FCSTD DOCUMENT  (FreeCAD 1.0R39109 (Git))
Label: Stator_Mold_Assembly
License: All rights reserved
LicenseURL: http://en.wikipedia.org/wiki/All_rights_reserved
objects: App::Link×7, Spreadsheet::Sheet×1, App::Part×1
EXTERNAL_REF file=Stator_Mold_Base.FCStd obj=Part001
EXTERNAL_REF file=../../../Master_of_Puppets.FCStd obj=Spreadsheet
EXTERNAL_REF file=Stator_Mold_BoltHeadLayer_Circular.FCStd obj=Part001
EXTERNAL_REF file=Stator_Mold_BoltHeadLayer_Hexagonal.FCStd obj=Part002
EXTERNAL_REF file=Stator_Mold_BoltShaftLayer_Circular.FCStd obj=Part001
EXTERNAL_REF file=Stator_Mold_BoltShaftLayer_Hexagonal.FCStd obj=Part003
EXTERNAL_REF file=Stator_Mold_Surround_Circular.FCStd obj=Body
EXTERNAL_REF file=Stator_Mold_Surround_Hexagonal.FCStd obj=Body
EXTERNAL_REF file=Stator_Mold_Island.FCStd obj=PolarPatternBody
EXTERNAL_REF file=Stator_Mold_Lid.FCStd obj=Pocket003Body
EXTERNAL_REF file=../Stator.FCStd obj=Part

FEATURE [App::Link] Link  label="Stator_Mold_Base"
  LinkedObject = -> <external Stator_Mold_Base.FCStd>#Part001
  expr: .Placement.Base.z = Spreadsheet.BaseZ
FEATURE [Spreadsheet::Sheet] Spreadsheet
  cells = A1='Inputs; A2='StatorThickness; B2(StatorThickness)==Master_of_Puppets#Spreadsheet.StatorThickness; A3='CalculatedWindTurbineShape; B3(CalculatedWindTurbineShape)==Master_of_Puppets#Spreadsheet.CalculatedWindTurbineShape; A4='Calculated; A5='DistanceBetweenLayers; B5(DistanceBetweenLayers)=0; A6='BaseZ; B6(BaseZ)==(StatorThickness + DistanceBetweenLayers) * 0; A7='BoltHeadLayerZ; B7(BoltHeadLayerZ)==(StatorThickness + DistanceBetweenLayers) * 1; A8='BoltShaftLayerZ; B8(BoltShaftLayerZ)==(StatorThickness + DistanceBetweenLayers) * 2; A9='SurroundZ; B9(SurroundZ)==(StatorThickness + DistanceBetweenLayers) * 3; A10='LidZ; B10(LidZ)==(StatorThickness + DistanceBetweenLayers) * 4; A11='BoltHeadLayer; A12='SmallBoltHeadLayer; B12(SmallBoltHeadLayer)==Stator_Mold_BoltHeadLayer_Circular#<<Stator_Mold_BoltHeadLayer_Assembly>>._self; A13='LargeBoltHeadLayer; B13(LargeBoltHeadLayer)==Stator_Mold_BoltHeadLayer_Hexagonal#<<Stator_Mold_BoltHeadLayer_Assembly>>._self; A14='BoltHeadLayer; B14(BoltHeadLayer)==CalculatedWindTurbineShape == <<Star>> ? LargeBoltHeadLayer : SmallBoltHeadLayer; A15='BoltShaftLayer; A16='SmallBoltShaftLayer; B16(SmallBoltShaftLayer)==Stator_Mold_BoltShaftLayer_Circular#<<Stator_Mold_BoltShaftLayer_Assembly>>._self; A17='LargeBoltShaftLayer; B17(LargeBoltShaftLayer)==Stator_Mold_BoltShaftLayer_Hexagonal#<<Stator_Mold_BoltShaftLayer_Assembly>>._self; A18='BoltShaftLayer; B18(BoltShaftLayer)==CalculatedWindTurbineShape == <<Star>> ? LargeBoltShaftLayer : SmallBoltShaftLayer; A19='Surround; A20='SmallSurround; B20(SmallSurround)==Stator_Mold_Surround_Circular#<<Stator_Mold_Surround>>._self; A21='LargeSurround; B21(LargeSurround)==Stator_Mold_Surround_Hexagonal#<<Stator_Mold_Surround>>._self; A22='Surround; B22(Surround)==CalculatedWindTurbineShape == <<Star>> ? LargeSurround : SmallSurround; A23='Stator; A24='StatorAngle; B24(StatorAngle)==CalculatedWindTurbineShape == <<T>> ? 60 : 0
FEATURE [App::Link] Link001  label="Stator_Mold_BoltHeadLayer"
  LinkPlacement = pos=(0,0,13) rot=(0,0,1;0rad)
  LinkedObject = -> <external Stator_Mold_BoltHeadLayer_Circular.FCStd>#Part001
  Placement = pos=(0,0,13) rot=(0,0,1;0rad)
  expr: .Placement.Base.z = Spreadsheet.BoltHeadLayerZ
  expr: LinkedObject = Spreadsheet.BoltHeadLayer
FEATURE [App::Link] Link002  label="Stator_Mold_BoltShaftLayer"
  LinkPlacement = pos=(0,0,26) rot=(0,0,1;0rad)
  LinkedObject = -> <external Stator_Mold_BoltShaftLayer_Circular.FCStd>#Part001
  Placement = pos=(0,0,26) rot=(0,0,1;0rad)
  expr: .Placement.Base.z = Spreadsheet.BoltShaftLayerZ
  expr: LinkedObject = Spreadsheet.BoltShaftLayer
FEATURE [App::Link] Link003  label="Stator_Mold_Surround"
  LinkPlacement = pos=(0,0,39) rot=(0,0,1;0rad)
  LinkedObject = -> <external Stator_Mold_Surround_Circular.FCStd>#Body
  Placement = pos=(0,0,39) rot=(0,0,1;0rad)
  expr: .Placement.Base.z = Spreadsheet.SurroundZ
  expr: LinkedObject = Spreadsheet.Surround
FEATURE [App::Link] Link004  label="Stator_Mold_Island"
  LinkPlacement = pos=(0,0,39) rot=(0,0,1;0rad)
  LinkedObject = -> <external Stator_Mold_Island.FCStd>#PolarPatternBody
  Placement = pos=(0,0,39) rot=(0,0,1;0rad)
  expr: .Placement.Base.z = Spreadsheet.SurroundZ
FEATURE [App::Link] Link005  label="Stator_Mold_Lid"
  LinkPlacement = pos=(0,0,52) rot=(0,0,1;0rad)
  LinkedObject = -> <external Stator_Mold_Lid.FCStd>#Pocket003Body
  Placement = pos=(0,0,52) rot=(0,0,1;0rad)
  expr: .Placement.Base.z = Spreadsheet.LidZ
FEATURE [App::Link] Link006  label="Stator"
  LinkPlacement = pos=(0,0,39) rot=(0,0,1;1.0472rad)
  LinkedObject = -> <external ../Stator.FCStd>#Part
  Placement = pos=(0,0,39) rot=(0,0,1;1.0472rad)
  expr: .Placement.Base.z = Spreadsheet.SurroundZ
  expr: .Placement.Rotation.Angle = Spreadsheet.StatorAngle
FEATURE [App::Part] Part  label="Stator_Mold_Assembly"
  Group = -> [Link,Link001,Link002,Link003,Link006,Link004,Link005]
  Origin = -> Origin

RESOLVED EXTERNAL PARTS (link-assembly join: the EXTERNAL_REF files above that resolve inside this repo's crawl, each included once):
---- part ../../../Master_of_Puppets.FCStd = doc fcstd_6404554055c4 (61625 chars; too large to inline — full recipe in that document) ----
---- part ../Stator.FCStd = doc fcstd_741fdd9bc27b ----
FCSTD DOCUMENT  (FreeCAD 0.21R33675 (Git))
Label: Stator
License: All rights reserved
LicenseURL: http://en.wikipedia.org/wiki/All_rights_reserved
objects: App::Link×2, Spreadsheet::Sheet×1, App::Part×1
EXTERNAL_REF file=../../Master_of_Puppets.FCStd obj=Alternator
EXTERNAL_REF file=../../Master_of_Puppets.FCStd obj=Spreadsheet
EXTERNAL_REF file=Stator_ResinCast_Circular.FCStd obj=PadBody001
EXTERNAL_REF file=Stator_ResinCast_Hexagonal.FCStd obj=Body
EXTERNAL_REF file=Stator_Coils.FCStd obj=Array

FEATURE [Spreadsheet::Sheet] Spreadsheet
  cells = A1='Inputs; A2='CalculatedWindTurbineShape; B2(CalculatedWindTurbineShape)==Master_of_Puppets#Spreadsheet.CalculatedWindTurbineShape; A3='StatorThickness; B3(StatorThickness)==Master_of_Puppets#Spreadsheet.StatorThickness; A4='MechanicalClearance; B4(MechanicalClearance)==Master_of_Puppets#Spreadsheet.MechanicalClearance; A5='MagnetThickness; B5(MagnetThickness)==Master_of_Puppets#Spreadsheet.MagnetThickness; A6='RotorDiskThickness; B6(RotorDiskThickness)==Master_of_Puppets#Spreadsheet.RotorDiskThickness; A7='CoilsAngle; B7(CoilsAngle)==Master_of_Puppets#Alternator.CoilsAngle; A8='StatorResinCast; A9='CircularStatorResinCast; B9(CircularStatorResinCast)==<<Stator_ResinCast_Circular>>#<<Stator_ResinCast>>._self; A10='HexagonalStatorResinCast; B10(HexagonalStatorResinCast)==<<Stator_ResinCast_Hexagonal>>#<<Stator_ResinCast>>._self; A11='StatorResinCast; B11(StatorResinCast)==CalculatedWindTurbineShape == <<Star>> ? HexagonalStatorResinCast : CircularStatorResinCast
FEATURE [App::Link] Link  label="ResinCast"
  LinkTransform = true
  LinkedObject = -> <external Stator_ResinCast_Circular.FCStd>#PadBody001
  expr: LinkedObject = Spreadsheet.StatorResinCast
FEATURE [App::Link] Link001  label="Coils"
  LinkPlacement = pos=(0,0,0) rot=(0,0,1;0.349066rad)
  LinkTransform = true
  LinkedObject = -> <external Stator_Coils.FCStd>#Array
  Placement = pos=(0,0,0) rot=(0,0,1;0.349066rad)
  expr: .LinkPlacement.Rotation.Angle = Spreadsheet.CoilsAngle
FEATURE [App::Part] Part  label="Stator"
  Group = -> [Link001,Link]
  Origin = -> Origin
---- part Stator_Mold_Base.FCStd = doc fcstd_d0ba9c10f7cb ----
FCSTD DOCUMENT  (FreeCAD 0.20R29177 (Git))
Label: Stator_Mold_Base
License: All rights reserved
LicenseURL: http://en.wikipedia.org/wiki/All_rights_reserved
objects: App::Link×6, App::Part×3, Sketcher::SketchObject×2, PartDesign::Pad×1, PartDesign::Pocket×1, Spreadsheet::Sheet×1, PartDesign::Body×1
note: 7 computed .brp shape members not serialized (recipe doc carries the construction recipe); baked Part::Feature solids carry a one-line shape summary decoded from their .brp
EXTERNAL_REF file=../../../Master_of_Puppets.FCStd obj=Alternator
EXTERNAL_REF file=../../../Master_of_Puppets.FCStd obj=Fastener
EXTERNAL_REF file=../../../Master_of_Puppets.FCStd obj=Spreadsheet
EXTERNAL_REF file=../../../Fasteners/Fastener_Bolt_Locating.FCStd obj=Binder
EXTERNAL_REF file=../../../Fasteners/Fastener_Washer_StatorMold.FCStd obj=Tube

FEATURE [Sketcher::SketchObject] Sketch
  AttachmentOffset = pos=(0,-12.5,0) rot=(0,0,1;0rad)
  FullyConstrained = true
  MapMode = 5
  Placement = pos=(0,-12.5,0) rot=(0,0,1;0rad)
  Support = -> [XY_Plane001]
  expr: .AttachmentOffset.Base.y = Spreadsheet.SketchY
  expr: Constraints[15] = Spreadsheet.StatorMoldSideLength
  sketch-geometry (6):
    g0: LineSegment StartX=-296.825 StartY=296.825 StartZ=0 EndX=296.825 EndY=296.825 EndZ=0
    g1: LineSegment StartX=296.825 StartY=296.825 StartZ=0 EndX=296.825 EndY=-296.825 EndZ=0
    g2: LineSegment StartX=296.825 StartY=-296.825 StartZ=0 EndX=-296.825 EndY=-296.825 EndZ=0
    g3: LineSegment StartX=-296.825 StartY=-296.825 StartZ=0 EndX=-296.825 EndY=296.825 EndZ=0
    g4: LineSegment StartX=-296.825 StartY=296.825 StartZ=0 EndX=296.825 EndY=-296.825 EndZ=0
    g5: LineSegment StartX=296.825 StartY=296.825 StartZ=0 EndX=-296.825 EndY=-296.825 EndZ=0
  constraints (16):
    c: Coincident(g0,g1)
    c: Coincident(g1,g2)
    c: Coincident(g2,g3)
    c: Coincident(g3,g0)
    c: Horizontal(g0)
    c: Horizontal(g2)
    c: Vertical(g1)
    c: Vertical(g3)
    c: Coincident(g4,g0)
    c: Coincident(g4,g1)
    c: Coincident(g5,g0)
    c: Coincident(g5,g2)
    c: PointOnObject(g-1,g5)
    c: PointOnObject(g-1,g4)
    c: Equal(g0,g3)
    c: Distance(g0) = 593.65
FEATURE [PartDesign::Pad] Pad
  AllowMultiFace = false
  Direction = (0,0,1)
  Length = 13
  Length2 = 100
  Profile = -> Sketch
  Type = 0
  expr: Length = Spreadsheet.StatorThickness
FEATURE [Sketcher::SketchObject] Sketch001
  AttachmentOffset = pos=(0,-12.5,0) rot=(0,0,1;0rad)
  FullyConstrained = true
  MapMode = 5
  Placement = pos=(0,-12.5,13) rot=(0,0,1;0rad)
  Support = -> [Pad]
  expr: .AttachmentOffset.Base.y = Spreadsheet.SketchY
  expr: Constraints[14] = Spreadsheet.StatorMoldBoltRadius
  expr: Constraints[5] = 45
  expr: Constraints[8] = Spreadsheet.DistanceOfLocatingHoleFromCenter
  sketch-geometry (6):
    g0: LineSegment StartX=-266.804 StartY=266.804 StartZ=0 EndX=0 EndY=0 EndZ=0
    g1: LineSegment StartX=0 StartY=0 StartZ=0 EndX=266.804 EndY=266.804 EndZ=0
    g2: LineSegment StartX=0 StartY=0 StartZ=0 EndX=266.804 EndY=-266.804 EndZ=0
    g3: Circle CenterX=-266.804 CenterY=266.804 CenterZ=0 NormalX=0 NormalY=0 NormalZ=1 AngleXU=0 Radius=6
    g4: Circle CenterX=266.804 CenterY=266.804 CenterZ=0 NormalX=0 NormalY=0 NormalZ=1 AngleXU=0 Radius=6
    g5: Circle CenterX=266.804 CenterY=-266.804 CenterZ=0 NormalX=0 NormalY=0 NormalZ=1 AngleXU=0 Radius=6
  constraints (15):
    c: Coincident(g0,g-1)
    c: Coincident(g0,g1)
    c: Coincident(g-1,g2)
    c: Parallel(g0,g2)
    c: Perpendicular(g2,g1)
    c: Angle(g-2,g0) = 0.785398
    c: Equal(g0,g1)
    c: Equal(g1,g2)
    c: Distance(g0) = 377.318
    c: Coincident(g3,g0)
    c: Coincident(g5,g2)
    c: Coincident(g4,g1)
    c: Equal(g3,g4)
    c: Equal(g4,g5)
    c: Radius(g3) = 6
FEATURE [PartDesign::Pocket] Pocket
  AllowMultiFace = false
  BaseFeature = -> Pad
  Direction = (0,0,-1)
  Length = 5
  Length2 = 100
  Profile = -> Sketch001
  Type = 1
FEATURE [Spreadsheet::Sheet] Spreadsheet
  cells = A1=Inputs; A2=Spreadsheet; A3=StatorThickness; B3(StatorThickness)==Master_of_Puppets#Spreadsheet.StatorThickness; A4=StatorMoldBoltDiameter; B4(StatorMoldBoltDiameter)==Master_of_Puppets#Alternator.StatorMoldBoltDiameter; A5=RotorDiskRadius; B5(RotorDiskRadius)==Master_of_Puppets#Spreadsheet.RotorDiskRadius; A6=Alternator; A7=StatorHolesCircumradius; B7(StatorHolesCircumradius)==Master_of_Puppets#Alternator.StatorHolesCircumradius; A8=EarSize; B8(EarSize)==Master_of_Puppets#Alternator.EarSize; A9=SketchY; B9(SketchY)==Master_of_Puppets#Alternator.SketchY; A10=StatorMoldSideLength; B10(StatorMoldSideLength)==Master_of_Puppets#Alternator.StatorMoldSideLength; A11=DistanceOfLocatingHoleFromCenter; B11(DistanceOfLocatingHoleFromCenter)==Master_of_Puppets#Alternator.DistanceOfLocatingHoleFromCenter; A12=LocatingBolt1X; B12(LocatingBolt1X)==Master_of_Puppets#Alternator.LocatingBolt1X; A13=LocatingBolt1Y; B13(LocatingBolt1Y)==Master_of_Puppets#Alternator.LocatingBolt1Y; A14=LocatingBolt2X; B14(LocatingBolt2X)==Master_of_Puppets#Alternator.LocatingBolt2X; A15=LocatingBolt2Y; B15(LocatingBolt2Y)==Master_of_Puppets#Alternator.LocatingBolt2Y; A16=LocatingBolt3X; B16(LocatingBolt3X)==Master_of_Puppets#Alternator.LocatingBolt3X; A17=LocatingBolt3Y; B17(LocatingBolt3Y)==Master_of_Puppets#Alternator.LocatingBolt3Y; A18=Fastener; A19=WasherThickness; B19(WasherThickness)==Master_of_Puppets#Fastener.WasherThickness; A20=Calculated; A21=StatorMoldBoltRadius; B21(StatorMoldBoltRadius)==StatorMoldBoltDiameter / 2; A22=BoltZ; B22(BoltZ)==-WasherThickness; A23=NutZ; B23(NutZ)==StatorThickness * 5; A24=WasherZ; B24(WasherZ)==-WasherThickness
FEATURE [PartDesign::Body] PocketBody  label="Stator_Mold_Base"
  Group = -> [Sketch,Pad,Sketch001,Pocket]
  Openafpm_Flat = true
  Origin = -> Origin001
  Tip = -> Pocket
FEATURE [App::Link] Link001  label="Fastener_Bolt2"
  LinkPlacement = pos=(266.804,254.304,-2.5) rot=(0,0,1;0rad)
  LinkedObject = -> Link
  Placement = pos=(266.804,254.304,-2.5) rot=(0,0,1;0rad)
  expr: .Placement.Base.x = Spreadsheet.LocatingBolt2X
  expr: .Placement.Base.y = Spreadsheet.LocatingBolt2Y
  expr: .Placement.Base.z = Spreadsheet.BoltZ
FEATURE [App::Link] Link002  label="Fastener_Bolt3"
  LinkPlacement = pos=(266.804,-279.304,-2.5) rot=(0,0,1;0rad)
  LinkedObject = -> Link001
  Placement = pos=(266.804,-279.304,-2.5) rot=(0,0,1;0rad)
  expr: .Placement.Base.x = Spreadsheet.LocatingBolt3X
  expr: .Placement.Base.y = Spreadsheet.LocatingBolt3Y
  expr: .Placement.Base.z = Spreadsheet.BoltZ
FEATURE [App::Link] Link  label="Fastener_Bolt1"
  LinkPlacement = pos=(-266.804,254.304,-2.5) rot=(0,0,1;0rad)
  LinkedObject = -> <external ../../../Fasteners/Fastener_Bolt_Locating.FCStd>#Binder
  Placement = pos=(-266.804,254.304,-2.5) rot=(0,0,1;0rad)
  Scale = -1
  ScaleVector = (-1,-1,-1)
  expr: .Placement.Base.x = Spreadsheet.LocatingBolt1X
  expr: .Placement.Base.y = Spreadsheet.LocatingBolt1Y
  expr: .Placement.Base.z = Spreadsheet.BoltZ
FEATURE [App::Part] Part  label="LocatingBolts"
  Group = -> [Link,Link001,Link002]
  Origin = -> Origin
FEATURE [App::Link] Link003  label="Washer1"
  LinkPlacement = pos=(-266.804,254.304,-2.5) rot=(0,0,1;0rad)
  LinkedObject = -> <external ../../../Fasteners/Fastener_Washer_StatorMold.FCStd>#Tube
  Placement = pos=(-266.804,254.304,-2.5) rot=(0,0,1;0rad)
  expr: .Placement.Base.x = Spreadsheet.LocatingBolt1X
  expr: .Placement.Base.y = Spreadsheet.LocatingBolt1Y
  expr: .Placement.Base.z = Spreadsheet.WasherZ
FEATURE [App::Link] Link004  label="Washer2"
  LinkPlacement = pos=(266.804,254.304,-2.5) rot=(0,0,1;0rad)
  LinkedObject = -> Link003
  Placement = pos=(266.804,254.304,-2.5) rot=(0,0,1;0rad)
  expr: .Placement.Base.x = Spreadsheet.LocatingBolt2X
  expr: .Placement.Base.y = Spreadsheet.LocatingBolt2Y
  expr: .Placement.Base.z = Spreadsheet.WasherZ
FEATURE [App::Link] Link005  label="Washer3"
  LinkPlacement = pos=(266.804,-279.304,-2.5) rot=(0,0,1;0rad)
  LinkedObject = -> Link004
  Placement = pos=(266.804,-279.304,-2.5) rot=(0,0,1;0rad)
  expr: .Placement.Base.x = Spreadsheet.LocatingBolt3X
  expr: .Placement.Base.y = Spreadsheet.LocatingBolt3Y
  expr: .Placement.Base.z = Spreadsheet.WasherZ
FEATURE [App::Part] Part002  label="LocatingWashers"
  Group = -> [Link003,Link004,Link005]
  Origin = -> Origin003
FEATURE [App::Part] Part001  label="Stator_Mold_Base_Assembly"
  Group = -> [PocketBody,Part,Part002]
  Origin = -> Origin002
---- part Stator_Mold_BoltHeadLayer_Circular.FCStd = doc fcstd_cd0f8b75a41d ----
FCSTD DOCUMENT  (FreeCAD 1.0R39109 (Git))
Label: Stator_Mold_BoltHeadLayer_Circular
License: All rights reserved
LicenseURL: http://en.wikipedia.org/wiki/All_rights_reserved
objects: App::Link×18, Part::FeaturePython×12, App::Part×9, Sketcher::SketchObject×4, PartDesign::PolarPattern×4, PartDesign::Pocket×4, Part::Mirroring×3, PartDesign::Plane×1, PartDesign::Mirrored×1, PartDesign::SubShapeBinder×1, PartDesign::FeatureBase×1, PartDesign::MultiTransform×1, Spreadsheet::Sheet×1, PartDesign::Body×1
note: 40 computed .brp shape members not serialized (recipe doc carries the construction recipe); baked Part::Feature solids carry a one-line shape summary decoded from their .brp
EXTERNAL_REF file=Stator_Mold_Base.FCStd obj=PocketBody
EXTERNAL_REF file=../../../Master_of_Puppets.FCStd obj=Alternator
EXTERNAL_REF file=../../../Master_of_Puppets.FCStd obj=Fastener
EXTERNAL_REF file=../../../Master_of_Puppets.FCStd obj=Spreadsheet
EXTERNAL_REF file=../../../Fasteners/Fastener_Bolt_StatorMold.FCStd obj=Binder
EXTERNAL_REF file=../../../Fasteners/Fastener_HexNut_StatorMold.FCStd obj=Binder
EXTERNAL_REF file=../../../Fasteners/Fastener_Washer_StatorMold.FCStd obj=Tube

FEATURE [PartDesign::Plane] DatumPlane001  label="DatumPlane"
  AttachmentOffset = pos=(0,0,13) rot=(0,0,1;0rad)
  AttachmentSupport = -> [XY_Plane]
  Length = 1060.2
  MapMode = 5
  Placement = pos=(0,0,13) rot=(0,0,1;0rad)
  ResizeMode = 0
  Width = 1060.2
  expr: .AttachmentOffset.Base.z = Spreadsheet.StatorThickness
FEATURE [Sketcher::SketchObject] Sketch005  label="MiddleHolesSketch"
  ArcFitTolerance = 0
  AttachmentOffset = pos=(0,0,0) rot=(0,0,1;0.785398rad)
  AttachmentSupport = -> [DatumPlane001]
  FullyConstrained = true
  MakeInternals = false
  MapMode = 5
  Placement = pos=(0,0,13) rot=(0,0,1;0.785398rad)
  expr: .AttachmentOffset.Rotation.Angle = Spreadsheet.StatorMoldHolesSketchAngle
  expr: Constraints[16] = Spreadsheet.EarAngle
  expr: Constraints[20] = Spreadsheet.LargeHoleAngle
  expr: Constraints[3] = Spreadsheet.LengthMiddleHoles
  expr: Constraints[40] = Spreadsheet.Inradius
  expr: Constraints[6] = Spreadsheet.EarSize
  sketch-geometry (17):
    g0: Circle [constr] CenterX=0 CenterY=0 CenterZ=0 NormalX=0 NormalY=0 NormalZ=1 AngleXU=0 Radius=309
    g1: LineSegment [constr] StartX=0 StartY=0 StartZ=0 EndX=0 EndY=-309 EndZ=0
    g2: Circle [constr] CenterX=0 CenterY=-309 CenterZ=0 NormalX=0 NormalY=0 NormalZ=1 AngleXU=0 Radius=35
    g3: LineSegment [constr] StartX=16.18 StartY=-340.036 StartZ=0 EndX=142.846 EndY=-274 EndZ=0
    g4: LineSegment [constr] StartX=-16.18 StartY=-340.036 StartZ=0 EndX=-142.846 EndY=-274 EndZ=0
    g5: LineSegment [constr] StartX=0 StartY=0 StartZ=0 EndX=-218.496 EndY=-218.496 EndZ=0
    g6: LineSegment [constr] StartX=0 StartY=0 StartZ=0 EndX=218.496 EndY=-218.496 EndZ=0
    g7: ArcOfCircle [constr] CenterX=0 CenterY=0 CenterZ=0 NormalX=0 NormalY=0 NormalZ=1 AngleXU=0 Radius=309 StartAngle=3.92699 EndAngle=4.23182
    g8: ArcOfCircle [constr] CenterX=0 CenterY=0 CenterZ=0 NormalX=0 NormalY=0 NormalZ=1 AngleXU=0 Radius=309 StartAngle=5.19296 EndAngle=5.49779
    g9: LineSegment [constr] StartX=0 StartY=0 StartZ=0 EndX=-118.249 EndY=-285.479 EndZ=0
    g10: LineSegment StartX=-118.249 StartY=-295.869 StartZ=0 EndX=-109.251 EndY=-290.674 EndZ=0
    g11: LineSegment StartX=-109.251 StartY=-290.674 StartZ=0 EndX=-109.251 EndY=-280.284 EndZ=0
    g12: LineSegment StartX=-109.251 StartY=-280.284 StartZ=0 EndX=-118.249 EndY=-275.089 EndZ=0
    g13: LineSegment StartX=-118.249 StartY=-275.089 StartZ=0 EndX=-127.247 EndY=-280.284 EndZ=0
    g14: LineSegment StartX=-127.247 StartY=-280.284 StartZ=0 EndX=-127.247 EndY=-290.674 EndZ=0
    g15: LineSegment StartX=-127.247 StartY=-290.674 StartZ=0 EndX=-118.249 EndY=-295.869 EndZ=0
    g16: Circle [constr] CenterX=-118.249 CenterY=-285.479 CenterZ=0 NormalX=0 NormalY=0 NormalZ=1 AngleXU=0 Radius=10.39
  constraints (40):
    c: Coincident(g0,g-1)
    c: Coincident(g1,g-1)
    c: Vertical(g1)
    c: Radius(g0) = 309
    c: Coincident(g2,g1)
    c: Tangent(g3,g0)
    c: Radius(g2) = 35
    c: Symmetric(g6,g5,g1)
    c: Coincident(g7,g5)
    c: Coincident(g7,g4)
    c: Coincident(g8,g6)
    c: Coincident(g8,g3)
    c: Coincident(g6,g5)
    c: Coincident(g5,g7)
    c: Coincident(g5,g-1)
    c: Coincident(g8,g5)
    c: Angle(g5,g6) = 1.5708
    c: Tangent(g3,g2) = -1.5708
    c: Tangent(g4,g0) = 1.5708
    c: Coincident(g9,g-1)
    c: Angle(g5,g9) = 0.392699
    c: Tangent(g4,g2) = 1.5708
    c: PointOnObject(g1,g0)
    c: Coincident(g10,g11)
    c: Coincident(g11,g12)
    c: Coincident(g12,g13)
    c: Coincident(g13,g14)
    c: Coincident(g14,g15)
    c: Coincident(g15,g10)
    c: Equal(g10, g11-g15) x5
    c: PointOnObject(g10,g16)
    c: PointOnObject(g12,g16)
    c: PointOnObject(g13,g16)
    c: PointOnObject(g14,g16)
    c: PointOnObject(g15,g16)
    c: Coincident(g16,g9)
    c: Radius(g16) = 10.39
    c: PointOnObject(g11,g16)
    c: Vertical(g10,g12)
    c: PointOnObject(g9,g0)
FEATURE [PartDesign::Mirrored] Mirrored  label="MiddleHolesMirrored"
  MirrorPlane = -> Sketch005 [V_Axis]
  Suppressed = false
  TransformMode = 0
FEATURE [PartDesign::PolarPattern] PolarPattern002  label="MiddleHolesPolarPattern"
  Angle = 360
  Axis = -> Sketch005 [N_Axis]
  Mode = 0
  Occurrences = 4
  Offset = 120
  Suppressed = false
  TransformMode = 0
  expr: Occurrences = Spreadsheet.NumberOfStatorHoles
FEATURE [Sketcher::SketchObject] Sketch006  label="LargeHoleOuterSketch"
  ArcFitTolerance = 0
  AttachmentOffset = pos=(0,0,0) rot=(0,0,1;0.785398rad)
  AttachmentSupport = -> [DatumPlane001]
  FullyConstrained = true
  MakeInternals = false
  MapMode = 5
  Placement = pos=(0,0,13) rot=(0,0,1;0.785398rad)
  expr: .AttachmentOffset.Rotation.Angle = Spreadsheet.StatorMoldHolesSketchAngle
  expr: Constraints[16] = Spreadsheet.Inradius
  expr: Constraints[1] = Spreadsheet.LargeHoleCircumradius
  sketch-geometry (14):
    g0: Circle [constr] CenterX=0 CenterY=0 CenterZ=0 NormalX=0 NormalY=0 NormalZ=1 AngleXU=0 Radius=344
    g1: LineSegment StartX=5.195 StartY=-335.002 StartZ=0 EndX=-5.195 EndY=-335.002 EndZ=0
    g2: LineSegment StartX=-5.195 StartY=-335.002 StartZ=0 EndX=-10.39 EndY=-344 EndZ=0
    g3: LineSegment StartX=-10.39 StartY=-344 StartZ=0 EndX=-5.195 EndY=-352.998 EndZ=0
    g4: LineSegment StartX=-5.195 StartY=-352.998 StartZ=0 EndX=5.195 EndY=-352.998 EndZ=0
    g5: LineSegment StartX=5.195 StartY=-352.998 StartZ=0 EndX=10.39 EndY=-344 EndZ=0
    g6: LineSegment StartX=10.39 StartY=-344 StartZ=0 EndX=5.195 EndY=-335.002 EndZ=0
    g7: Circle [constr] CenterX=9e-16 CenterY=-344 CenterZ=0 NormalX=0 NormalY=0 NormalZ=1 AngleXU=0 Radius=10.39
    g8: LineSegment [constr] StartX=-5.195 StartY=-352.998 StartZ=0 EndX=9e-16 EndY=-344 EndZ=0
    g9: LineSegment [constr] StartX=9e-16 StartY=-344 StartZ=0 EndX=5.195 EndY=-335.002 EndZ=0
    g10: LineSegment [constr] StartX=-5.195 StartY=-335.002 StartZ=0 EndX=9e-16 EndY=-344 EndZ=0
    g11: LineSegment [constr] StartX=9e-16 StartY=-344 StartZ=0 EndX=5.195 EndY=-352.998 EndZ=0
    g12: LineSegment [constr] StartX=-10.39 StartY=-344 StartZ=0 EndX=0 EndY=-344 EndZ=0
    g13: LineSegment [constr] StartX=9e-16 StartY=-344 StartZ=0 EndX=10.39 EndY=-344 EndZ=0
  constraints (35):
    c: Coincident(g0,g-1)
    c: Radius(g0) = 344
    c: Coincident(g1,g2)
    c: Coincident(g2,g3)
    c: Coincident(g3,g4)
    c: Coincident(g4,g5)
    c: Coincident(g5,g6)
    c: Coincident(g6,g1)
    c: PointOnObject(g1,g7)
    c: PointOnObject(g2,g7)
    c: PointOnObject(g3,g7)
    c: PointOnObject(g4,g7)
    c: PointOnObject(g5,g7)
    c: PointOnObject(g6,g7)
    c: PointOnObject(g7,g0)
    c: PointOnObject(g7,g-2)
    c: Radius(g7) = 10.39
    c: Coincident(g8,g3)
    c: Coincident(g8,g7)
    c: Coincident(g9,g8)
    c: Coincident(g9,g1)
    c: Coincident(g1,g10)
    c: Coincident(g10,g8)
    c: Coincident(g10,g11)
    c: Coincident(g2,g12)
    c: Coincident(g12,g8)
    c: Coincident(g12,g13)
    c: Coincident(g13,g5)
    c: Angle(g9,g10) = 1.0472
    c: Angle(g13,g9) = 1.0472
    c: Angle(g11,g13) = 1.0472
    c: Angle(g8,g11) = 1.0472
    c: Angle(g12,g8) = 1.0472
    c: Horizontal(g2,g5)
    c: Coincident(g11,g4)
FEATURE [Sketcher::SketchObject] Sketch007  label="LargeHoleInnerSketch"
  ArcFitTolerance = 0
  AttachmentSupport = -> [DatumPlane001]
  FullyConstrained = true
  MakeInternals = false
  MapMode = 5
  Placement = pos=(0,0,13) rot=(0,0,1;0rad)
  expr: Constraints[1] = Spreadsheet.LengthMiddleHoles
  expr: Constraints[31] = Spreadsheet.Inradius
  sketch-geometry (14):
    g0: Circle [constr] CenterX=0 CenterY=0 CenterZ=0 NormalX=0 NormalY=0 NormalZ=1 AngleXU=0 Radius=309
    g1: LineSegment StartX=-5.195 StartY=317.998 StartZ=0 EndX=-10.39 EndY=309 EndZ=0
    g2: LineSegment StartX=-10.39 StartY=309 StartZ=0 EndX=-5.195 EndY=300.002 EndZ=0
    g3: LineSegment StartX=-5.195 StartY=300.002 StartZ=0 EndX=5.195 EndY=300.002 EndZ=0
    g4: LineSegment StartX=5.195 StartY=300.002 StartZ=0 EndX=10.39 EndY=309 EndZ=0
    g5: LineSegment StartX=10.39 StartY=309 StartZ=0 EndX=5.195 EndY=317.998 EndZ=0
    g6: LineSegment StartX=5.195 StartY=317.998 StartZ=0 EndX=-5.195 EndY=317.998 EndZ=0
    g7: Circle [constr] CenterX=0 CenterY=309 CenterZ=0 NormalX=0 NormalY=0 NormalZ=1 AngleXU=0 Radius=10.39
    g8: LineSegment [constr] StartX=-5.195 StartY=317.998 StartZ=0 EndX=0 EndY=309 EndZ=0
    g9: LineSegment [constr] StartX=0 StartY=309 StartZ=0 EndX=5.195 EndY=300.002 EndZ=0
    g10: LineSegment [constr] StartX=-5.195 StartY=300.002 StartZ=0 EndX=0 EndY=309 EndZ=0
    g11: LineSegment [constr] StartX=0 StartY=309 StartZ=0 EndX=5.195 EndY=317.998 EndZ=0
    g12: LineSegment [constr] StartX=-10.39 StartY=309 StartZ=0 EndX=0 EndY=309 EndZ=0
    g13: LineSegment [constr] StartX=0 StartY=309 StartZ=0 EndX=10.39 EndY=309 EndZ=0
  constraints (35):
    c: Coincident(g0,g-1)
    c: Radius(g0) = 309
    c: PointOnObject(g7,g0)
    c: Coincident(g1,g2)
    c: Coincident(g2,g3)
    c: Coincident(g3,g4)
    c: Coincident(g4,g5)
    c: Coincident(g5,g6)
    c: Coincident(g6,g1)
    c: PointOnObject(g1,g7)
    c: PointOnObject(g2,g7)
    c: PointOnObject(g3,g7)
    c: PointOnObject(g4,g7)
    c: PointOnObject(g5,g7)
    c: PointOnObject(g6,g7)
    c: Coincident(g8,g1)
    c: Coincident(g9,g8)
    c: Coincident(g9,g3)
    c: Coincident(g10,g2)
    c: Coincident(g10,g8)
    c: Coincident(g11,g8)
    c: Coincident(g11,g5)
    c: Coincident(g12,g1)
    c: Coincident(g12,g8)
    c: Coincident(g13,g8)
    c: Coincident(g13,g4)
    c: Angle(g11,g8) = 1.0472
    c: Angle(g13,g11) = 1.0472
    c: Angle(g9,g13) = 1.0472
    c: Angle(g10,g9) = 1.0472
    c: Angle(g12,g10) = 1.0472
    c: Radius(g7) = 10.39
    c: Horizontal(g4,g1)
    c: Coincident(g8,g7)
    c: PointOnObject(g7,g-2)
FEATURE [PartDesign::SubShapeBinder] Binder
  BindCopyOnChange = 0
  BindMode = 0
  ClaimChildren = true
  Context = -> Body [Binder.]
  Fuse = false
  MakeFace = true
  OffsetFill = false
  OffsetIntersection = false
  OffsetJoinType = 0
  OffsetOpenResult = false
  PartialLoad = false
  Refine = true
  Relative = true
  Support = -> [<external Stator_Mold_Base.FCStd>#PocketBody]
  _Version = 2
FEATURE [PartDesign::FeatureBase] BaseFeature
  BaseFeature = -> Binder
  Suppressed = false
FEATURE [PartDesign::Pocket] Pocket001  label="MiddleHolesPocket"
  BaseFeature = -> BaseFeature
  Direction = (0,0,-1)
  Length = 5
  Length2 = 100
  Profile = -> Sketch005
  Suppressed = false
  Type = 1
FEATURE [PartDesign::MultiTransform] MultiTransform  label="MiddleHolesMultiTransform"
  BaseFeature = -> Pocket001
  Originals = -> [Pocket001]
  Suppressed = false
  TransformMode = 0
  Transformations = -> [Mirrored,PolarPattern002]
FEATURE [PartDesign::Pocket] Pocket002  label="LargeHoleOuterPocket"
  BaseFeature = -> MultiTransform
  Direction = (0,0,-1)
  Length = 5
  Length2 = 100
  Profile = -> Sketch006
  Suppressed = false
  Type = 1
FEATURE [PartDesign::PolarPattern] PolarPattern003  label="LargeHoleOuterPolarPattern"
  Angle = 360
  Axis = -> Sketch006 [N_Axis]
  BaseFeature = -> Pocket002
  Mode = 0
  Occurrences = 4
  Offset = 120
  Originals = -> [Pocket002]
  Suppressed = false
  TransformMode = 0
  expr: Occurrences = Spreadsheet.NumberOfStatorHoles
FEATURE [PartDesign::Pocket] Pocket003  label="LargeHoleInnerPocket"
  BaseFeature = -> PolarPattern003
  Direction = (0,0,-1)
  Length = 5
  Length2 = 100
  Profile = -> Sketch007
  Suppressed = false
  Type = 1
FEATURE [PartDesign::PolarPattern] PolarPattern004  label="LargeHoleInnerPolarPattern"
  Angle = 360
  Axis = -> Z_Axis
  BaseFeature = -> Pocket003
  Mode = 0
  Occurrences = 4
  Offset = 120
  Originals = -> [Pocket003]
  Suppressed = false
  TransformMode = 0
  expr: Angle = Spreadsheet.LargeInnerPolarPatternOverallAngle
  expr: Occurrences = Spreadsheet.LargeInnerPolarPatternOccurrences
FEATURE [Spreadsheet::Sheet] Spreadsheet
  cells = A1='Inputs; A2='Spreadsheet; A3='StatorThickness; A4(StatorThickness)==Master_of_Puppets#Spreadsheet.StatorThickness; A5='Alternator; A6='EarSize; B6='NumberOfStatorHoles; C6='IslandInnerRadius; A7(EarSize)==Master_of_Puppets#Alternator.EarSize; B7(NumberOfStatorHoles)==Master_of_Puppets#Alternator.NumberOfStatorHoles; C7(IslandInnerRadius)==Master_of_Puppets#Alternator.IslandInnerRadius; A8='EarAngle; B8='StatorMoldBoltWidthAcrossCorners; C8='StatorHolesCircumradius; A9(EarAngle)==Master_of_Puppets#Alternator.EarAngle; B9(StatorMoldBoltWidthAcrossCorners)==Master_of_Puppets#Alternator.StatorMoldBoltWidthAcrossCorners; C9(StatorHolesCircumradius)==Master_of_Puppets#Alternator.StatorHolesCircumradius; A10='LengthMiddleHoles; B10='StatorMoldIslandNumberOfBolts; C10='StatorMoldHolesSketchAngle; A11(LengthMiddleHoles)==Master_of_Puppets#Alternator.LengthMiddleHoles; B11(StatorMoldIslandNumberOfBolts)==Master_of_Puppets#Alternator.StatorMoldIslandNumberOfBolts; C11(StatorMoldHolesSketchAngle)==Master_of_Puppets#Alternator.StatorMoldHolesSketchAngle; A12='LocatingBolt1X; B12='LocatingBolt1Y; A13(LocatingBolt1X)==Master_of_Puppets#Alternator.LocatingBolt1X; B13(LocatingBolt1Y)==Master_of_Puppets#Alternator.LocatingBolt1Y; A14='LocatingBolt2X; B14='LocatingBolt2Y; A15(LocatingBolt2X)==Master_of_Puppets#Alternator.LocatingBolt2X; B15(LocatingBolt2Y)==Master_of_Puppets#Alternator.LocatingBolt2Y; A16='LocatingBolt3X; B16='LocatingBolt3Y; A17(LocatingBolt3X)==Master_of_Puppets#Alternator.LocatingBolt3X; B17(LocatingBolt3Y)==Master_of_Puppets#Alternator.LocatingBolt3Y; A18='LargeInnerPolarPatternOccurrences; B18='LargeInnerPolarPatternOverallAngle; A19(LargeInnerPolarPatternOccurrences)==Master_of_Puppets#Alternator.LargeInnerPolarPatternOccurrences; B19(LargeInnerPolarPatternOverallAngle)==Master_of_Puppets#Alternator.LargeInnerPolarPatternOverallAngle; A20='Fastener; A21='HexNutThickness; B21='WasherThickness; A22(HexNutThickness)==Master_of_Puppets#Fastener.HexNutThickness; B22(WasherThickness)==Master_of_Puppets#Fastener.WasherThickness; A23='Static; A24='BoltAngle; A25(BoltAngle)==30 deg; A26='Calculated; A27='LargeHoleCircumradius; B27='LargeHoleAngle; C27='Inradius; D27='https://calcresource.com/geom-hexagon.html; A28(LargeHoleCircumradius)==LengthMiddleHoles + EarSize; B28(LargeHoleAngle)==EarAngle / 4; C28(Inradius)==StatorMoldBoltWidthAcrossCorners / 2; A29='Fastener_Middle_X; B29='Fastener_Middle_Y; C29='TopOfStatorMold; D29='Duplicated in Stator_Mold_BoltHeadLayer_Hexagonal; A30(Fastener_Middle_X)==-LengthMiddleHoles * sin(LargeHoleAngle); B30(Fastener_Middle_Y)==-LengthMiddleHoles * cos(LargeHoleAngle); C30(TopOfStatorMold)==StatorThickness * 4; A31='HexNutZ; A32(HexNutZ)==TopOfStatorMold + WasherThickness
FEATURE [Sketcher::SketchObject] Sketch  label="InnerBoltHeadHoleSketch"
  ArcFitTolerance = 0
  AttachmentSupport = -> [DatumPlane001]
  FullyConstrained = true
  MakeInternals = false
  MapMode = 5
  Placement = pos=(0,0,13) rot=(0,0,1;0rad)
  expr: Constraints[1] = Spreadsheet.IslandInnerRadius
  expr: Constraints[33] = Spreadsheet.Inradius
  sketch-geometry (14):
    g0: Circle [constr] CenterX=0 CenterY=0 CenterZ=0 NormalX=0 NormalY=0 NormalZ=1 AngleXU=0 Radius=128.499
    g1: LineSegment StartX=5.19515 StartY=137.497 StartZ=0 EndX=-5.19485 EndY=137.497 EndZ=0
    g2: LineSegment StartX=-5.19485 StartY=137.497 StartZ=0 EndX=-10.3898 EndY=128.499 EndZ=0
    g3: LineSegment StartX=-10.3898 StartY=128.499 StartZ=0 EndX=-5.19485 EndY=119.501 EndZ=0
    g4: LineSegment StartX=-5.19485 StartY=119.501 StartZ=0 EndX=5.19515 EndY=119.501 EndZ=0
    g5: LineSegment StartX=5.19515 StartY=119.501 StartZ=0 EndX=10.3902 EndY=128.499 EndZ=0
    g6: LineSegment StartX=10.3902 StartY=128.499 StartZ=0 EndX=5.19515 EndY=137.497 EndZ=0
    g7: Circle [constr] CenterX=0.000154142 CenterY=128.499 CenterZ=0 NormalX=0 NormalY=0 NormalZ=1 AngleXU=0 Radius=10.39
    g8: LineSegment [constr] StartX=-5.19485 StartY=119.501 StartZ=0 EndX=0.000154142 EndY=128.499 EndZ=0
    g9: LineSegment [constr] StartX=0.000154142 StartY=128.499 StartZ=0 EndX=5.19515 EndY=137.497 EndZ=0
    g10: LineSegment [constr] StartX=10.3902 StartY=128.499 StartZ=0 EndX=0.000154142 EndY=128.499 EndZ=0
    g11: LineSegment [constr] StartX=0.000154142 StartY=128.499 StartZ=0 EndX=-10.3898 EndY=128.499 EndZ=0
    g12: LineSegment [constr] StartX=-5.19485 StartY=137.497 StartZ=0 EndX=0.000154142 EndY=128.499 EndZ=0
    g13: LineSegment [constr] StartX=0.000154142 StartY=128.499 StartZ=0 EndX=5.19515 EndY=119.501 EndZ=0
  constraints (35):
    c: Coincident(g0,g-1)
    c: Radius(g0) = 128.499
    c: Coincident(g1,g2)
    c: Coincident(g2,g3)
    c: Coincident(g3,g4)
    c: Coincident(g4,g5)
    c: Coincident(g5,g6)
    c: Coincident(g6,g1)
    c: PointOnObject(g1,g7)
    c: PointOnObject(g2,g7)
    c: PointOnObject(g3,g7)
    c: PointOnObject(g4,g7)
    c: PointOnObject(g5,g7)
    c: PointOnObject(g6,g7)
    c: PointOnObject(g7,g0)
    c: Coincident(g3,g8)
    c: Coincident(g8,g7)
    c: Coincident(g8,g9)
    c: Coincident(g9,g1)
    c: Coincident(g5,g10)
    c: Coincident(g10,g8)
    c: Tangent(g10,g0)
    c: Coincident(g10,g11)
    c: Coincident(g1,g12)
    c: Coincident(g12,g8)
    c: Coincident(g12,g13)
    c: Coincident(g13,g4)
    c: Angle(g8,g13) = 1.0472
    c: Angle(g13,g10) = 1.0472
    c: Angle(g10,g9) = 1.0472
    c: Angle(g9,g12) = 1.0472
    c: Angle(g11,g8) = 1.0472
    c: Horizontal(g11,g5)
    c: Radius(g7) = 10.39
    c: Coincident(g11,g2)
FEATURE [PartDesign::Pocket] Pocket  label="InnerBoltHeadHolePocket"
  BaseFeature = -> PolarPattern004
  Direction = (0,0,-1)
  Length = 5
  Length2 = 100
  Profile = -> Sketch
  Suppressed = false
  Type = 1
FEATURE [PartDesign::PolarPattern] PolarPattern  label="InnerBoltHeadHolePolarPattern"
  Angle = 360
  Axis = -> Z_Axis
  BaseFeature = -> Pocket
  Mode = 0
  Occurrences = 6
  Offset = 120
  Originals = -> [Pocket]
  Suppressed = false
  TransformMode = 0
  expr: Occurrences = Spreadsheet.StatorMoldIslandNumberOfBolts
FEATURE [PartDesign::Body] Body  label="Stator_Mold_BoltHeadLayer"
  AllowCompound = false
  BaseFeature = -> Binder
  Group = -> [BaseFeature,DatumPlane001,Sketch005,Pocket001,MultiTransform,Mirrored,PolarPattern002,Sketch006,Pocket002,PolarPattern003,Sketch007,Pocket003,PolarPattern004,Sketch,Pocket,PolarPattern]
  Openafpm_Flat = true
  Origin = -> Origin
  Tip = -> PolarPattern
FEATURE [App::Link] Link  label="Fastener_Bolt_Inner"
  LinkPlacement = pos=(0,128.499,11.83) rot=(0,0,1;0.523599rad)
  LinkedObject = -> <external ../../../Fasteners/Fastener_Bolt_StatorMold.FCStd>#Binder
  Placement = pos=(0,128.499,11.83) rot=(0,0,1;0.523599rad)
  Scale = -1
  ScaleVector = (-1,-1,-1)
  expr: .Placement.Base.y = Spreadsheet.IslandInnerRadius
  expr: .Placement.Base.z = Spreadsheet.HexNutThickness
  expr: .Placement.Rotation.Angle = Spreadsheet.BoltAngle
FEATURE [Part::FeaturePython] Array  label="Bolts_Inner"  # Draft array (typed FeaturePython)
  AlwaysSyncPlacement = false
  Angle = 360
  ArrayType = 1
  Axis = (0,0,1)
  Base = -> Link
  Center = (0,0,0)
  Count = 6
  ExpandArray = false
  Fuse = false
  IntervalAxis = (0,0,0)
  IntervalX = (50,0,0)
  IntervalY = (0,50,0)
  IntervalZ = (0,0,50)
  NumberCircles = 3
  NumberPolar = 6
  NumberX = 2
  NumberY = 2
  NumberZ = 1
  PlacementList = 6 placements: [(0,128.499,11.83),(-111.284,64.2497,11.83),(-111.284,-64.2497,11.83),(-1.57366e-14,-128.499,11.83),(111.284,-64.2497,11.83),(111.284,64.2497,11.83)]
  RadialDistance = 50
  ScaleList = (6) [(1,1,1),(1,1,1),(1,1,1),(1,1,1),(1,1,1),(1,1,1)]
  Symmetry = 1
  TangentialDistance = 25
  expr: NumberPolar = Spreadsheet.StatorMoldIslandNumberOfBolts
FEATURE [App::Link] Link001  label="Fastener_Bolt_Middle"
  LinkPlacement = pos=(-118.249,-285.479,11.83) rot=(0,0,1;0rad)
  LinkedObject = -> Link
  Placement = pos=(-118.249,-285.479,11.83) rot=(0,0,1;0rad)
  expr: .Placement.Base.x = Spreadsheet.Fastener_Middle_X
  expr: .Placement.Base.y = Spreadsheet.Fastener_Middle_Y
  expr: .Placement.Base.z = Spreadsheet.HexNutThickness
FEATURE [App::Link] Link002  label="Fastener_Bolt_LargeOuter"
  LinkPlacement = pos=(0,-344,11.83) rot=(0,0,1;0.523599rad)
  LinkedObject = -> Link001
  Placement = pos=(0,-344,11.83) rot=(0,0,1;0.523599rad)
  expr: .Placement.Base.y = -Spreadsheet.LargeHoleCircumradius
  expr: .Placement.Base.z = Spreadsheet.HexNutThickness
  expr: .Placement.Rotation.Angle = Spreadsheet.BoltAngle
FEATURE [Part::FeaturePython] Array002  label="Bolts_LargeOuter"  # Draft array (typed FeaturePython)
  AlwaysSyncPlacement = false
  Angle = 360
  ArrayType = 1
  Axis = (0,0,1)
  Base = -> Link002
  Center = (0,0,0)
  Count = 4
  ExpandArray = false
  Fuse = false
  IntervalAxis = (0,0,0)
  IntervalX = (50,0,0)
  IntervalY = (0,50,0)
  IntervalZ = (0,0,50)
  NumberCircles = 3
  NumberPolar = 4
  NumberX = 2
  NumberY = 2
  NumberZ = 1
  Placement = pos=(0,0,0) rot=(0,0,1;0.785398rad)
  PlacementList = 4 placements: [(0,-344,11.83),(344,-7.63833e-14,11.83),(4.21278e-14,344,11.83),(-344,7.63833e-14,11.83)]
  RadialDistance = 50
  ScaleList = (4) [(1,1,1),(1,1,1),(1,1,1),(1,1,1)]
  Symmetry = 1
  TangentialDistance = 25
  expr: .Placement.Rotation.Angle = Spreadsheet.StatorMoldHolesSketchAngle
  expr: NumberPolar = Spreadsheet.NumberOfStatorHoles
FEATURE [App::Link] Link003  label="Fastener_Bolt_LargeInner"
  LinkPlacement = pos=(0,309,11.83) rot=(0,0,1;0.523599rad)
  LinkedObject = -> Link001
  Placement = pos=(0,309,11.83) rot=(0,0,1;0.523599rad)
  expr: .Placement.Base.y = Spreadsheet.LengthMiddleHoles
  expr: .Placement.Base.z = Spreadsheet.HexNutThickness
  expr: .Placement.Rotation.Angle = Spreadsheet.BoltAngle
FEATURE [Part::FeaturePython] Array004  label="Bolts_LargeInner"  # Draft array (typed FeaturePython)
  AlwaysSyncPlacement = false
  Angle = 360
  ArrayType = 1
  Axis = (0,0,1)
  Base = -> Link003
  Center = (0,0,0)
  Count = 4
  ExpandArray = false
  Fuse = false
  IntervalAxis = (0,0,0)
  IntervalX = (50,0,0)
  IntervalY = (0,50,0)
  IntervalZ = (0,0,50)
  NumberCircles = 3
  NumberPolar = 4
  NumberX = 2
  NumberY = 2
  NumberZ = 1
  PlacementList = 4 placements: [(0,309,11.83),(-309,6.86118e-14,11.83),(-3.78416e-14,-309,11.83),(309,-6.86118e-14,11.83)]
  RadialDistance = 50
  ScaleList = (4) [(1,1,1),(1,1,1),(1,1,1),(1,1,1)]
  Symmetry = 1
  TangentialDistance = 25
  expr: Angle = Spreadsheet.LargeInnerPolarPatternOverallAngle
  expr: NumberPolar = Spreadsheet.LargeInnerPolarPatternOccurrences
FEATURE [Part::Mirroring] Part__Mirroring  label="Fastener_Bolt_Middle_Mirror"
  Base = (0,0,0)
  Normal = (1,0,0)
  Source = -> Link001
FEATURE [App::Part] Part002  label="Bolts_Middle_Part"
  Group = -> [Part__Mirroring,Link001]
  Origin = -> Origin003
FEATURE [Part::FeaturePython] Array005  label="Bolts_Middle"  # Draft array (typed FeaturePython)
  AlwaysSyncPlacement = false
  Angle = 360
  ArrayType = 1
  Axis = (0,0,1)
  Base = -> Part002
  Center = (0,0,0)
  Count = 4
  ExpandArray = false
  Fuse = false
  IntervalAxis = (0,0,0)
  IntervalX = (50,0,0)
  IntervalY = (0,50,0)
  IntervalZ = (0,0,50)
  NumberCircles = 3
  NumberPolar = 4
  NumberX = 2
  NumberY = 2
  NumberZ = 1
  PlacementList = 4 placements: [(0,0,0),(0,0,0),(0,0,0),(0,0,0)]
  RadialDistance = 50
  ScaleList = (4) [(1,1,1),(1,1,1),(1,1,1),(1,1,1)]
  Symmetry = 1
  TangentialDistance = 25
  expr: NumberPolar = Spreadsheet.NumberOfStatorHoles
FEATURE [App::Part] Part  label="Bolts"
  Group = -> [Link,Array,Link003,Array004,Link002,Array002,Part002,Array005]
  Origin = -> Origin001
FEATURE [App::Link] Link004  label="Fastener_HexNut_Inner"
  LinkPlacement = pos=(0,128.499,0) rot=(0,0,1;0rad)
  LinkedObject = -> <external ../../../Fasteners/Fastener_HexNut_StatorMold.FCStd>#Binder
  Placement = pos=(0,128.499,0) rot=(0,0,1;0rad)
  expr: .Placement.Base.y = Spreadsheet.IslandInnerRadius
FEATURE [Part::FeaturePython] Array006  label="Nuts_Inner"  # Draft array (typed FeaturePython)
  AlwaysSyncPlacement = false
  Angle = 360
  ArrayType = 1
  Axis = (0,0,1)
  Base = -> Link004
  Center = (0,0,0)
  Count = 6
  ExpandArray = false
  Fuse = false
  IntervalAxis = (0,0,0)
  IntervalX = (50,0,0)
  IntervalY = (0,50,0)
  IntervalZ = (0,0,50)
  NumberCircles = 3
  NumberPolar = 6
  NumberX = 2
  NumberY = 2
  NumberZ = 1
  PlacementList = 6 placements: [(0,128.499,0),(-111.284,64.2497,0),(-111.284,-64.2497,0),(-1.57366e-14,-128.499,0),(111.284,-64.2497,0),(111.284,64.2497,0)]
  RadialDistance = 50
  ScaleList = (6) [(1,1,1),(1,1,1),(1,1,1),(1,1,1),(1,1,1),(1,1,1)]
  Symmetry = 1
  TangentialDistance = 25
  expr: NumberPolar = Spreadsheet.StatorMoldIslandNumberOfBolts
FEATURE [App::Link] Link005  label="Fastener_HexNut_LargeInner"
  LinkPlacement = pos=(0,309,0) rot=(0,0,1;0rad)
  LinkedObject = -> Link004
  Placement = pos=(0,309,0) rot=(0,0,1;0rad)
  expr: .Placement.Base.y = Spreadsheet.LengthMiddleHoles
FEATURE [Part::FeaturePython] Array007  label="Nuts_LargeInner"  # Draft array (typed FeaturePython)
  AlwaysSyncPlacement = false
  Angle = 360
  ArrayType = 1
  Axis = (0,0,1)
  Base = -> Link005
  Center = (0,0,0)
  Count = 4
  ExpandArray = false
  Fuse = false
  IntervalAxis = (0,0,0)
  IntervalX = (50,0,0)
  IntervalY = (0,50,0)
  IntervalZ = (0,0,50)
  NumberCircles = 3
  NumberPolar = 4
  NumberX = 2
  NumberY = 2
  NumberZ = 1
  PlacementList = 4 placements: [(0,309,0),(-309,6.86118e-14,0),(-3.78416e-14,-309,0),(309,-6.86118e-14,0)]
  RadialDistance = 50
  ScaleList = (4) [(1,1,1),(1,1,1),(1,1,1),(1,1,1)]
  Symmetry = 1
  TangentialDistance = 25
  expr: Angle = Spreadsheet.LargeInnerPolarPatternOverallAngle
  expr: NumberPolar = Spreadsheet.LargeInnerPolarPatternOccurrences
FEATURE [App::Link] Link006  label="Fastener_HexNut_LargeOuter"
  LinkPlacement = pos=(0,-344,0) rot=(0,0,1;0rad)
  LinkedObject = -> Link005
  Placement = pos=(0,-344,0) rot=(0,0,1;0rad)
  expr: .Placement.Base.y = -Spreadsheet.LargeHoleCircumradius
FEATURE [Part::FeaturePython] Array008  label="Nuts_LargeOuter"  # Draft array (typed FeaturePython)
  AlwaysSyncPlacement = false
  Angle = 360
  ArrayType = 1
  Axis = (0,0,1)
  Base = -> Link006
  Center = (0,0,0)
  Count = 4
  ExpandArray = false
  Fuse = false
  IntervalAxis = (0,0,0)
  IntervalX = (50,0,0)
  IntervalY = (0,50,0)
  IntervalZ = (0,0,50)
  NumberCircles = 3
  NumberPolar = 4
  NumberX = 2
  NumberY = 2
  NumberZ = 1
  Placement = pos=(0,0,0) rot=(0,0,1;0.785398rad)
  PlacementList = 4 placements: [(0,-344,0),(344,-7.63833e-14,0),(4.21278e-14,344,0),(-344,7.63833e-14,0)]
  RadialDistance = 50
  ScaleList = (4) [(1,1,1),(1,1,1),(1,1,1),(1,1,1)]
  Symmetry = 1
  TangentialDistance = 25
  expr: .Placement.Rotation.Angle = Spreadsheet.StatorMoldHolesSketchAngle
  expr: NumberPolar = Spreadsheet.NumberOfStatorHoles
FEATURE [App::Link] Link007  label="Fastener_HexNut_Middle"
  LinkPlacement = pos=(-118.249,-285.479,0) rot=(0,0,1;0rad)
  LinkedObject = -> Link006
  Placement = pos=(-118.249,-285.479,0) rot=(0,0,1;0rad)
  expr: .Placement.Base.x = Spreadsheet.Fastener_Middle_X
  expr: .Placement.Base.y = Spreadsheet.Fastener_Middle_Y
FEATURE [Part::Mirroring] Part__Mirroring001  label="Fastener_HexNut_Middle_Mirror"
  Base = (0,0,0)
  Normal = (1,0,0)
  Source = -> Link007
FEATURE [App::Part] Part003  label="Nuts_Middle_Part"
  Group = -> [Part__Mirroring001,Link007]
  Origin = -> Origin004
FEATURE [Part::FeaturePython] Array009  label="Nuts_Middle"  # Draft array (typed FeaturePython)
  AlwaysSyncPlacement = false
  Angle = 360
  ArrayType = 1
  Axis = (0,0,1)
  Base = -> Part003
  Center = (0,0,0)
  Count = 4
  ExpandArray = false
  Fuse = false
  IntervalAxis = (0,0,0)
  IntervalX = (50,0,0)
  IntervalY = (0,50,0)
  IntervalZ = (0,0,50)
  NumberCircles = 3
  NumberPolar = 4
  NumberX = 2
  NumberY = 2
  NumberZ = 1
  PlacementList = 4 placements: [(0,0,0),(0,0,0),(0,0,0),(0,0,0)]
  RadialDistance = 50
  ScaleList = (4) [(1,1,1),(1,1,1),(1,1,1),(1,1,1)]
  Symmetry = 1
  TangentialDistance = 25
  expr: NumberPolar = Spreadsheet.NumberOfStatorHoles
FEATURE [App::Link] Link008  label="Fastener_HexNut1"
  LinkPlacement = pos=(-397.071,397.071,0) rot=(0,0,1;0rad)
  LinkedObject = -> <external ../../../Fasteners/Fastener_HexNut_StatorMold.FCStd>#Binder
  Placement = pos=(-397.071,397.071,0) rot=(0,0,1;0rad)
  expr: .Placement.Base.x = Spreadsheet.LocatingBolt1X
  expr: .Placement.Base.y = Spreadsheet.LocatingBolt1Y
FEATURE [App::Link] Link009  label="Fastener_HexNut2"
  LinkPlacement = pos=(397.071,397.071,0) rot=(0,0,1;0rad)
  LinkedObject = -> Link008
  Placement = pos=(397.071,397.071,0) rot=(0,0,1;0rad)
  expr: .Placement.Base.x = Spreadsheet.LocatingBolt2X
  expr: .Placement.Base.y = Spreadsheet.LocatingBolt2Y
FEATURE [App::Link] Link010  label="Fastener_HexNut3"
  LinkPlacement = pos=(397.071,-397.071,0) rot=(0,0,1;0rad)
  LinkedObject = -> Link009
  Placement = pos=(397.071,-397.071,0) rot=(0,0,1;0rad)
  expr: .Placement.Base.x = Spreadsheet.LocatingBolt3X
  expr: .Placement.Base.y = Spreadsheet.LocatingBolt3Y
FEATURE [App::Part] Part005  label="Nuts_Locating"
  Group = -> [Link008,Link009,Link010]
  Origin = -> Origin006
FEATURE [App::Part] Part004  label="Nuts"
  Group = -> [Link004,Array006,Link005,Array007,Link006,Array008,Part003,Array009,Part005]
  Origin = -> Origin005
  Placement = pos=(0,0,54.5) rot=(0,0,1;0rad)
  expr: .Placement.Base.z = Spreadsheet.HexNutZ
FEATURE [App::Link] Link011  label="Washer_Locating1"
  LinkPlacement = pos=(-397.071,397.071,0) rot=(0,0,1;0rad)
  LinkedObject = -> <external ../../../Fasteners/Fastener_Washer_StatorMold.FCStd>#Tube
  Placement = pos=(-397.071,397.071,0) rot=(0,0,1;0rad)
  expr: .Placement.Base.x = Spreadsheet.LocatingBolt1X
  expr: .Placement.Base.y = Spreadsheet.LocatingBolt1Y
FEATURE [App::Link] Link012  label="Washer_Locating2"
  LinkPlacement = pos=(397.071,397.071,0) rot=(0,0,1;0rad)
  LinkedObject = -> Link011
  Placement = pos=(397.071,397.071,0) rot=(0,0,1;0rad)
  expr: .Placement.Base.x = Spreadsheet.LocatingBolt2X
  expr: .Placement.Base.y = Spreadsheet.LocatingBolt2Y
FEATURE [App::Link] Link013  label="Washer_Locating3"
  LinkPlacement = pos=(397.071,-397.071,0) rot=(0,0,1;0rad)
  LinkedObject = -> Link012
  Placement = pos=(397.071,-397.071,0) rot=(0,0,1;0rad)
  expr: .Placement.Base.x = Spreadsheet.LocatingBolt3X
  expr: .Placement.Base.y = Spreadsheet.LocatingBolt3Y
FEATURE [App::Part] Part006  label="Washers_Locating"
  Group = -> [Link011,Link012,Link013]
  Origin = -> Origin007
FEATURE [App::Link] Link014  label="Washer_Middle"
  LinkPlacement = pos=(-118.249,-285.479,0) rot=(0,0,1;0rad)
  LinkedObject = -> <external ../../../Fasteners/Fastener_Washer_StatorMold.FCStd>#Tube
  Placement = pos=(-118.249,-285.479,0) rot=(0,0,1;0rad)
  expr: .Placement.Base.x = Spreadsheet.Fastener_Middle_X
  expr: .Placement.Base.y = Spreadsheet.Fastener_Middle_Y
FEATURE [Part::Mirroring] Part__Mirroring002  label="Washer_Middle_Mirror"
  Base = (0,0,0)
  Normal = (1,0,0)
  Source = -> Link014
FEATURE [App::Part] Part008  label="Washers_Middle_Part"
  Group = -> [Link014,Part__Mirroring002]
  Origin = -> Origin009
FEATURE [Part::FeaturePython] Array010  label="Washers_Middle"  # Draft array (typed FeaturePython)
  AlwaysSyncPlacement = false
  Angle = 360
  ArrayType = 1
  Axis = (0,0,1)
  Base = -> Part008
  Center = (0,0,0)
  Count = 4
  ExpandArray = false
  Fuse = false
  IntervalAxis = (0,0,0)
  IntervalX = (50,0,0)
  IntervalY = (0,50,0)
  IntervalZ = (0,0,50)
  NumberCircles = 3
  NumberPolar = 4
  NumberX = 2
  NumberY = 2
  NumberZ = 1
  PlacementList = 4 placements: [(0,0,0),(0,0,0),(0,0,0),(0,0,0)]
  RadialDistance = 50
  ScaleList = (4) [(1,1,1),(1,1,1),(1,1,1),(1,1,1)]
  Symmetry = 1
  TangentialDistance = 25
  expr: NumberPolar = Spreadsheet.NumberOfStatorHoles
FEATURE [App::Link] Link015  label="Washer_LargeInner"
  LinkPlacement = pos=(0,309,0) rot=(0,0,1;0rad)
  LinkedObject = -> <external ../../../Fasteners/Fastener_Washer_StatorMold.FCStd>#Tube
  Placement = pos=(0,309,0) rot=(0,0,1;0rad)
  expr: .Placement.Base.y = Spreadsheet.LengthMiddleHoles
FEATURE [Part::FeaturePython] Array011  label="Washers_LargeInner"  # Draft array (typed FeaturePython)
  AlwaysSyncPlacement = false
  Angle = 360
  ArrayType = 1
  Axis = (0,0,1)
  Base = -> Link015
  Center = (0,0,0)
  Count = 4
  ExpandArray = false
  Fuse = false
  IntervalAxis = (0,0,0)
  IntervalX = (50,0,0)
  IntervalY = (0,50,0)
  IntervalZ = (0,0,50)
  NumberCircles = 3
  NumberPolar = 4
  NumberX = 2
  NumberY = 2
  NumberZ = 1
  PlacementList = 4 placements: [(0,309,0),(-309,6.86118e-14,0),(-3.78416e-14,-309,0),(309,-6.86118e-14,0)]
  RadialDistance = 50
  ScaleList = (4) [(1,1,1),(1,1,1),(1,1,1),(1,1,1)]
  Symmetry = 1
  TangentialDistance = 25
  expr: Angle = Spreadsheet.LargeInnerPolarPatternOverallAngle
  expr: NumberPolar = Spreadsheet.LargeInnerPolarPatternOccurrences
FEATURE [App::Link] Link016  label="Washer_LargeOuter"
  LinkPlacement = pos=(0,-344,0) rot=(0,0,1;0rad)
  LinkedObject = -> <external ../../../Fasteners/Fastener_Washer_StatorMold.FCStd>#Tube
  Placement = pos=(0,-344,0) rot=(0,0,1;0rad)
  expr: .Placement.Base.y = -Spreadsheet.LargeHoleCircumradius
FEATURE [Part::FeaturePython] Array012  label="Washers_LargeOuter"  # Draft array (typed FeaturePython)
  AlwaysSyncPlacement = false
  Angle = 360
  ArrayType = 1
  Axis = (0,0,1)
  Base = -> Link016
  Center = (0,0,0)
  Count = 4
  ExpandArray = false
  Fuse = false
  IntervalAxis = (0,0,0)
  IntervalX = (50,0,0)
  IntervalY = (0,50,0)
  IntervalZ = (0,0,50)
  NumberCircles = 3
  NumberPolar = 4
  NumberX = 2
  NumberY = 2
  NumberZ = 1
  Placement = pos=(0,0,0) rot=(0,0,1;0.785398rad)
  PlacementList = 4 placements: [(0,-344,0),(344,-7.63833e-14,0),(4.21278e-14,344,0),(-344,7.63833e-14,0)]
  RadialDistance = 50
  ScaleList = (4) [(1,1,1),(1,1,1),(1,1,1),(1,1,1)]
  Symmetry = 1
  TangentialDistance = 25
  expr: .Placement.Rotation.Angle = Spreadsheet.StatorMoldHolesSketchAngle
  expr: NumberPolar = Spreadsheet.NumberOfStatorHoles
FEATURE [App::Link] Link017  label="Washer_Inner"
  LinkPlacement = pos=(0,128.499,0) rot=(0,0,1;0rad)
  LinkedObject = -> <external ../../../Fasteners/Fastener_Washer_StatorMold.FCStd>#Tube
  Placement = pos=(0,128.499,0) rot=(0,0,1;0rad)
  expr: .Placement.Base.y = Spreadsheet.IslandInnerRadius
FEATURE [Part::FeaturePython] Array013  label="Washers_Inner"  # Draft array (typed FeaturePython)
  AlwaysSyncPlacement = false
  Angle = 360
  ArrayType = 1
  Axis = (0,0,1)
  Base = -> Link017
  Center = (0,0,0)
  Count = 6
  ExpandArray = false
  Fuse = false
  IntervalAxis = (0,0,0)
  IntervalX = (50,0,0)
  IntervalY = (0,50,0)
  IntervalZ = (0,0,50)
  NumberCircles = 3
  NumberPolar = 6
  NumberX = 2
  NumberY = 2
  NumberZ = 1
  PlacementList = 6 placements: [(0,128.499,0),(-111.284,64.2497,0),(-111.284,-64.2497,0),(-1.57366e-14,-128.499,0),(111.284,-64.2497,0),(111.284,64.2497,0)]
  RadialDistance = 50
  ScaleList = (6) [(1,1,1),(1,1,1),(1,1,1),(1,1,1),(1,1,1),(1,1,1)]
  Symmetry = 1
  TangentialDistance = 25
  expr: NumberPolar = Spreadsheet.StatorMoldIslandNumberOfBolts
FEATURE [App::Part] Part007  label="Washers"
  Group = -> [Link017,Array013,Link015,Array011,Link016,Array012,Part008,Array010,Part006]
  Origin = -> Origin008
  Placement = pos=(0,0,52) rot=(0,0,1;0rad)
  expr: .Placement.Base.z = Spreadsheet.TopOfStatorMold
FEATURE [App::Part] Part001  label="Stator_Mold_BoltHeadLayer_Assembly"
  Group = -> [Binder,Body,Part,Part004,Part007]
  Origin = -> Origin002
---- part Stator_Mold_BoltHeadLayer_Hexagonal.FCStd = doc fcstd_8f4435556e3a ----
FCSTD DOCUMENT  (FreeCAD 1.0R39109 (Git))
Label: Stator_Mold_BoltHeadLayer_Hexagonal
License: All rights reserved
LicenseURL: http://en.wikipedia.org/wiki/All_rights_reserved
objects: App::Link×21, Part::FeaturePython×15, App::Part×6, Sketcher::SketchObject×5, PartDesign::Pocket×5, PartDesign::PolarPattern×5, PartDesign::Plane×1, PartDesign::SubShapeBinder×1, PartDesign::FeatureBase×1, Spreadsheet::Sheet×1, PartDesign::Body×1
note: 40 computed .brp shape members not serialized (recipe doc carries the construction recipe); baked Part::Feature solids carry a one-line shape summary decoded from their .brp
EXTERNAL_REF file=Stator_Mold_Base.FCStd obj=PocketBody
EXTERNAL_REF file=../../../Master_of_Puppets.FCStd obj=Alternator
EXTERNAL_REF file=../../../Master_of_Puppets.FCStd obj=Fastener
EXTERNAL_REF file=../../../Master_of_Puppets.FCStd obj=Spreadsheet
EXTERNAL_REF file=../../../Fasteners/Fastener_Bolt_StatorMold.FCStd obj=Binder
EXTERNAL_REF file=../../../Fasteners/Fastener_HexNut_StatorMold.FCStd obj=Binder
EXTERNAL_REF file=../../../Fasteners/Fastener_Washer_StatorMold.FCStd obj=Tube

FEATURE [PartDesign::Plane] DatumPlane001  label="DatumPlane"
  AttachmentOffset = pos=(0,0,13) rot=(0,0,1;0rad)
  AttachmentSupport = -> [XY_Plane]
  Length = 60
  MapMode = 5
  Placement = pos=(0,0,13) rot=(0,0,1;0rad)
  ResizeMode = 0
  Width = 60
  expr: .AttachmentOffset.Base.z = Spreadsheet.StatorThickness
FEATURE [Sketcher::SketchObject] Sketch006  label="FirstOuterBoltSketch"
  ArcFitTolerance = 0
  AttachmentSupport = -> [DatumPlane001]
  FullyConstrained = true
  MakeInternals = false
  MapMode = 5
  Placement = pos=(0,0,13) rot=(0,0,1;0rad)
  expr: Constraints[48] = Spreadsheet.LengthMiddleHoles
  expr: Constraints[52] = Spreadsheet.Inradius
  sketch-geometry (21):
    g0: LineSegment StartX=-94.545 StartY=-363.237 StartZ=0 EndX=-104.935 EndY=-363.237 EndZ=0
    g1: LineSegment StartX=-104.935 StartY=-363.237 StartZ=0 EndX=-110.13 EndY=-372.235 EndZ=0
    g2: LineSegment StartX=-110.13 StartY=-372.235 StartZ=0 EndX=-104.935 EndY=-381.233 EndZ=0
    g3: LineSegment StartX=-104.935 StartY=-381.233 StartZ=0 EndX=-94.545 EndY=-381.233 EndZ=0
    g4: LineSegment StartX=-94.545 StartY=-381.233 StartZ=0 EndX=-89.35 EndY=-372.235 EndZ=0
    g5: LineSegment StartX=-89.35 StartY=-372.235 StartZ=0 EndX=-94.545 EndY=-363.237 EndZ=0
    g6: Circle [constr] CenterX=-99.74 CenterY=-372.235 CenterZ=0 NormalX=0 NormalY=0 NormalZ=1 AngleXU=0 Radius=10.39
    g7: LineSegment [constr] StartX=-104.935 StartY=-363.237 StartZ=0 EndX=-99.74 EndY=-372.235 EndZ=0
    g8: LineSegment [constr] StartX=-99.74 StartY=-372.235 StartZ=0 EndX=-94.545 EndY=-381.233 EndZ=0
    g9: LineSegment [constr] StartX=-104.935 StartY=-381.233 StartZ=0 EndX=-99.74 EndY=-372.235 EndZ=0
    g10: LineSegment [constr] StartX=-99.74 StartY=-372.235 StartZ=0 EndX=-94.545 EndY=-363.237 EndZ=0
    g11: LineSegment [constr] StartX=-110.13 StartY=-372.235 StartZ=0 EndX=-99.74 EndY=-372.235 EndZ=0
    g12: LineSegment [constr] StartX=-99.74 StartY=-372.235 StartZ=0 EndX=-89.35 EndY=-372.235 EndZ=0
    g13: LineSegment [constr] StartX=214.91 StartY=372.235 StartZ=0 EndX=-214.91 EndY=372.235 EndZ=0
    g14: LineSegment [constr] StartX=-214.91 StartY=372.235 StartZ=0 EndX=-429.82 EndY=5.68e-14 EndZ=0
    g15: LineSegment [constr] StartX=-429.82 StartY=3.35e-14 StartZ=0 EndX=-214.91 EndY=-372.235 EndZ=0
    g16: LineSegment [constr] StartX=-214.91 StartY=-372.235 StartZ=0 EndX=214.91 EndY=-372.235 EndZ=0
    g17: LineSegment [constr] StartX=214.91 StartY=-372.235 StartZ=0 EndX=429.82 EndY=5.68e-14 EndZ=0
    g18: LineSegment [constr] StartX=429.82 StartY=3.35e-14 StartZ=0 EndX=214.91 EndY=372.235 EndZ=0
    g19: Circle [constr] CenterX=0 CenterY=0 CenterZ=0 NormalX=0 NormalY=0 NormalZ=1 AngleXU=0 Radius=429.82
    g20: LineSegment [constr] StartX=0 StartY=0 StartZ=0 EndX=-99.74 EndY=-372.235 EndZ=0
  constraints (51):
    c: Coincident(g0,g1)
    c: Coincident(g1,g2)
    c: Coincident(g2,g3)
    c: Coincident(g3,g4)
    c: Coincident(g4,g5)
    c: Coincident(g5,g0)
    c: PointOnObject(g0,g6)
    c: PointOnObject(g1,g6)
    c: PointOnObject(g2,g6)
    c: PointOnObject(g3,g6)
    c: PointOnObject(g4,g6)
    c: PointOnObject(g5,g6)
    c: Coincident(g0,g7)
    c: Coincident(g7,g6)
    c: Coincident(g7,g8)
    c: Coincident(g8,g3)
    c: Coincident(g2,g9)
    c: Coincident(g9,g7)
    c: Coincident(g9,g10)
    c: Coincident(g10,g0)
    c: Coincident(g1,g11)
    c: Coincident(g11,g7)
    c: Coincident(g11,g12)
    c: Coincident(g12,g4)
    c: Angle(g10,g7) = 1.0472
    c: Angle(g12,g10) = 1.0472
    c: Angle(g8,g12) = 1.0472
    c: Angle(g9,g8) = 1.0472
    c: Angle(g11,g9) = 1.0472
    c: Horizontal(g4,g1)
    c: Coincident(g13,g14)
    c: Coincident(g14,g15)
    c: Coincident(g15,g16)
    c: Coincident(g16,g17)
    c: Coincident(g17,g18)
    c: Coincident(g18,g13)
    c: Equal(g13, g14-g18) x5
    c: PointOnObject(g13,g19)
    c: PointOnObject(g14,g19)
    c: PointOnObject(g15,g19)
    c: PointOnObject(g16,g19)
    c: PointOnObject(g17,g19)
    c: PointOnObject(g18,g19)
    c: Coincident(g19,g-1)
    c: Radius(g19) = 429.82
    c: Horizontal(g14,g17)
    c: Coincident(g20,g-1)
    c: Coincident(g6,g20)
    c: Radius(g6) = 10.39
    c: PointOnObject(g6,g16)
    c: Angle(g-2,g20) = 2.87979
FEATURE [PartDesign::SubShapeBinder] Binder
  BindCopyOnChange = 0
  BindMode = 0
  ClaimChildren = true
  Context = -> Body [Binder.]
  Fuse = false
  MakeFace = true
  OffsetFill = false
  OffsetIntersection = false
  OffsetJoinType = 0
  OffsetOpenResult = false
  PartialLoad = false
  Refine = true
  Relative = true
  Support = -> [<external Stator_Mold_Base.FCStd>#PocketBody]
  _Version = 2
FEATURE [PartDesign::FeatureBase] BaseFeature
  BaseFeature = -> Binder
  Suppressed = false
FEATURE [PartDesign::Pocket] Pocket002  label="FirstOuterBoltPocket"
  BaseFeature = -> BaseFeature
  Direction = (0,0,-1)
  Length = 5
  Length2 = 100
  Profile = -> Sketch006
  Suppressed = false
  Type = 1
FEATURE [Spreadsheet::Sheet] Spreadsheet
  cells = A1='Inputs; A2='Spreadsheet; A3='StatorThickness; A4(StatorThickness)==Master_of_Puppets#Spreadsheet.StatorThickness; A5='Alternator; A6='LengthMiddleHoles; B6='StatorMoldBoltWidthAcrossCorners; C6='IslandInnerRadius; A7(LengthMiddleHoles)==Master_of_Puppets#Alternator.LengthMiddleHoles; B7(StatorMoldBoltWidthAcrossCorners)==Master_of_Puppets#Alternator.StatorMoldBoltWidthAcrossCorners; C7(IslandInnerRadius)==Master_of_Puppets#Alternator.IslandInnerRadius; A8='StatorMoldIslandNumberOfBolts; B8='LineFromBottomRightToBottomLeftCornerSlope; C8='LineFromBottomRightToBottomLeftCornerYIntercept; A9(StatorMoldIslandNumberOfBolts)==Master_of_Puppets#Alternator.StatorMoldIslandNumberOfBolts; B9(LineFromBottomRightToBottomLeftCornerSlope)==Master_of_Puppets#Alternator.LineFromBottomRightToBottomLeftCornerSlope; C9(LineFromBottomRightToBottomLeftCornerYIntercept)==Master_of_Puppets#Alternator.LineFromBottomRightToBottomLeftCornerYIntercept; A10='LocatingBolt1X; B10='LocatingBolt1Y; A11(LocatingBolt1X)==Master_of_Puppets#Alternator.LocatingBolt1X; B11(LocatingBolt1Y)==Master_of_Puppets#Alternator.LocatingBolt1Y; A12='LocatingBolt2X; B12='LocatingBolt2Y; A13(LocatingBolt2X)==Master_of_Puppets#Alternator.LocatingBolt2X; B13(LocatingBolt2Y)==Master_of_Puppets#Alternator.LocatingBolt2Y; A14='LocatingBolt3X; B14='LocatingBolt3Y; A15(LocatingBolt3X)==Master_of_Puppets#Alternator.LocatingBolt3X; B15(LocatingBolt3Y)==Master_of_Puppets#Alternator.LocatingBolt3Y; A16='FirstOuterBoltHolePolarPatternNumberOfOccurrences; B16='FirstOuterBoltHolePolarPatternAngle; A17(FirstOuterBoltHolePolarPatternNumberOfOccurrences)==Master_of_Puppets#Alternator.FirstOuterBoltHolePolarPatternNumberOfOccurrences; B17(FirstOuterBoltHolePolarPatternAngle)==Master_of_Puppets#Alternator.FirstOuterBoltHolePolarPatternAngle; A18='SecondOuterBoltHolePolarPatternNumberOfOccurrences; B18='SecondOuterBoltHolePolarPatternAngle; A19(SecondOuterBoltHolePolarPatternNumberOfOccurrences)==Master_of_Puppets#Alternator.SecondOuterBoltHolePolarPatternNumberOfOccurrences; B19(SecondOuterBoltHolePolarPatternAngle)==Master_of_Puppets#Alternator.SecondOuterBoltHolePolarPatternAngle; A20='Fastener; A21='HexNutThickness; B21='WasherThickness; A22(HexNutThickness)==Master_of_Puppets#Fastener.HexNutThickness; B22(WasherThickness)==Master_of_Puppets#Fastener.WasherThickness; A23='Calculated; A24='Inradius; B24='BoltZ; C24='BoltAngle; A25(Inradius)==StatorMoldBoltWidthAcrossCorners / 2; B25(BoltZ)==HexNutThickness; C25(BoltAngle)=30; A26='OuterBoltSpokeAngle; A27(OuterBoltSpokeAngle)==360 / 6 / 4; A28='OuterBolt1RadiusX; B28='OuterBolt1RadiusY; C28='OuterBolt1RadiusSlope; A29(OuterBolt1RadiusX)==LengthMiddleHoles * cos(OuterBoltSpokeAngle * 17); B29(OuterBolt1RadiusY)==LengthMiddleHoles * sin(OuterBoltSpokeAngle * 17); C29(OuterBolt1RadiusSlope)==OuterBolt1RadiusY / OuterBolt1RadiusX; A30='OuterBolt1X; B30='OuterBolt1Y; A31(OuterBolt1X)==LineFromBottomRightToBottomLeftCornerYIntercept / (OuterBolt1RadiusSlope - LineFromBottomRightToBottomLeftCornerSlope); B31(OuterBolt1Y)==OuterBolt1X * OuterBolt1RadiusSlope; A32='OuterBolt2RadiusX; B32='OuterBolt2RadiusY; C32='OuterBolt2RadiusSlope; A33(OuterBolt2RadiusX)==LengthMiddleHoles * cos(OuterBoltSpokeAngle * 18); B33(OuterBolt2RadiusY)==LengthMiddleHoles * sin(OuterBoltSpokeAngle * 18); C33(OuterBolt2RadiusSlope)==OuterBolt2RadiusY / OuterBolt2RadiusX; A34='OuterBolt2X; B34='OuterBolt2Y; A35(OuterBolt2X)==LineFromBottomRightToBottomLeftCornerYIntercept / (OuterBolt2RadiusSlope - LineFromBottomRightToBottomLeftCornerSlope); B35(OuterBolt2Y)==OuterBolt2X * OuterBolt2RadiusSlope; A36='OuterBolt3RadiusX; B36='OuterBolt3RadiusY; C36='OuterBolt3RadiusSlope; A37(OuterBolt3RadiusX)==LengthMiddleHoles * cos(OuterBoltSpokeAngle * 19); B37(OuterBolt3RadiusY)==LengthMiddleHoles * sin(OuterBoltSpokeAngle * 19); C37(OuterBolt3RadiusSlope)==OuterBolt3RadiusY / OuterBolt3RadiusX; A38='OuterBolt3X; B38='OuterBolt3Y; A39(OuterBolt3X)==LineFromBottomRightToBottomLeftCornerYIntercept / (OuterBolt3RadiusSlope - LineFromBottomRightToBottomLeftCornerSlope); B39(OuterBolt3Y)==OuterBolt3X * OuterBolt3RadiusSlope; A40='TopOfStatorMold; B40='HexNutZ; C40='Duplicated in Stator_Mold_BoltHeadLayer_Circular; A41(TopOfStatorMold)==StatorThickness * 4; B41(HexNutZ)==TopOfStatorMold + WasherThickness
FEATURE [Sketcher::SketchObject] Sketch  label="InnerBoltsSketch"
  ArcFitTolerance = 0
  AttachmentSupport = -> [DatumPlane001]
  FullyConstrained = true
  MakeInternals = false
  MapMode = 5
  Placement = pos=(0,0,13) rot=(0,0,1;0rad)
  expr: Constraints[1] = Spreadsheet.IslandInnerRadius
  expr: Constraints[31] = Spreadsheet.Inradius
  sketch-geometry (14):
    g0: Circle [constr] CenterX=0 CenterY=0 CenterZ=0 NormalX=0 NormalY=0 NormalZ=1 AngleXU=0 Radius=62.3444
    g1: LineSegment StartX=-5.195 StartY=53.3464 StartZ=0 EndX=5.195 EndY=53.3464 EndZ=0
    g2: LineSegment StartX=5.195 StartY=53.3464 StartZ=0 EndX=10.39 EndY=62.3444 EndZ=0
    g3: LineSegment StartX=10.39 StartY=62.3444 StartZ=0 EndX=5.195 EndY=71.3424 EndZ=0
    g4: LineSegment StartX=5.195 StartY=71.3424 StartZ=0 EndX=-5.195 EndY=71.3424 EndZ=0
    g5: LineSegment StartX=-5.195 StartY=71.3424 StartZ=0 EndX=-10.39 EndY=62.3444 EndZ=0
    g6: LineSegment StartX=-10.39 StartY=62.3444 StartZ=0 EndX=-5.195 EndY=53.3464 EndZ=0
    g7: Circle [constr] CenterX=0 CenterY=62.3444 CenterZ=0 NormalX=0 NormalY=0 NormalZ=1 AngleXU=0 Radius=10.39
    g8: LineSegment [constr] StartX=5.195 StartY=71.3424 StartZ=0 EndX=0 EndY=62.3444 EndZ=0
    g9: LineSegment [constr] StartX=0 StartY=62.3444 StartZ=0 EndX=-5.195 EndY=53.3464 EndZ=0
    g10: LineSegment [constr] StartX=5.195 StartY=53.3464 StartZ=0 EndX=0 EndY=62.3444 EndZ=0
    g11: LineSegment [constr] StartX=0 StartY=62.3444 StartZ=0 EndX=-5.195 EndY=71.3424 EndZ=0
    g12: LineSegment [constr] StartX=10.39 StartY=62.3444 StartZ=0 EndX=0 EndY=62.3444 EndZ=0
    g13: LineSegment [constr] StartX=0 StartY=62.3444 StartZ=0 EndX=-10.39 EndY=62.3444 EndZ=0
  constraints (35):
    c: Coincident(g0,g-1)
    c: Radius(g0) = 62.3444
    c: Coincident(g1,g2)
    c: Coincident(g2,g3)
    c: Coincident(g3,g4)
    c: Coincident(g4,g5)
    c: Coincident(g5,g6)
    c: Coincident(g6,g1)
    c: PointOnObject(g1,g7)
    c: PointOnObject(g2,g7)
    c: PointOnObject(g3,g7)
    c: PointOnObject(g4,g7)
    c: PointOnObject(g5,g7)
    c: PointOnObject(g6,g7)
    c: Coincident(g3,g8)
    c: Coincident(g8,g7)
    c: Coincident(g8,g9)
    c: Coincident(g9,g1)
    c: Coincident(g1,g10)
    c: Coincident(g10,g8)
    c: Coincident(g8,g11)
    c: Coincident(g11,g4)
    c: Coincident(g2,g12)
    c: Coincident(g13,g8)
    c: Coincident(g12,g8)
    c: Angle(g11,g13) = 1.0472
    c: Angle(g13,g9) = 1.0472
    c: Angle(g8,g11) = 1.0472
    c: Angle(g12,g8) = 1.0472
    c: Angle(g9,g10) = 1.0472
    c: Horizontal(g2,g5)
    c: Radius(g7) = 10.39
    c: PointOnObject(g7,g0)
    c: PointOnObject(g7,g-2)
    c: Coincident(g13,g5)
FEATURE [Sketcher::SketchObject] Sketch007  label="CornerBoltSketch"
  ArcFitTolerance = 0
  AttachmentSupport = -> [DatumPlane001]
  FullyConstrained = true
  MakeInternals = false
  MapMode = 5
  Placement = pos=(0,0,13) rot=(0,0,1;0rad)
  expr: Constraints[48] = Spreadsheet.LengthMiddleHoles
  expr: Constraints[50] = Spreadsheet.Inradius
  sketch-geometry (20):
    g0: LineSegment StartX=424.625 StartY=-8.998 StartZ=0 EndX=435.015 EndY=-8.998 EndZ=0
    g1: LineSegment StartX=435.015 StartY=-8.998 StartZ=0 EndX=440.21 EndY=5.86e-14 EndZ=0
    g2: LineSegment StartX=440.21 StartY=5.86e-14 StartZ=0 EndX=435.015 EndY=8.998 EndZ=0
    g3: LineSegment StartX=435.015 StartY=8.998 StartZ=0 EndX=424.625 EndY=8.998 EndZ=0
    g4: LineSegment StartX=424.625 StartY=8.998 StartZ=0 EndX=419.43 EndY=5.86e-14 EndZ=0
    g5: LineSegment StartX=419.43 StartY=5.86e-14 StartZ=0 EndX=424.625 EndY=-8.998 EndZ=0
    g6: Circle [constr] CenterX=429.82 CenterY=5.44e-14 CenterZ=0 NormalX=0 NormalY=0 NormalZ=1 AngleXU=0 Radius=10.39
    g7: LineSegment [constr] StartX=435.015 StartY=-8.998 StartZ=0 EndX=429.82 EndY=5.51e-14 EndZ=0
    g8: LineSegment [constr] StartX=429.82 StartY=5.44e-14 StartZ=0 EndX=424.625 EndY=8.998 EndZ=0
    g9: LineSegment [constr] StartX=435.015 StartY=8.998 StartZ=0 EndX=429.82 EndY=5.51e-14 EndZ=0
    g10: LineSegment [constr] StartX=429.82 StartY=5.44e-14 StartZ=0 EndX=424.625 EndY=-8.998 EndZ=0
    g11: LineSegment [constr] StartX=440.21 StartY=5.86e-14 StartZ=0 EndX=429.82 EndY=5.44e-14 EndZ=0
    g12: LineSegment [constr] StartX=429.82 StartY=5.44e-14 StartZ=0 EndX=419.43 EndY=5.86e-14 EndZ=0
    g13: LineSegment [constr] StartX=214.91 StartY=372.235 StartZ=0 EndX=-214.91 EndY=372.235 EndZ=0
    g14: LineSegment [constr] StartX=-214.91 StartY=372.235 StartZ=0 EndX=-429.82 EndY=5.68e-14 EndZ=0
    g15: LineSegment [constr] StartX=-429.82 StartY=5.44e-14 StartZ=0 EndX=-214.91 EndY=-372.235 EndZ=0
    g16: LineSegment [constr] StartX=-214.91 StartY=-372.235 StartZ=0 EndX=214.91 EndY=-372.235 EndZ=0
    g17: LineSegment [constr] StartX=214.91 StartY=-372.235 StartZ=0 EndX=429.82 EndY=5.68e-14 EndZ=0
    g18: LineSegment [constr] StartX=429.82 StartY=5.44e-14 StartZ=0 EndX=214.91 EndY=372.235 EndZ=0
    g19: Circle [constr] CenterX=0 CenterY=0 CenterZ=0 NormalX=0 NormalY=0 NormalZ=1 AngleXU=0 Radius=429.82
  constraints (48):
    c: Coincident(g0,g1)
    c: Coincident(g1,g2)
    c: Coincident(g2,g3)
    c: Coincident(g3,g4)
    c: Coincident(g4,g5)
    c: Coincident(g5,g0)
    c: PointOnObject(g0,g6)
    c: PointOnObject(g1,g6)
    c: PointOnObject(g2,g6)
    c: PointOnObject(g3,g6)
    c: PointOnObject(g4,g6)
    c: PointOnObject(g5,g6)
    c: Coincident(g0,g7)
    c: Coincident(g7,g6)
    c: Coincident(g7,g8)
    c: Coincident(g8,g3)
    c: Coincident(g2,g9)
    c: Coincident(g9,g7)
    c: Coincident(g9,g10)
    c: Coincident(g10,g0)
    c: Coincident(g1,g11)
    c: Coincident(g11,g7)
    c: Coincident(g11,g12)
    c: Coincident(g12,g4)
    c: Angle(g10,g7) = 1.0472
    c: Angle(g12,g10) = 1.0472
    c: Angle(g8,g12) = 1.0472
    c: Angle(g9,g8) = 1.0472
    c: Angle(g11,g9) = 1.0472
    c: Horizontal(g4,g1)
    c: Coincident(g13,g14)
    c: Coincident(g14,g15)
    c: Coincident(g15,g16)
    c: Coincident(g16,g17)
    c: Coincident(g17,g18)
    c: Coincident(g18,g13)
    c: Equal(g13, g14-g18) x5
    c: PointOnObject(g13,g19)
    c: PointOnObject(g14,g19)
    c: PointOnObject(g15,g19)
    c: PointOnObject(g16,g19)
    c: PointOnObject(g17,g19)
    c: PointOnObject(g18,g19)
    c: Coincident(g19,g-1)
    c: Radius(g19) = 429.82
    c: Horizontal(g14,g17)
    c: Radius(g6) = 10.39
    c: Coincident(g6,g17)
FEATURE [App::Link] Link  label="Fastener_Bolt_Inner"
  LinkPlacement = pos=(0,62.3444,0) rot=(0,0,1;0.523599rad)
  LinkedObject = -> <external ../../../Fasteners/Fastener_Bolt_StatorMold.FCStd>#Binder
  Placement = pos=(0,62.3444,0) rot=(0,0,1;0.523599rad)
  Scale = -1
  ScaleVector = (-1,-1,-1)
  expr: .Placement.Base.y = Spreadsheet.IslandInnerRadius
  expr: .Placement.Rotation.Angle = Spreadsheet.BoltAngle
FEATURE [Part::FeaturePython] Array  label="Bolts_Inner"  # Draft array (typed FeaturePython)
  AlwaysSyncPlacement = false
  Angle = 360
  ArrayType = 1
  Axis = (0,0,1)
  Base = -> Link
  Center = (0,0,0)
  Count = 4
  ExpandArray = false
  Fuse = false
  IntervalAxis = (0,0,0)
  IntervalX = (50,0,0)
  IntervalY = (0,50,0)
  IntervalZ = (0,0,50)
  NumberCircles = 3
  NumberPolar = 4
  NumberX = 2
  NumberY = 2
  NumberZ = 1
  PlacementList = 4 placements: [(0,62.3444,0),(-62.3444,1.38432e-14,0),(-7.63499e-15,-62.3444,0),(62.3444,-1.38432e-14,0)]
  RadialDistance = 50
  ScaleList = (4) [(1,1,1),(1,1,1),(1,1,1),(1,1,1)]
  Symmetry = 1
  TangentialDistance = 25
  expr: NumberPolar = Spreadsheet.StatorMoldIslandNumberOfBolts
FEATURE [App::Link] Link001  label="Fastener_Bolt_Outer1"
  LinkPlacement = pos=(-99.74,-372.235,0) rot=(0,0,1;0.523599rad)
  LinkedObject = -> Link
  Placement = pos=(-99.74,-372.235,0) rot=(0,0,1;0.523599rad)
  expr: .Placement.Base.x = Spreadsheet.OuterBolt1X
  expr: .Placement.Base.y = Spreadsheet.OuterBolt1Y
  expr: .Placement.Rotation.Angle = Spreadsheet.BoltAngle
FEATURE [App::Link] Link002  label="Fastener_Bolt_Outer2"
  LinkPlacement = pos=(-6.84e-14,-372.235,0) rot=(0,0,1;0.523599rad)
  LinkedObject = -> Link001
  Placement = pos=(-6.84e-14,-372.235,0) rot=(0,0,1;0.523599rad)
  expr: .Placement.Base.x = Spreadsheet.OuterBolt2X
  expr: .Placement.Base.y = Spreadsheet.OuterBolt2Y
  expr: .Placement.Rotation.Angle = Spreadsheet.BoltAngle
FEATURE [App::Link] Link003  label="Fastener_Bolt_Outer3"
  LinkPlacement = pos=(99.74,-372.235,0) rot=(0,0,1;0.523599rad)
  LinkedObject = -> Link002
  Placement = pos=(99.74,-372.235,0) rot=(0,0,1;0.523599rad)
  expr: .Placement.Base.x = Spreadsheet.OuterBolt3X
  expr: .Placement.Base.y = Spreadsheet.OuterBolt3Y
  expr: .Placement.Rotation.Angle = Spreadsheet.BoltAngle
FEATURE [App::Link] Link004  label="Fastener_Bolt_Corner"
  LinkPlacement = pos=(429.82,0,0) rot=(0,0,1;0.523599rad)
  LinkedObject = -> Link
  Placement = pos=(429.82,0,0) rot=(0,0,1;0.523599rad)
  expr: .Placement.Base.x = Spreadsheet.LengthMiddleHoles
  expr: .Placement.Rotation.Angle = Spreadsheet.BoltAngle
FEATURE [Part::FeaturePython] Array002  label="Bolts_Corner"  # Draft array (typed FeaturePython)
  AlwaysSyncPlacement = false
  Angle = 360
  ArrayType = 1
  Axis = (0,0,1)
  Base = -> Link004
  Center = (0,0,0)
  Count = 6
  ExpandArray = false
  Fuse = false
  IntervalAxis = (0,0,0)
  IntervalX = (50,0,0)
  IntervalY = (0,50,0)
  IntervalZ = (0,0,50)
  NumberCircles = 3
  NumberPolar = 6
  NumberX = 2
  NumberY = 2
  NumberZ = 1
  PlacementList = 6 placements: [(429.82,0,0),(214.91,372.235,0),(-214.91,372.235,0),(-429.82,5.26377e-14,0),(-214.91,-372.235,0),(214.91,-372.235,0)]
  RadialDistance = 50
  ScaleList = (6) [(1,1,1),(1,1,1),(1,1,1),(1,1,1),(1,1,1),(1,1,1)]
  Symmetry = 1
  TangentialDistance = 25
FEATURE [App::Link] Link005  label="Fastener_HexNut"
  LinkPlacement = pos=(0,62.3444,0) rot=(0,0,1;0rad)
  LinkedObject = -> <external ../../../Fasteners/Fastener_HexNut_StatorMold.FCStd>#Binder
  Placement = pos=(0,62.3444,0) rot=(0,0,1;0rad)
  expr: .Placement.Base.y = Spreadsheet.IslandInnerRadius
FEATURE [Part::FeaturePython] Array003  label="Nuts_Inner"  # Draft array (typed FeaturePython)
  AlwaysSyncPlacement = false
  Angle = 360
  ArrayType = 1
  Axis = (0,0,1)
  Base = -> Link005
  Center = (0,0,0)
  Count = 4
  ExpandArray = false
  Fuse = false
  IntervalAxis = (0,0,0)
  IntervalX = (50,0,0)
  IntervalY = (0,50,0)
  IntervalZ = (0,0,50)
  NumberCircles = 3
  NumberPolar = 4
  NumberX = 2
  NumberY = 2
  NumberZ = 1
  PlacementList = 4 placements: [(0,62.3444,0),(-62.3444,1.38432e-14,0),(-7.63499e-15,-62.3444,0),(62.3444,-1.38432e-14,0)]
  RadialDistance = 50
  ScaleList = (4) [(1,1,1),(1,1,1),(1,1,1),(1,1,1)]
  Symmetry = 1
  TangentialDistance = 25
  expr: NumberPolar = Spreadsheet.StatorMoldIslandNumberOfBolts
FEATURE [App::Link] Link006  label="Fastener_HexNut_Outer1"
  LinkPlacement = pos=(-99.74,-372.235,0) rot=(0,0,1;0rad)
  LinkedObject = -> Link005
  Placement = pos=(-99.74,-372.235,0) rot=(0,0,1;0rad)
  expr: .Placement.Base.x = Spreadsheet.OuterBolt1X
  expr: .Placement.Base.y = Spreadsheet.OuterBolt1Y
FEATURE [App::Link] Link007  label="Fastener_HexNut_Outer2"
  LinkPlacement = pos=(-6.84e-14,-372.235,0) rot=(0,0,1;0rad)
  LinkedObject = -> Link006
  Placement = pos=(-6.84e-14,-372.235,0) rot=(0,0,1;0rad)
  expr: .Placement.Base.x = Spreadsheet.OuterBolt2X
  expr: .Placement.Base.y = Spreadsheet.OuterBolt2Y
FEATURE [App::Link] Link008  label="Fastener_HexNut_Outer3"
  LinkPlacement = pos=(99.74,-372.235,0) rot=(0,0,1;0rad)
  LinkedObject = -> Link007
  Placement = pos=(99.74,-372.235,0) rot=(0,0,1;0rad)
  expr: .Placement.Base.x = Spreadsheet.OuterBolt3X
  expr: .Placement.Base.y = Spreadsheet.OuterBolt3Y
FEATURE [App::Link] Link009  label="Fastener_HexNut_Corner"
  LinkPlacement = pos=(429.82,0,0) rot=(0,0,1;0rad)
  LinkedObject = -> Link008
  Placement = pos=(429.82,0,0) rot=(0,0,1;0rad)
  expr: .Placement.Base.x = Spreadsheet.LengthMiddleHoles
FEATURE [Part::FeaturePython] Array005  label="Nuts_Corner"  # Draft array (typed FeaturePython)
  AlwaysSyncPlacement = false
  Angle = 360
  ArrayType = 1
  Axis = (0,0,1)
  Base = -> Link009
  Center = (0,0,0)
  Count = 6
  ExpandArray = false
  Fuse = false
  IntervalAxis = (0,0,0)
  IntervalX = (50,0,0)
  IntervalY = (0,50,0)
  IntervalZ = (0,0,50)
  NumberCircles = 3
  NumberPolar = 6
  NumberX = 2
  NumberY = 2
  NumberZ = 1
  PlacementList = 6 placements: [(429.82,0,0),(214.91,372.235,0),(-214.91,372.235,0),(-429.82,5.26377e-14,0),(-214.91,-372.235,0),(214.91,-372.235,0)]
  RadialDistance = 50
  ScaleList = (6) [(1,1,1),(1,1,1),(1,1,1),(1,1,1),(1,1,1),(1,1,1)]
  Symmetry = 1
  TangentialDistance = 25
FEATURE [App::Link] Link010  label="Fastener_HexNut1"
  LinkPlacement = pos=(-512.897,512.897,0) rot=(0,0,1;0rad)
  LinkedObject = -> <external ../../../Fasteners/Fastener_HexNut_StatorMold.FCStd>#Binder
  Placement = pos=(-512.897,512.897,0) rot=(0,0,1;0rad)
  expr: .Placement.Base.x = Spreadsheet.LocatingBolt1X
  expr: .Placement.Base.y = Spreadsheet.LocatingBolt1Y
FEATURE [App::Link] Link011  label="Fastener_HexNut2"
  LinkPlacement = pos=(512.897,512.897,0) rot=(0,0,1;0rad)
  LinkedObject = -> Link010
  Placement = pos=(512.897,512.897,0) rot=(0,0,1;0rad)
  expr: .Placement.Base.x = Spreadsheet.LocatingBolt2X
  expr: .Placement.Base.y = Spreadsheet.LocatingBolt2Y
FEATURE [App::Link] Link012  label="Fastener_HexNut3"
  LinkPlacement = pos=(512.897,-512.897,0) rot=(0,0,1;0rad)
  LinkedObject = -> Link011
  Placement = pos=(512.897,-512.897,0) rot=(0,0,1;0rad)
  expr: .Placement.Base.x = Spreadsheet.LocatingBolt3X
  expr: .Placement.Base.y = Spreadsheet.LocatingBolt3Y
FEATURE [App::Part] Part006  label="Nuts_Locating"
  Group = -> [Link010,Link011,Link012]
  Origin = -> Origin007
FEATURE [App::Link] Link013  label="Washer_Inner"
  LinkPlacement = pos=(0,62.3444,0) rot=(0,0,1;0rad)
  LinkedObject = -> <external ../../../Fasteners/Fastener_Washer_StatorMold.FCStd>#Tube
  Placement = pos=(0,62.3444,0) rot=(0,0,1;0rad)
  expr: .Placement.Base.y = Spreadsheet.IslandInnerRadius
FEATURE [App::Link] Link014  label="Washer_Outer1"
  LinkPlacement = pos=(-99.74,-372.235,0) rot=(0,0,1;0rad)
  LinkedObject = -> <external ../../../Fasteners/Fastener_Washer_StatorMold.FCStd>#Tube
  Placement = pos=(-99.74,-372.235,0) rot=(0,0,1;0rad)
  expr: .Placement.Base.x = Spreadsheet.OuterBolt1X
  expr: .Placement.Base.y = Spreadsheet.OuterBolt1Y
FEATURE [App::Link] Link015  label="Washer_Outer2"
  LinkPlacement = pos=(-6.84e-14,-372.235,0) rot=(0,0,1;0rad)
  LinkedObject = -> <external ../../../Fasteners/Fastener_Washer_StatorMold.FCStd>#Tube
  Placement = pos=(-6.84e-14,-372.235,0) rot=(0,0,1;0rad)
  expr: .Placement.Base.x = Spreadsheet.OuterBolt2X
  expr: .Placement.Base.y = Spreadsheet.OuterBolt2Y
FEATURE [App::Link] Link016  label="Washer_Outer3"
  LinkPlacement = pos=(99.74,-372.235,0) rot=(0,0,1;0rad)
  LinkedObject = -> <external ../../../Fasteners/Fastener_Washer_StatorMold.FCStd>#Tube
  Placement = pos=(99.74,-372.235,0) rot=(0,0,1;0rad)
  expr: .Placement.Base.x = Spreadsheet.OuterBolt3X
  expr: .Placement.Base.y = Spreadsheet.OuterBolt3Y
FEATURE [App::Link] Link017  label="Washer_Corner"
  LinkPlacement = pos=(429.82,0,0) rot=(0,0,1;0rad)
  LinkedObject = -> <external ../../../Fasteners/Fastener_Washer_StatorMold.FCStd>#Tube
  Placement = pos=(429.82,0,0) rot=(0,0,1;0rad)
  expr: .Placement.Base.x = Spreadsheet.LengthMiddleHoles
FEATURE [App::Link] Link018  label="Washer_Locating1"
  LinkPlacement = pos=(-512.897,512.897,0) rot=(0,0,1;0rad)
  LinkedObject = -> <external ../../../Fasteners/Fastener_Washer_StatorMold.FCStd>#Tube
  Placement = pos=(-512.897,512.897,0) rot=(0,0,1;0rad)
  expr: .Placement.Base.x = Spreadsheet.LocatingBolt1X
  expr: .Placement.Base.y = Spreadsheet.LocatingBolt1Y
FEATURE [App::Link] Link019  label="Washer_Locating2"
  LinkPlacement = pos=(512.897,512.897,0) rot=(0,0,1;0rad)
  LinkedObject = -> <external ../../../Fasteners/Fastener_Washer_StatorMold.FCStd>#Tube
  Placement = pos=(512.897,512.897,0) rot=(0,0,1;0rad)
  expr: .Placement.Base.x = Spreadsheet.LocatingBolt2X
  expr: .Placement.Base.y = Spreadsheet.LocatingBolt2Y
FEATURE [App::Link] Link020  label="Washer_Locating3"
  LinkPlacement = pos=(512.897,-512.897,0) rot=(0,0,1;0rad)
  LinkedObject = -> <external ../../../Fasteners/Fastener_Washer_StatorMold.FCStd>#Tube
  Placement = pos=(512.897,-512.897,0) rot=(0,0,1;0rad)
  expr: .Placement.Base.x = Spreadsheet.LocatingBolt3X
  expr: .Placement.Base.y = Spreadsheet.LocatingBolt3Y
FEATURE [App::Part] Part009  label="Washers_Locating"
  Group = -> [Link018,Link019,Link020]
  Origin = -> Origin010
FEATURE [Part::FeaturePython] Array006  label="Washers_Inner"  # Draft array (typed FeaturePython)
  AlwaysSyncPlacement = false
  Angle = 360
  ArrayType = 1
  Axis = (0,0,1)
  Base = -> Link013
  Center = (0,0,0)
  Count = 4
  ExpandArray = false
  Fuse = false
  IntervalAxis = (0,0,0)
  IntervalX = (50,0,0)
  IntervalY = (0,50,0)
  IntervalZ = (0,0,50)
  NumberCircles = 3
  NumberPolar = 4
  NumberX = 2
  NumberY = 2
  NumberZ = 1
  PlacementList = 4 placements: [(0,62.3444,0),(-62.3444,1.38432e-14,0),(-7.63499e-15,-62.3444,0),(62.3444,-1.38432e-14,0)]
  RadialDistance = 50
  ScaleList = (4) [(1,1,1),(1,1,1),(1,1,1),(1,1,1)]
  Symmetry = 1
  TangentialDistance = 25
  expr: NumberPolar = Spreadsheet.StatorMoldIslandNumberOfBolts
FEATURE [Part::FeaturePython] Array008  label="Washers_Corner"  # Draft array (typed FeaturePython)
  AlwaysSyncPlacement = false
  Angle = 360
  ArrayType = 1
  Axis = (0,0,1)
  Base = -> Link017
  Center = (0,0,0)
  Count = 6
  ExpandArray = false
  Fuse = false
  IntervalAxis = (0,0,0)
  IntervalX = (50,0,0)
  IntervalY = (0,50,0)
  IntervalZ = (0,0,50)
  NumberCircles = 3
  NumberPolar = 6
  NumberX = 2
  NumberY = 2
  NumberZ = 1
  PlacementList = 6 placements: [(429.82,0,0),(214.91,372.235,0),(-214.91,372.235,0),(-429.82,5.26377e-14,0),(-214.91,-372.235,0),(214.91,-372.235,0)]
  RadialDistance = 50
  ScaleList = (6) [(1,1,1),(1,1,1),(1,1,1),(1,1,1),(1,1,1),(1,1,1)]
  Symmetry = 1
  TangentialDistance = 25
FEATURE [Part::FeaturePython] Array009  label="Bolts_Outer1"  # Draft array (typed FeaturePython)
  AlwaysSyncPlacement = false
  Angle = 360
  ArrayType = 1
  Axis = (0,0,1)
  Base = -> Link001
  Center = (0,0,0)
  Count = 6
  ExpandArray = false
  Fuse = false
  IntervalAxis = (0,0,0)
  IntervalX = (50,0,0)
  IntervalY = (0,50,0)
  IntervalZ = (0,0,50)
  NumberCircles = 3
  NumberPolar = 6
  NumberX = 2
  NumberY = 2
  NumberZ = 1
  PlacementList = 6 placements: [(-99.74,-372.235,0),(272.495,-272.495,0),(372.235,99.74,0),(99.74,372.235,0),(-272.495,272.495,0),(-372.235,-99.74,0)]
  RadialDistance = 50
  ScaleList = (6) [(1,1,1),(1,1,1),(1,1,1),(1,1,1),(1,1,1),(1,1,1)]
  Symmetry = 1
  TangentialDistance = 25
  expr: Angle = Spreadsheet.FirstOuterBoltHolePolarPatternAngle
  expr: NumberPolar = Spreadsheet.FirstOuterBoltHolePolarPatternNumberOfOccurrences
FEATURE [Part::FeaturePython] Array010  label="Bolts_Outer2"  # Draft array (typed FeaturePython)
  AlwaysSyncPlacement = false
  Angle = 360
  ArrayType = 1
  Axis = (0,0,1)
  Base = -> Link002
  Center = (0,0,0)
  Count = 6
  ExpandArray = false
  Fuse = false
  IntervalAxis = (0,0,0)
  IntervalX = (50,0,0)
  IntervalY = (0,50,0)
  IntervalZ = (0,0,50)
  NumberCircles = 3
  NumberPolar = 6
  NumberX = 2
  NumberY = 2
  NumberZ = 1
  PlacementList = 6 placements: [(-6.83784e-14,-372.235,0),(322.365,-186.117,0),(322.365,186.117,0),(1.13964e-13,372.235,0),(-322.365,186.117,0),(-322.365,-186.117,0)]
  RadialDistance = 50
  ScaleList = (6) [(1,1,1),(1,1,1),(1,1,1),(1,1,1),(1,1,1),(1,1,1)]
  Symmetry = 1
  TangentialDistance = 25
  expr: Angle = Spreadsheet.SecondOuterBoltHolePolarPatternAngle
  expr: NumberPolar = Spreadsheet.SecondOuterBoltHolePolarPatternNumberOfOccurrences
FEATURE [Part::FeaturePython] Array011  label="Bolts_Outer3"  # Draft array (typed FeaturePython)
  AlwaysSyncPlacement = false
  Angle = 360
  ArrayType = 1
  Axis = (0,0,1)
  Base = -> Link003
  Center = (0,0,0)
  Count = 6
  ExpandArray = false
  Fuse = false
  IntervalAxis = (0,0,0)
  IntervalX = (50,0,0)
  IntervalY = (0,50,0)
  IntervalZ = (0,0,50)
  NumberCircles = 3
  NumberPolar = 6
  NumberX = 2
  NumberY = 2
  NumberZ = 1
  PlacementList = 6 placements: [(99.74,-372.235,0),(372.235,-99.74,0),(272.495,272.495,0),(-99.74,372.235,0),(-372.235,99.74,0),(-272.495,-272.495,0)]
  RadialDistance = 50
  ScaleList = (6) [(1,1,1),(1,1,1),(1,1,1),(1,1,1),(1,1,1),(1,1,1)]
  Symmetry = 1
  TangentialDistance = 25
FEATURE [App::Part] Part001  label="Bolts"
  Group = -> [Link,Array,Link004,Array002,Link001,Link002,Link003,Array009,Array010,Array011]
  Origin = -> Origin002
  Placement = pos=(0,0,11.83) rot=(0,0,1;0rad)
  expr: .Placement.Base.z = Spreadsheet.BoltZ
FEATURE [Part::FeaturePython] Array012  label="Washers_Outer1"  # Draft array (typed FeaturePython)
  AlwaysSyncPlacement = false
  Angle = 360
  ArrayType = 1
  Axis = (0,0,1)
  Base = -> Link014
  Center = (0,0,0)
  Count = 6
  ExpandArray = false
  Fuse = false
  IntervalAxis = (0,0,0)
  IntervalX = (50,0,0)
  IntervalY = (0,50,0)
  IntervalZ = (0,0,50)
  NumberCircles = 3
  NumberPolar = 6
  NumberX = 2
  NumberY = 2
  NumberZ = 1
  PlacementList = 6 placements: [(-99.74,-372.235,0),(272.495,-272.495,0),(372.235,99.74,0),(99.74,372.235,0),(-272.495,272.495,0),(-372.235,-99.74,0)]
  RadialDistance = 50
  ScaleList = (6) [(1,1,1),(1,1,1),(1,1,1),(1,1,1),(1,1,1),(1,1,1)]
  Symmetry = 1
  TangentialDistance = 25
  expr: Angle = Spreadsheet.FirstOuterBoltHolePolarPatternAngle
  expr: NumberPolar = Spreadsheet.FirstOuterBoltHolePolarPatternNumberOfOccurrences
FEATURE [Part::FeaturePython] Array013  label="Washers_Outer2"  # Draft array (typed FeaturePython)
  AlwaysSyncPlacement = false
  Angle = 360
  ArrayType = 1
  Axis = (0,0,1)
  Base = -> Link015
  Center = (0,0,0)
  Count = 6
  ExpandArray = false
  Fuse = false
  IntervalAxis = (0,0,0)
  IntervalX = (50,0,0)
  IntervalY = (0,50,0)
  IntervalZ = (0,0,50)
  NumberCircles = 3
  NumberPolar = 6
  NumberX = 2
  NumberY = 2
  NumberZ = 1
  PlacementList = 6 placements: [(-6.83784e-14,-372.235,0),(322.365,-186.117,0),(322.365,186.117,0),(1.13964e-13,372.235,0),(-322.365,186.117,0),(-322.365,-186.117,0)]
  RadialDistance = 50
  ScaleList = (6) [(1,1,1),(1,1,1),(1,1,1),(1,1,1),(1,1,1),(1,1,1)]
  Symmetry = 1
  TangentialDistance = 25
  expr: Angle = Spreadsheet.SecondOuterBoltHolePolarPatternAngle
  expr: NumberPolar = Spreadsheet.SecondOuterBoltHolePolarPatternNumberOfOccurrences
FEATURE [Part::FeaturePython] Array014  label="Washers_Outer3"  # Draft array (typed FeaturePython)
  AlwaysSyncPlacement = false
  Angle = 360
  ArrayType = 1
  Axis = (0,0,1)
  Base = -> Link016
  Center = (0,0,0)
  Count = 6
  ExpandArray = false
  Fuse = false
  IntervalAxis = (0,0,0)
  IntervalX = (50,0,0)
  IntervalY = (0,50,0)
  IntervalZ = (0,0,50)
  NumberCircles = 3
  NumberPolar = 6
  NumberX = 2
  NumberY = 2
  NumberZ = 1
  PlacementList = 6 placements: [(99.74,-372.235,0),(372.235,-99.74,0),(272.495,272.495,0),(-99.74,372.235,0),(-372.235,99.74,0),(-272.495,-272.495,0)]
  RadialDistance = 50
  ScaleList = (6) [(1,1,1),(1,1,1),(1,1,1),(1,1,1),(1,1,1),(1,1,1)]
  Symmetry = 1
  TangentialDistance = 25
FEATURE [App::Part] Part007  label="Washers"
  Group = -> [Link013,Array006,Link017,Array008,Part009,Link014,Link015,Link016,Array012,Array013,Array014]
  Origin = -> Origin008
  Placement = pos=(0,0,52) rot=(0,0,1;0rad)
  expr: .Placement.Base.z = Spreadsheet.TopOfStatorMold
FEATURE [Part::FeaturePython] Array015  label="Nuts_Outer1"  # Draft array (typed FeaturePython)
  AlwaysSyncPlacement = false
  Angle = 360
  ArrayType = 1
  Axis = (0,0,1)
  Base = -> Link006
  Center = (0,0,0)
  Count = 6
  ExpandArray = false
  Fuse = false
  IntervalAxis = (0,0,0)
  IntervalX = (50,0,0)
  IntervalY = (0,50,0)
  IntervalZ = (0,0,50)
  NumberCircles = 3
  NumberPolar = 6
  NumberX = 2
  NumberY = 2
  NumberZ = 1
  PlacementList = 6 placements: [(-99.74,-372.235,0),(272.495,-272.495,0),(372.235,99.74,0),(99.74,372.235,0),(-272.495,272.495,0),(-372.235,-99.74,0)]
  RadialDistance = 50
  ScaleList = (6) [(1,1,1),(1,1,1),(1,1,1),(1,1,1),(1,1,1),(1,1,1)]
  Symmetry = 1
  TangentialDistance = 25
  expr: Angle = Spreadsheet.FirstOuterBoltHolePolarPatternAngle
  expr: NumberPolar = Spreadsheet.FirstOuterBoltHolePolarPatternNumberOfOccurrences
FEATURE [Part::FeaturePython] Array016  label="Nuts_Outer2"  # Draft array (typed FeaturePython)
  AlwaysSyncPlacement = false
  Angle = 360
  ArrayType = 1
  Axis = (0,0,1)
  Base = -> Link007
  Center = (0,0,0)
  Count = 6
  ExpandArray = false
  Fuse = false
  IntervalAxis = (0,0,0)
  IntervalX = (50,0,0)
  IntervalY = (0,50,0)
  IntervalZ = (0,0,50)
  NumberCircles = 3
  NumberPolar = 6
  NumberX = 2
  NumberY = 2
  NumberZ = 1
  PlacementList = 6 placements: [(-6.83784e-14,-372.235,0),(322.365,-186.117,0),(322.365,186.117,0),(1.13964e-13,372.235,0),(-322.365,186.117,0),(-322.365,-186.117,0)]
  RadialDistance = 50
  ScaleList = (6) [(1,1,1),(1,1,1),(1,1,1),(1,1,1),(1,1,1),(1,1,1)]
  Symmetry = 1
  TangentialDistance = 25
  expr: Angle = Spreadsheet.SecondOuterBoltHolePolarPatternAngle
  expr: NumberPolar = Spreadsheet.SecondOuterBoltHolePolarPatternNumberOfOccurrences
FEATURE [Part::FeaturePython] Array017  label="Nuts_Outer3"  # Draft array (typed FeaturePython)
  AlwaysSyncPlacement = false
  Angle = 360
  ArrayType = 1
  Axis = (0,0,1)
  Base = -> Link008
  Center = (0,0,0)
  Count = 6
  ExpandArray = false
  Fuse = false
  IntervalAxis = (0,0,0)
  IntervalX = (50,0,0)
  IntervalY = (0,50,0)
  IntervalZ = (0,0,50)
  NumberCircles = 3
  NumberPolar = 6
  NumberX = 2
  NumberY = 2
  NumberZ = 1
  PlacementList = 6 placements: [(99.74,-372.235,0),(372.235,-99.74,0),(272.495,272.495,0),(-99.74,372.235,0),(-372.235,99.74,0),(-272.495,-272.495,0)]
  RadialDistance = 50
  ScaleList = (6) [(1,1,1),(1,1,1),(1,1,1),(1,1,1),(1,1,1),(1,1,1)]
  Symmetry = 1
  TangentialDistance = 25
FEATURE [App::Part] Part004  label="Nuts"
  Group = -> [Link005,Array003,Link009,Array005,Part006,Array015,Array016,Array017,Link006,Link007,Link008]
  Origin = -> Origin005
  Placement = pos=(0,0,54.5) rot=(0,0,1;0rad)
  expr: .Placement.Base.z = Spreadsheet.HexNutZ
FEATURE [Sketcher::SketchObject] Sketch008  label="SecondOuterBoltSketch"
  ArcFitTolerance = 0
  AttachmentSupport = -> [DatumPlane001]
  FullyConstrained = true
  MakeInternals = false
  MapMode = 5
  Placement = pos=(0,0,13) rot=(0,0,1;0rad)
  expr: Constraints[48] = Spreadsheet.LengthMiddleHoles
  expr: Constraints[50] = Spreadsheet.Inradius
  sketch-geometry (20):
    g0: LineSegment StartX=5.195 StartY=-363.237 StartZ=0 EndX=-5.195 EndY=-363.237 EndZ=0
    g1: LineSegment StartX=-5.195 StartY=-363.237 StartZ=0 EndX=-10.39 EndY=-372.235 EndZ=0
    g2: LineSegment StartX=-10.39 StartY=-372.235 StartZ=0 EndX=-5.195 EndY=-381.233 EndZ=0
    g3: LineSegment StartX=-5.195 StartY=-381.233 StartZ=0 EndX=5.195 EndY=-381.233 EndZ=0
    g4: LineSegment StartX=5.195 StartY=-381.233 StartZ=0 EndX=10.39 EndY=-372.235 EndZ=0
    g5: LineSegment StartX=10.39 StartY=-372.235 StartZ=0 EndX=5.195 EndY=-363.237 EndZ=0
    g6: Circle [constr] CenterX=0 CenterY=-372.235 CenterZ=0 NormalX=0 NormalY=0 NormalZ=1 AngleXU=0 Radius=10.39
    g7: LineSegment [constr] StartX=-5.195 StartY=-363.237 StartZ=0 EndX=0 EndY=-372.235 EndZ=0
    g8: LineSegment [constr] StartX=0 StartY=-372.235 StartZ=0 EndX=5.195 EndY=-381.233 EndZ=0
    g9: LineSegment [constr] StartX=-5.195 StartY=-381.233 StartZ=0 EndX=0 EndY=-372.235 EndZ=0
    g10: LineSegment [constr] StartX=0 StartY=-372.235 StartZ=0 EndX=5.195 EndY=-363.237 EndZ=0
    g11: LineSegment [constr] StartX=-10.39 StartY=-372.235 StartZ=0 EndX=0 EndY=-372.235 EndZ=0
    g12: LineSegment [constr] StartX=0 StartY=-372.235 StartZ=0 EndX=10.39 EndY=-372.235 EndZ=0
    g13: LineSegment [constr] StartX=214.91 StartY=372.235 StartZ=0 EndX=-214.91 EndY=372.235 EndZ=0
    g14: LineSegment [constr] StartX=-214.91 StartY=372.235 StartZ=0 EndX=-429.82 EndY=0 EndZ=0
    g15: LineSegment [constr] StartX=-429.82 StartY=-1.37e-14 StartZ=0 EndX=-214.91 EndY=-372.235 EndZ=0
    g16: LineSegment [constr] StartX=-214.91 StartY=-372.235 StartZ=0 EndX=214.91 EndY=-372.235 EndZ=0
    g17: LineSegment [constr] StartX=214.91 StartY=-372.235 StartZ=0 EndX=429.82 EndY=0 EndZ=0
    g18: LineSegment [constr] StartX=429.82 StartY=-1.37e-14 StartZ=0 EndX=214.91 EndY=372.235 EndZ=0
    g19: Circle [constr] CenterX=0 CenterY=0 CenterZ=0 NormalX=0 NormalY=0 NormalZ=1 AngleXU=0 Radius=429.82
  constraints (49):
    c: Coincident(g0,g1)
    c: Coincident(g1,g2)
    c: Coincident(g2,g3)
    c: Coincident(g3,g4)
    c: Coincident(g4,g5)
    c: Coincident(g5,g0)
    c: PointOnObject(g0,g6)
    c: PointOnObject(g1,g6)
    c: PointOnObject(g2,g6)
    c: PointOnObject(g3,g6)
    c: PointOnObject(g4,g6)
    c: PointOnObject(g5,g6)
    c: Coincident(g0,g7)
    c: Coincident(g7,g6)
    c: Coincident(g7,g8)
    c: Coincident(g8,g3)
    c: Coincident(g2,g9)
    c: Coincident(g9,g7)
    c: Coincident(g9,g10)
    c: Coincident(g10,g0)
    c: Coincident(g1,g11)
    c: Coincident(g11,g7)
    c: Coincident(g11,g12)
    c: Coincident(g12,g4)
    c: Angle(g10,g7) = 1.0472
    c: Angle(g12,g10) = 1.0472
    c: Angle(g8,g12) = 1.0472
    c: Angle(g9,g8) = 1.0472
    c: Angle(g11,g9) = 1.0472
    c: Horizontal(g4,g1)
    c: Coincident(g13,g14)
    c: Coincident(g14,g15)
    c: Coincident(g15,g16)
    c: Coincident(g16,g17)
    c: Coincident(g17,g18)
    c: Coincident(g18,g13)
    c: Equal(g13, g14-g18) x5
    c: PointOnObject(g13,g19)
    c: PointOnObject(g14,g19)
    c: PointOnObject(g15,g19)
    c: PointOnObject(g16,g19)
    c: PointOnObject(g17,g19)
    c: PointOnObject(g18,g19)
    c: Coincident(g19,g-1)
    c: Radius(g19) = 429.82
    c: Horizontal(g14,g17)
    c: Radius(g6) = 10.39
    c: PointOnObject(g6,g16)
    c: PointOnObject(g6,g-2)
FEATURE [PartDesign::Pocket] Pocket004  label="SecondOuterBoltPocket"
  BaseFeature = -> Pocket002
  Direction = (0,0,-1)
  Length = 5
  Length2 = 5
  Profile = -> Sketch008
  ReferenceAxis = -> Sketch008 [N_Axis]
  Refine = true
  Suppressed = false
  Type = 1
FEATURE [Sketcher::SketchObject] Sketch009  label="ThirdOuterBoltSketch"
  ArcFitTolerance = 0
  AttachmentSupport = -> [DatumPlane001]
  FullyConstrained = true
  MakeInternals = false
  MapMode = 5
  Placement = pos=(0,0,13) rot=(0,0,1;0rad)
  expr: Constraints[48] = Spreadsheet.LengthMiddleHoles
  expr: Constraints[52] = Spreadsheet.Inradius
  sketch-geometry (21):
    g0: LineSegment StartX=104.935 StartY=-363.237 StartZ=0 EndX=94.545 EndY=-363.237 EndZ=0
    g1: LineSegment StartX=94.545 StartY=-363.237 StartZ=0 EndX=89.35 EndY=-372.235 EndZ=0
    g2: LineSegment StartX=89.35 StartY=-372.235 StartZ=0 EndX=94.545 EndY=-381.233 EndZ=0
    g3: LineSegment StartX=94.545 StartY=-381.233 StartZ=0 EndX=104.935 EndY=-381.233 EndZ=0
    g4: LineSegment StartX=104.935 StartY=-381.233 StartZ=0 EndX=110.13 EndY=-372.235 EndZ=0
    g5: LineSegment StartX=110.13 StartY=-372.235 StartZ=0 EndX=104.935 EndY=-363.237 EndZ=0
    g6: Circle [constr] CenterX=99.74 CenterY=-372.235 CenterZ=0 NormalX=0 NormalY=0 NormalZ=1 AngleXU=0 Radius=10.39
    g7: LineSegment [constr] StartX=94.545 StartY=-363.237 StartZ=0 EndX=99.74 EndY=-372.235 EndZ=0
    g8: LineSegment [constr] StartX=99.74 StartY=-372.235 StartZ=0 EndX=104.935 EndY=-381.233 EndZ=0
    g9: LineSegment [constr] StartX=94.545 StartY=-381.233 StartZ=0 EndX=99.74 EndY=-372.235 EndZ=0
    g10: LineSegment [constr] StartX=99.74 StartY=-372.235 StartZ=0 EndX=104.935 EndY=-363.237 EndZ=0
    g11: LineSegment [constr] StartX=89.35 StartY=-372.235 StartZ=0 EndX=99.74 EndY=-372.235 EndZ=0
    g12: LineSegment [constr] StartX=99.74 StartY=-372.235 StartZ=0 EndX=110.13 EndY=-372.235 EndZ=0
    g13: LineSegment [constr] StartX=214.91 StartY=372.235 StartZ=0 EndX=-214.91 EndY=372.235 EndZ=0
    g14: LineSegment [constr] StartX=-214.91 StartY=372.235 StartZ=0 EndX=-429.82 EndY=0 EndZ=0
    g15: LineSegment [constr] StartX=-429.82 StartY=1.18e-14 StartZ=0 EndX=-214.91 EndY=-372.235 EndZ=0
    g16: LineSegment [constr] StartX=-214.91 StartY=-372.235 StartZ=0 EndX=214.91 EndY=-372.235 EndZ=0
    g17: LineSegment [constr] StartX=214.91 StartY=-372.235 StartZ=0 EndX=429.82 EndY=0 EndZ=0
    g18: LineSegment [constr] StartX=429.82 StartY=1.18e-14 StartZ=0 EndX=214.91 EndY=372.235 EndZ=0
    g19: Circle [constr] CenterX=0 CenterY=0 CenterZ=0 NormalX=0 NormalY=0 NormalZ=1 AngleXU=0 Radius=429.82
    g20: LineSegment [constr] StartX=0 StartY=0 StartZ=0 EndX=99.74 EndY=-372.235 EndZ=0
  constraints (51):
    c: Coincident(g0,g1)
    c: Coincident(g1,g2)
    c: Coincident(g2,g3)
    c: Coincident(g3,g4)
    c: Coincident(g4,g5)
    c: Coincident(g5,g0)
    c: PointOnObject(g0,g6)
    c: PointOnObject(g1,g6)
    c: PointOnObject(g2,g6)
    c: PointOnObject(g3,g6)
    c: PointOnObject(g4,g6)
    c: PointOnObject(g5,g6)
    c: Coincident(g0,g7)
    c: Coincident(g7,g6)
    c: Coincident(g7,g8)
    c: Coincident(g8,g3)
    c: Coincident(g2,g9)
    c: Coincident(g9,g7)
    c: Coincident(g9,g10)
    c: Coincident(g10,g0)
    c: Coincident(g1,g11)
    c: Coincident(g11,g7)
    c: Coincident(g11,g12)
    c: Coincident(g12,g4)
    c: Angle(g10,g7) = 1.0472
    c: Angle(g12,g10) = 1.0472
    c: Angle(g8,g12) = 1.0472
    c: Angle(g9,g8) = 1.0472
    c: Angle(g11,g9) = 1.0472
    c: Horizontal(g4,g1)
    c: Coincident(g13,g14)
    c: Coincident(g14,g15)
    c: Coincident(g15,g16)
    c: Coincident(g16,g17)
    c: Coincident(g17,g18)
    c: Coincident(g18,g13)
    c: Equal(g13, g14-g18) x5
    c: PointOnObject(g13,g19)
    c: PointOnObject(g14,g19)
    c: PointOnObject(g15,g19)
    c: PointOnObject(g16,g19)
    c: PointOnObject(g17,g19)
    c: PointOnObject(g18,g19)
    c: Coincident(g19,g-1)
    c: Radius(g19) = 429.82
    c: Horizontal(g14,g17)
    c: Coincident(g20,g-1)
    c: Coincident(g6,g20)
    c: Radius(g6) = 10.39
    c: PointOnObject(g6,g16)
    c: Angle(g-2,g20) = 3.40339
FEATURE [PartDesign::Pocket] Pocket005  label="ThirdOuterBoltPocket"
  BaseFeature = -> Pocket004
  Direction = (0,0,-1)
  Length = 5
  Length2 = 5
  Profile = -> Sketch009
  ReferenceAxis = -> Sketch009 [N_Axis]
  Refine = true
  Suppressed = false
  Type = 1
FEATURE [PartDesign::Pocket] Pocket  label="InnerBoltsPocket"
  BaseFeature = -> Pocket005
  Direction = (0,0,-1)
  Length = 5
  Length2 = 100
  Profile = -> Sketch
  Suppressed = false
  Type = 1
FEATURE [PartDesign::PolarPattern] PolarPattern  label="InnerBoltsPolarPattern"
  Angle = 360
  Axis = -> Z_Axis
  BaseFeature = -> Pocket
  Mode = 0
  Occurrences = 4
  Offset = 120
  Originals = -> [Pocket]
  Suppressed = false
  TransformMode = 0
  expr: Occurrences = Spreadsheet.StatorMoldIslandNumberOfBolts
FEATURE [PartDesign::PolarPattern] PolarPattern001  label="FirstOuterBoltsPolarPattern"
  Angle = 360
  Axis = -> Sketch006 [N_Axis]
  BaseFeature = -> PolarPattern
  Mode = 0
  Occurrences = 6
  Offset = 120
  Originals = -> [Pocket002]
  Suppressed = false
  TransformMode = 0
  expr: Angle = Spreadsheet.FirstOuterBoltHolePolarPatternAngle
  expr: Occurrences = Spreadsheet.FirstOuterBoltHolePolarPatternNumberOfOccurrences
FEATURE [PartDesign::PolarPattern] PolarPattern003  label="SecondOuterBoltsPolarPattern"
  Angle = 360
  Axis = -> Sketch008 [N_Axis]
  BaseFeature = -> PolarPattern001
  Mode = 0
  Occurrences = 6
  Offset = 120
  Originals = -> [Pocket004]
  Refine = true
  Suppressed = false
  TransformMode = 0
  expr: Angle = Spreadsheet.SecondOuterBoltHolePolarPatternAngle
  expr: Occurrences = Spreadsheet.SecondOuterBoltHolePolarPatternNumberOfOccurrences
FEATURE [PartDesign::PolarPattern] PolarPattern004  label="ThirdOuterBoltsPolarPattern"
  Angle = 360
  Axis = -> Sketch009 [N_Axis]
  BaseFeature = -> PolarPattern003
  Mode = 0
  Occurrences = 6
  Offset = 120
  Originals = -> [Pocket005]
  Refine = true
  Suppressed = false
  TransformMode = 0
FEATURE [PartDesign::Pocket] Pocket003  label="CornerBoltPocket"
  BaseFeature = -> PolarPattern004
  Direction = (0,0,-1)
  Length = 5
  Length2 = 100
  Profile = -> Sketch007
  Suppressed = false
  Type = 1
FEATURE [PartDesign::PolarPattern] PolarPattern002  label="CornerBoltPolarPattern"
  Angle = 360
  Axis = -> Sketch007 [N_Axis]
  BaseFeature = -> Pocket003
  Mode = 0
  Occurrences = 6
  Offset = 120
  Originals = -> [Pocket003]
  Suppressed = false
  TransformMode = 0
FEATURE [PartDesign::Body] Body  label="Stator_Mold_BoltHeadLayer"
  AllowCompound = false
  BaseFeature = -> Binder
  Group = -> [BaseFeature,DatumPlane001,Sketch006,Pocket002,Sketch008,Pocket004,Sketch009,Pocket005,Sketch,Pocket,PolarPattern,PolarPattern001,PolarPattern003,PolarPattern004,Sketch007,Pocket003,PolarPattern002]
  Openafpm_Flat = true
  Origin = -> Origin
  Tip = -> PolarPattern002
FEATURE [App::Part] Part002  label="Stator_Mold_BoltHeadLayer_Assembly"
  Group = -> [Binder,Body,Part001,Part004,Part007]
  Origin = -> Origin003
---- part Stator_Mold_BoltShaftLayer_Circular.FCStd = doc fcstd_30cf6a9a04d4 ----
FCSTD DOCUMENT  (FreeCAD 0.21R33771 (Git))
Label: Stator_Mold_BoltShaftLayer_Circular
License: All rights reserved
LicenseURL: http://en.wikipedia.org/wiki/All_rights_reserved
objects: App::Link×7, App::Part×4, Sketcher::SketchObject×2, PartDesign::PolarPattern×2, PartDesign::Pocket×2, Part::FeaturePython×2, Spreadsheet::Sheet×1, PartDesign::Plane×1, PartDesign::Mirrored×1, PartDesign::SubShapeBinder×1, PartDesign::FeatureBase×1, PartDesign::MultiTransform×1, PartDesign::Body×1, Part::Mirroring×1
note: 15 computed .brp shape members not serialized (recipe doc carries the construction recipe); baked Part::Feature solids carry a one-line shape summary decoded from their .brp
EXTERNAL_REF file=../../../Master_of_Puppets.FCStd obj=Alternator
EXTERNAL_REF file=../../../Master_of_Puppets.FCStd obj=Spreadsheet
EXTERNAL_REF file=Stator_Mold_BoltShaftPattern_Circular.FCStd obj=Body
EXTERNAL_REF file=../../../Fasteners/Fastener_WoodScrew_StatorMold.FCStd obj=Part

FEATURE [Spreadsheet::Sheet] Spreadsheet
  cells = A1='Inputs; A2='StatorThickness; B2='NumberOfHoles; C2='EarAngle; A3(StatorThickness)==Master_of_Puppets#Spreadsheet.StatorThickness; B3(NumberOfHoles)==Master_of_Puppets#Alternator.NumberOfStatorHoles; C3(EarAngle)==Master_of_Puppets#Alternator.EarAngle; A4='StatorMoldScrewHoleRadius; B4='EarSize; C4='LengthMiddleHoles; A5(StatorMoldScrewHoleRadius)==Master_of_Puppets#Alternator.StatorMoldScrewHoleRadius; B5(EarSize)==Master_of_Puppets#Alternator.EarSize; C5(LengthMiddleHoles)==Master_of_Puppets#Alternator.LengthMiddleHoles; A6='IslandInnerRadius; B6='LargeHoleAngle; C6='StatorMoldIslandScrewAngle; A7(IslandInnerRadius)==Master_of_Puppets#Alternator.IslandInnerRadius; B7(LargeHoleAngle)==Master_of_Puppets#Alternator.LargeHoleAngle; C7(StatorMoldIslandScrewAngle)==Master_of_Puppets#Alternator.StatorMoldIslandScrewAngle; A8='StatorMoldIslandNumberOfScrewSectors; B8='StatorMoldHolesSketchAngle; C8='StatorMoldIslandNumberOfBolts; A9(StatorMoldIslandNumberOfScrewSectors)==Master_of_Puppets#Alternator.StatorMoldIslandNumberOfScrewSectors; B9(StatorMoldHolesSketchAngle)==Master_of_Puppets#Alternator.StatorMoldHolesSketchAngle; C9(StatorMoldIslandNumberOfBolts)==Master_of_Puppets#Alternator.StatorMoldIslandNumberOfBolts; A10='RotorDiskRadius; B10='StatorMoldIslandNumberOfPolarPatternScrewOccurrences; C10='StatorMoldScrewLength; A11(RotorDiskRadius)==Master_of_Puppets#Spreadsheet.RotorDiskRadius; B11(StatorMoldIslandNumberOfPolarPatternScrewOccurrences)==Master_of_Puppets#Alternator.StatorMoldIslandNumberOfPolarPatternScrewOccurrences; C11(StatorMoldScrewLength)==Master_of_Puppets#Alternator.StatorMoldScrewLength; A12='Calculated; A13='SpokeAngle; B13='ScrewZ; C13='IslandScrewAngleOffset; A14(SpokeAngle)==LargeHoleAngle / 3; B14(ScrewZ)==StatorThickness * 2 - StatorMoldScrewLength; C14(IslandScrewAngleOffset)==90 deg; A15='InnerScrew1X; B15='InnerScrew1Y; A16(InnerScrew1X)==IslandInnerRadius * cos(StatorMoldIslandScrewAngle + IslandScrewAngleOffset); B16(InnerScrew1Y)==IslandInnerRadius * sin(StatorMoldIslandScrewAngle + IslandScrewAngleOffset); A17='InnerScrew2X; B17='InnerScrew2Y; A18(InnerScrew2X)==IslandInnerRadius * cos(StatorMoldIslandScrewAngle * 2 + IslandScrewAngleOffset); B18(InnerScrew2Y)==IslandInnerRadius * sin(StatorMoldIslandScrewAngle * 2 + IslandScrewAngleOffset); A19='Description:; B19='Calculate position of 4 outer screws. From perspective of TOP view going counter clockwise.; A20='OuterScrewBaseAngle; A21(OuterScrewBaseAngle)==270 - EarAngle / 2 + SpokeAngle; A22='OuterScrew1X; B22='OuterScrew1Y; A23(OuterScrew1X)==LengthMiddleHoles * cos(OuterScrewBaseAngle); B23(OuterScrew1Y)==LengthMiddleHoles * sin(OuterScrewBaseAngle); A24='OuterScrew2X; B24='OuterScrew2Y; A25(OuterScrew2X)==LengthMiddleHoles * cos(OuterScrewBaseAngle + SpokeAngle); B25(OuterScrew2Y)==LengthMiddleHoles * sin(OuterScrewBaseAngle + SpokeAngle); A26='Description:; B26='The following equations are to determine the placement of the outer screws by finding the equation of the line tangent to the circle that forms the "ear" and crosses through the point where the bolt is.; A27='BoltAngle; A28(BoltAngle)==270 - EarAngle / 2 + LargeHoleAngle; A29='a = x coordinate of external point; B29='b = y coordinate of external point; C29='r = radius of circle; D29='v = vertical offset of center of circle ; A30='a; B30='b; C30='r; D30='v; A31(a)==LengthMiddleHoles * cos(BoltAngle); B31(b)==LengthMiddleHoles * sin(BoltAngle); C31(r)==EarSize; D31(v)==-LengthMiddleHoles; A32='1) equation for slope of tangent line is derived from plugging in point slope form equation of a line in terms of y into y for equation of circle; B32='2) then the equation is set to the standard form for a quadratic equation (a * x^2 + b * x + c) to determine a, b, and c.; C32='3) once a, b, and c are determined, then we plug it into b^2 - 4*a*c = 0 and solve for m; D32='4) this results in a quadratic equation for m with two solutions, and the negative solution is chosen.; A33='https://www.wolframalpha.com/input?i=x%5E2+%2B+%28mx+-+ma+%2B+b+-+v%29%5E2+%3D+r%5E2; B33=' a = (m^2 + 1), b = (-2*(m^2)*a + 2*b*m - 2*m*v), c = ((a^2)*(m^2) - 2*a*b*m + 2*a*m*v + b^2 - 2*b*v + v^2 - r^2).; C33='https://www.wolframalpha.com/input?i=%28-2*%28m%5E2%29*a+%2B+2*b*m+-+2*m*v%29%5E2+-+4*%28m%5E2+%2B+1%29*%28%28a%5E2%29*%28m%5E2%29+-+2*a*b*m+%2B+2*a*m*v+%2B+b%5E2+-+2*b*v+%2B+v%5E2+-+r%5E2%29+solve+for+m; A34='Equation of tangent line; A35='p (slope); B35='yIntercept; A36(p)==(-sqrt(r ^ 2 * (a ^ 2 + b ^ 2 - 2 * b * v - r ^ 2 + v ^ 2)) + a * b - a * v) / (a ^ 2 - r ^ 2); B36(yIntercept)==b - p * a; A37='Tx; B37='Ty; C37='(T)angent Point Coordinates; A38(Tx)==(-sqrt(-(a ^ 2) * p ^ 2 + 2 * b * (a * p + v) - 2 * a * p * v - b ^ 2 + p ^ 2 * r ^ 2 + r ^ 2 - v ^ 2) + a * p ^ 2 - b * p + p * v) / (p ^ 2 + 1); B38(Ty)==p * Tx + yIntercept; A39='TangentPoint; B39='BoltPoint; C39='Vector; A40(TangentPoint)==create(<<vector>>; Tx; Ty; 0); B40(BoltPoint)==create(<<vector>>; a; b; 0); C40(Vector)==TangentPoint - BoltPoint; A41='DistanceBetweenTangentPointAndBoltPoint; B41='ThirdOfDistance; C41='NormalizedVector; A42(DistanceBetweenTangentPointAndBoltPoint)==.Vector.Length; B42(ThirdOfDistance)==DistanceBetweenTangentPointAndBoltPoint / 3; C42(NormalizedVector)==.Vector / .Vector.Length; A43='Point1; B43='SpokeArcLength; A44(Point1)==TangentPoint - NormalizedVector * SpokeArcLength; B44(SpokeArcLength)==SpokeAngle * pi / 180 * LengthMiddleHoles; A45='Point3Angle; B45='Point3AlongCircle; C45='LineFromOriginToPoint3AlongCircleSlope; A46(Point3Angle)==OuterScrewBaseAngle + SpokeAngle * 3; B46(Point3AlongCircle)==create(<<vector>>; LengthMiddleHoles * cos(Point3Angle); LengthMiddleHoles * sin(Point3Angle); 0); C46(LineFromOriginToPoint3AlongCircleSlope)==.Point3AlongCircle.y / .Point3AlongCircle.x; A47='Intersection between tangent line and line from origin to point 3 along circle.; A48='OuterScrew3X; B48='OuterScrew3Y; C48='OuterScrew3Point; A49(OuterScrew3X)==yIntercept / (LineFromOriginToPoint3AlongCircleSlope - p); B49(OuterScrew3Y)==LineFromOriginToPoint3AlongCircleSlope * OuterScrew3X; C49(OuterScrew3Point)==create(<<vector>>; OuterScrew3X; OuterScrew3Y; 0); A50='Point4Angle; B50='Point4AlongCircle; C50='LineFromOriginToPoint4AlongCircleSlope; A51(Point4Angle)==Point3Angle + SpokeAngle; B51(Point4AlongCircle)==create(<<vector>>; LengthMiddleHoles * cos(Point4Angle); LengthMiddleHoles * sin(Point4Angle); 0); C51(LineFromOriginToPoint4AlongCircleSlope)==.Point4AlongCircle.y / .Point4AlongCircle.x; A52='Intersection between tangent line and line from origin to point 4 along circle.; A53='OuterScrew4X; B53='OuterScrew4Y; C53='OuterScrew4Point; A54(OuterScrew4X)==yIntercept / (LineFromOriginToPoint4AlongCircleSlope - p); B54(OuterScrew4Y)==LineFromOriginToPoint4AlongCircleSlope * OuterScrew4X; C54(OuterScrew4Point)==create(<<vector>>; OuterScrew4X; OuterScrew4Y; 0)
FEATURE [PartDesign::Plane] DatumPlane001  label="DatumPlane"
  AttachmentOffset = pos=(0,0,13) rot=(0,0,1;0rad)
  Length = 849.239
  MapMode = 5
  Placement = pos=(0,0,13) rot=(0,0,1;0rad)
  ResizeMode = 0
  Support = -> [XY_Plane]
  Width = 849.239
  expr: .AttachmentOffset.Base.z = Spreadsheet.StatorThickness
FEATURE [Sketcher::SketchObject] Sketch005  label="OuterScrewsSketch"
  AttachmentOffset = pos=(0,0,0) rot=(0,0,1;0.785398rad)
  FullyConstrained = true
  MapMode = 5
  Placement = pos=(0,0,13) rot=(0,0,1;0.785398rad)
  Support = -> [DatumPlane001]
  expr: .AttachmentOffset.Rotation.Angle = Spreadsheet.StatorMoldHolesSketchAngle
  expr: Constraints[16] = Spreadsheet.EarAngle
  expr: Constraints[21] = Spreadsheet.SpokeAngle
  expr: Constraints[23] = Spreadsheet.StatorMoldScrewHoleRadius
  expr: Constraints[25] = Spreadsheet.SpokeAngle
  expr: Constraints[29] = Spreadsheet.LargeHoleAngle
  expr: Constraints[34] = Spreadsheet.SpokeAngle
  expr: Constraints[38] = Spreadsheet.SpokeAngle
  expr: Constraints[3] = Spreadsheet.LengthMiddleHoles
  expr: Constraints[6] = Spreadsheet.EarSize
  sketch-geometry (18):
    g0: Circle CenterX=0 CenterY=0 CenterZ=0 NormalX=0 NormalY=0 NormalZ=1 AngleXU=0 Radius=252.29
    g1: LineSegment StartX=0 StartY=0 StartZ=0 EndX=0 EndY=-252.29 EndZ=0
    g2: Circle CenterX=0 CenterY=-252.29 CenterZ=0 NormalX=0 NormalY=0 NormalZ=1 AngleXU=0 Radius=35
    g3: LineSegment StartX=17.7851 StartY=-282.434 StartZ=0 EndX=128.2 EndY=-217.29 EndZ=0
    g4: LineSegment StartX=-17.7851 StartY=-282.434 StartZ=0 EndX=-128.2 EndY=-217.29 EndZ=0
    g5: LineSegment StartX=0 StartY=0 StartZ=0 EndX=-178.396 EndY=-178.396 EndZ=0
    g6: LineSegment StartX=0 StartY=0 StartZ=0 EndX=178.396 EndY=-178.396 EndZ=0
    g7: ArcOfCircle CenterX=0 CenterY=0 CenterZ=0 NormalX=0 NormalY=0 NormalZ=1 AngleXU=0 Radius=252.29 StartAngle=3.92699 EndAngle=4.17936
    g8: ArcOfCircle CenterX=0 CenterY=0 CenterZ=0 NormalX=0 NormalY=0 NormalZ=1 AngleXU=0 Radius=252.29 StartAngle=5.24542 EndAngle=5.49779
    g9: LineSegment StartX=0 StartY=0 StartZ=0 EndX=-153.584 EndY=-200.155 EndZ=0
    g10: Circle CenterX=-153.584 CenterY=-200.155 CenterZ=0 NormalX=0 NormalY=0 NormalZ=1 AngleXU=0 Radius=2
    g11: LineSegment StartX=0 StartY=0 StartZ=0 EndX=-126.145 EndY=-218.49 EndZ=0
    g12: Circle CenterX=-126.145 CenterY=-218.49 CenterZ=0 NormalX=0 NormalY=0 NormalZ=1 AngleXU=0 Radius=2
    g13: LineSegment StartX=0 StartY=0 StartZ=0 EndX=-96.5472 EndY=-233.086 EndZ=0
    g14: LineSegment StartX=0 StartY=0 StartZ=0 EndX=-67.7752 EndY=-252.941 EndZ=0
    g15: Circle CenterX=-67.7752 CenterY=-252.941 CenterZ=0 NormalX=0 NormalY=0 NormalZ=1 AngleXU=0 Radius=2
    g16: LineSegment StartX=0 StartY=0 StartZ=0 EndX=-35.7851 EndY=-271.815 EndZ=0
    g17: Circle CenterX=-35.7851 CenterY=-271.815 CenterZ=0 NormalX=0 NormalY=0 NormalZ=1 AngleXU=0 Radius=2
  constraints (44):
    c: Coincident(g0,g-1)
    c: Coincident(g1,g-1)
    c: Vertical(g1)
    c: Radius(g0) = 252.29
    c: Coincident(g2,g1)
    c: Tangent(g3,g0)
    c: Radius(g2) = 35
    c: Symmetric(g6,g5,g1)
    c: Coincident(g7,g5)
    c: Coincident(g7,g4)
    c: Coincident(g8,g6)
    c: Coincident(g8,g3)
    c: Coincident(g6,g5)
    c: Coincident(g5,g7)
    c: Coincident(g5,g-1)
    c: Coincident(g8,g5)
    c: Angle(g5,g6) = 1.5708
    c: Tangent(g3,g2) = -1.5708
    c: Tangent(g4,g0) = 1.5708
    c: Coincident(g9,g5)
    c: PointOnObject(g9,g7)
    c: Angle(g5,g9) = 0.1309
    c: Coincident(g10,g9)
    c: Radius(g10) = 2
    c: Coincident(g11,g-1)
    c: Angle(g9,g11) = 0.1309
    c: PointOnObject(g12,g7)
    c: Coincident(g12,g11)
    c: Coincident(g13,g-1)
    c: Angle(g5,g13) = 0.392699
    c: Tangent(g4,g2) = 1.5708
    c: PointOnObject(g1,g0)
    c: Coincident(g14,g-1)
    c: PointOnObject(g14,g4)
    c: Angle(g13,g14) = 0.1309
    c: Coincident(g15,g14)
    c: Coincident(g16,g-1)
    c: PointOnObject(g16,g4)
    c: Angle(g14,g16) = 0.1309
    c: Coincident(g17,g16)
    c: PointOnObject(g13,g0)
    c: Equal(g17,g15)
    c: Equal(g15,g12)
    c: Equal(g12,g10)
FEATURE [PartDesign::Mirrored] Mirrored  label="OuterScrewsMirrored"
  MirrorPlane = -> Sketch005 [V_Axis]
FEATURE [PartDesign::PolarPattern] PolarPattern002  label="OuterScrewsPolarPattern"
  Angle = 360
  Axis = -> Sketch005 [N_Axis]
  Occurrences = 4
  expr: Occurrences = Spreadsheet.NumberOfHoles
FEATURE [Sketcher::SketchObject] Sketch  label="InnerScrewsSketch"
  FullyConstrained = true
  MapMode = 5
  Placement = pos=(0,0,13) rot=(0,0,1;0rad)
  Support = -> [DatumPlane001]
  expr: Constraints[3] = Spreadsheet.IslandInnerRadius
  expr: Constraints[4] = Spreadsheet.StatorMoldIslandScrewAngle
  expr: Constraints[6] = Spreadsheet.StatorMoldScrewHoleRadius
  sketch-geometry (3):
    g0: Circle CenterX=0 CenterY=0 CenterZ=0 NormalX=0 NormalY=0 NormalZ=1 AngleXU=0 Radius=135.644
    g1: LineSegment StartX=0 StartY=0 StartZ=0 EndX=-46.393 EndY=127.464 EndZ=0
    g2: Circle CenterX=-46.393 CenterY=127.464 CenterZ=0 NormalX=0 NormalY=0 NormalZ=1 AngleXU=0 Radius=2
  constraints (7):
    c: Coincident(g0,g-1)
    c: Coincident(g1,g0)
    c: PointOnObject(g1,g0)
    c: Radius(g0) = 135.644
    c: Angle(g-2,g1) = 0.349066
    c: Coincident(g2,g1)
    c: Radius(g2) = 2
FEATURE [App::Link] Link  label="Stator_Mold_BoltShaftPattern"
  LinkedObject = -> <external Stator_Mold_BoltShaftPattern_Circular.FCStd>#Body
FEATURE [PartDesign::SubShapeBinder] Binder
  BindCopyOnChange = 0
  BindMode = 0
  ClaimChildren = true
  Context = -> Body [Binder.]
  Fuse = false
  MakeFace = true
  OffsetFill = false
  OffsetIntersection = false
  OffsetJoinType = 0
  OffsetOpenResult = false
  PartialLoad = false
  Refine = true
  Relative = true
  Support = -> [Link]
  _Version = 2
FEATURE [PartDesign::FeatureBase] BaseFeature
  BaseFeature = -> Binder
FEATURE [PartDesign::Pocket] Pocket001  label="OuterScrewsPocket"
  BaseFeature = -> BaseFeature
  Direction = (0,0,-1)
  Length = 5
  Length2 = 100
  Profile = -> Sketch005
  Type = 1
FEATURE [PartDesign::MultiTransform] MultiTransform  label="OuterScrewsMultiTransform"
  BaseFeature = -> Pocket001
  Originals = -> [Pocket001]
  Transformations = -> [Mirrored,PolarPattern002]
FEATURE [PartDesign::Pocket] Pocket  label="InnerScrewsPocket"
  BaseFeature = -> MultiTransform
  Direction = (0,0,-1)
  Length = 5
  Length2 = 100
  Profile = -> Sketch
  Type = 1
FEATURE [PartDesign::PolarPattern] PolarPattern  label="InnerScrewsPolarPattern"
  Angle = 360
  Axis = -> Z_Axis
  BaseFeature = -> Pocket
  Occurrences = 18
  Originals = -> [Pocket]
  expr: Occurrences = Spreadsheet.StatorMoldIslandNumberOfScrewSectors
FEATURE [PartDesign::Body] Body  label="Stator_Mold_BoltShaftLayer"
  BaseFeature = -> Binder
  Group = -> [BaseFeature,DatumPlane001,Sketch005,Pocket001,MultiTransform,Mirrored,PolarPattern002,Sketch,Pocket,PolarPattern]
  Openafpm_Flat = true
  Origin = -> Origin
  Tip = -> PolarPattern
FEATURE [App::Link] Link001  label="Fastener_WoodScrew_Inner1"
  LinkPlacement = pos=(-46.393,127.464,0) rot=(0,0,1;0rad)
  LinkedObject = -> <external ../../../Fasteners/Fastener_WoodScrew_StatorMold.FCStd>#Part
  Placement = pos=(-46.393,127.464,0) rot=(0,0,1;0rad)
  expr: .Placement.Base.x = Spreadsheet.InnerScrew1X
  expr: .Placement.Base.y = Spreadsheet.InnerScrew1Y
FEATURE [App::Link] Link002  label="Fastener_WoodScrew_Inner2"
  LinkPlacement = pos=(-87.1904,103.909,0) rot=(0,0,1;0rad)
  LinkedObject = -> Link001
  Placement = pos=(-87.1904,103.909,0) rot=(0,0,1;0rad)
  expr: .Placement.Base.x = Spreadsheet.InnerScrew2X
  expr: .Placement.Base.y = Spreadsheet.InnerScrew2Y
FEATURE [App::Part] Part  label="Inner_Screws_Part"
  Group = -> [Link001,Link002]
  Origin = -> Origin001
FEATURE [Part::FeaturePython] Array  label="IslandScrews"  # Draft array (typed FeaturePython)
  AlwaysSyncPlacement = false
  Angle = 360
  ArrayType = 1
  Axis = (0,0,1)
  Base = -> Part
  Center = (0,0,0)
  Count = 6
  ExpandArray = false
  Fuse = false
  IntervalAxis = (0,0,0)
  IntervalX = (50,0,0)
  IntervalY = (0,50,0)
  IntervalZ = (0,0,50)
  NumberCircles = 3
  NumberPolar = 6
  NumberX = 2
  NumberY = 2
  NumberZ = 1
  Placement = pos=(0,0,1) rot=(0,0,1;0rad)
  PlacementList = 6 placements: [(0,0,0),(0,0,0),(0,0,0),(0,0,0),(0,0,0),(0,0,0)]
  RadialDistance = 50
  ScaleList = (6) [(1,1,1),(1,1,1),(1,1,1),(1,1,1),(1,1,1),(1,1,1)]
  Symmetry = 1
  TangentialDistance = 25
  expr: .Placement.Base.z = Spreadsheet.ScrewZ
  expr: NumberPolar = Spreadsheet.StatorMoldIslandNumberOfPolarPatternScrewOccurrences
FEATURE [App::Link] Link003  label="Fastener_WoodScrew_Outer1"
  AttacherType = Attacher::AttachEngine3D
  LinkPlacement = pos=(-153.584,-200.155,0) rot=(0,0,1;0rad)
  LinkedObject = -> Link001
  Placement = pos=(-153.584,-200.155,0) rot=(0,0,1;0rad)
  expr: .Placement.Base.x = Spreadsheet.OuterScrew1X
  expr: .Placement.Base.y = Spreadsheet.OuterScrew1Y
FEATURE [App::Link] Link004  label="Fastener_WoodScrew_Outer2"
  LinkPlacement = pos=(-126.145,-218.49,0) rot=(0,0,1;0rad)
  LinkedObject = -> Link003
  Placement = pos=(-126.145,-218.49,0) rot=(0,0,1;0rad)
  expr: .Placement.Base.x = Spreadsheet.OuterScrew2X
  expr: .Placement.Base.y = Spreadsheet.OuterScrew2Y
FEATURE [App::Link] Link005  label="Fastener_WoodScrew_Outer3"
  LinkPlacement = pos=(-67.3571,-251.38,0) rot=(0,0,1;0rad)
  LinkedObject = -> Link004
  Placement = pos=(-67.3571,-251.38,0) rot=(0,0,1;0rad)
  expr: .Placement.Base.x = Spreadsheet.OuterScrew3X
  expr: .Placement.Base.y = Spreadsheet.OuterScrew3Y
FEATURE [App::Link] Link006  label="Fastener_WoodScrew_Outer4"
  LinkPlacement = pos=(-35.7064,-271.217,0) rot=(0,0,1;0rad)
  LinkedObject = -> Link005
  Placement = pos=(-35.7064,-271.217,0) rot=(0,0,1;0rad)
  expr: .Placement.Base.x = Spreadsheet.OuterScrew4X
  expr: .Placement.Base.y = Spreadsheet.OuterScrew4Y
FEATURE [App::Part] Part002  label="Screws_Outer_Part"
  Group = -> [Link003,Link004,Link005,Link006]
  Origin = -> Origin003
FEATURE [Part::Mirroring] Part__Mirroring  label="Screws_Outer_Part_Mirror"
  Base = (0,0,0)
  Normal = (1,0,0)
  Source = -> Part002
FEATURE [App::Part] Part003  label="Screws_Outer_Part_Mirror_Part"
  Group = -> [Part002,Part__Mirroring]
  Origin = -> Origin004
FEATURE [Part::FeaturePython] Array001  label="SurroundScrews"  # Draft array (typed FeaturePython)
  AlwaysSyncPlacement = false
  Angle = 360
  ArrayType = 1
  Axis = (0,0,1)
  Base = -> Part003
  Center = (0,0,0)
  Count = 4
  ExpandArray = false
  Fuse = false
  IntervalAxis = (0,0,0)
  IntervalX = (50,0,0)
  IntervalY = (0,50,0)
  IntervalZ = (0,0,50)
  NumberCircles = 3
  NumberPolar = 4
  NumberX = 2
  NumberY = 2
  NumberZ = 1
  Placement = pos=(0,0,1) rot=(0,0,1;0.785398rad)
  PlacementList = 4 placements: [(0,0,0),(0,0,0),(0,0,0),(0,0,0)]
  RadialDistance = 50
  ScaleList = (4) [(1,1,1),(1,1,1),(1,1,1),(1,1,1)]
  Symmetry = 1
  TangentialDistance = 25
  expr: .Placement.Base.z = Spreadsheet.ScrewZ
  expr: .Placement.Rotation.Angle = Spreadsheet.StatorMoldHolesSketchAngle
  expr: NumberPolar = Spreadsheet.NumberOfHoles
FEATURE [App::Part] Part001  label="Stator_Mold_BoltShaftLayer_Assembly"
  Group = -> [Binder,Body,Part,Array,Part003,Array001]
  Origin = -> Origin002
---- part Stator_Mold_BoltShaftLayer_Hexagonal.FCStd = doc fcstd_5827253df706 ----
FCSTD DOCUMENT  (FreeCAD 1.0R39109 (Git))
Label: Stator_Mold_BoltShaftLayer_Hexagonal
License: All rights reserved
LicenseURL: http://en.wikipedia.org/wiki/All_rights_reserved
objects: App::Link×10, App::Part×3, Sketcher::SketchObject×2, PartDesign::Pocket×2, PartDesign::PolarPattern×2, Part::FeaturePython×2, Spreadsheet::Sheet×1, PartDesign::Plane×1, PartDesign::SubShapeBinder×1, PartDesign::FeatureBase×1, PartDesign::Body×1
note: 19 computed .brp shape members not serialized (recipe doc carries the construction recipe); baked Part::Feature solids carry a one-line shape summary decoded from their .brp
EXTERNAL_REF file=../../../Master_of_Puppets.FCStd obj=Alternator
EXTERNAL_REF file=../../../Master_of_Puppets.FCStd obj=Spreadsheet
EXTERNAL_REF file=Stator_Mold_BoltShaftPattern_Hexagonal.FCStd obj=Body
EXTERNAL_REF file=../../../Fasteners/Fastener_WoodScrew_StatorMold.FCStd obj=Part

FEATURE [Spreadsheet::Sheet] Spreadsheet
  cells = A1='Inputs; A2='StatorThickness; B2='NumberOfHoles; C2='EarAngle; A3(StatorThickness)==Master_of_Puppets#Spreadsheet.StatorThickness; B3(NumberOfHoles)==Master_of_Puppets#Alternator.NumberOfStatorHoles; C3(EarAngle)==Master_of_Puppets#Alternator.EarAngle; A4='StatorMoldScrewHoleRadius; B4='EarSize; C4='LengthMiddleHoles; A5(StatorMoldScrewHoleRadius)==Master_of_Puppets#Alternator.StatorMoldScrewHoleRadius; B5(EarSize)==Master_of_Puppets#Alternator.EarSize; C5(LengthMiddleHoles)==Master_of_Puppets#Alternator.LengthMiddleHoles; A6='IslandInnerRadius; B6='LargeHoleAngle; C6='StatorMoldIslandScrewAngle; A7(IslandInnerRadius)==Master_of_Puppets#Alternator.IslandInnerRadius; B7(LargeHoleAngle)==Master_of_Puppets#Alternator.LargeHoleAngle; C7(StatorMoldIslandScrewAngle)==Master_of_Puppets#Alternator.StatorMoldIslandScrewAngle; A8='StatorMoldIslandNumberOfScrewSectors; B8='StatorMoldIslandNumberOfBolts; C8='StatorMoldIslandNumberOfPolarPatternScrewOccurrences; A9(StatorMoldIslandNumberOfScrewSectors)==Master_of_Puppets#Alternator.StatorMoldIslandNumberOfScrewSectors; B9(StatorMoldIslandNumberOfBolts)==Master_of_Puppets#Alternator.StatorMoldIslandNumberOfBolts; C9(StatorMoldIslandNumberOfPolarPatternScrewOccurrences)==Master_of_Puppets#Alternator.StatorMoldIslandNumberOfPolarPatternScrewOccurrences; A10='LineFromBottomRightToBottomLeftCornerSlope; B10='LineFromBottomRightToBottomLeftCornerYIntercept; C10='StatorMoldScrewLength; A11(LineFromBottomRightToBottomLeftCornerSlope)==Master_of_Puppets#Alternator.LineFromBottomRightToBottomLeftCornerSlope; B11(LineFromBottomRightToBottomLeftCornerYIntercept)==Master_of_Puppets#Alternator.LineFromBottomRightToBottomLeftCornerYIntercept; C11(StatorMoldScrewLength)==Master_of_Puppets#Alternator.StatorMoldScrewLength; A12='Calculated; A13='SpokeAngle; B13='ScrewSpokeAngle; C13='ScrewZ; A14(SpokeAngle)==LargeHoleAngle / 3; B14(ScrewSpokeAngle)==60 deg / 12; C14(ScrewZ)==StatorThickness * 2 - StatorMoldScrewLength; A15='InnerScrew1X; B15='InnerScrew1Y; A16(InnerScrew1X)==IslandInnerRadius * cos(StatorMoldIslandScrewAngle * 1); B16(InnerScrew1Y)==IslandInnerRadius * sin(StatorMoldIslandScrewAngle * 1); A17='InnerScrew2X; B17='InnerScrew2Y; A18(InnerScrew2X)==IslandInnerRadius * cos(StatorMoldIslandScrewAngle * 2); B18(InnerScrew2Y)==IslandInnerRadius * sin(StatorMoldIslandScrewAngle * 2); A19='Outer Screws; A20='OuterScrew1RadiusX; B20='OuterScrew1RadiusY; C20='OuterScrew1RadiusSlope; A21(OuterScrew1RadiusX)==LengthMiddleHoles * cos(ScrewSpokeAngle * 13); B21(OuterScrew1RadiusY)==LengthMiddleHoles * sin(ScrewSpokeAngle * 13); C21(OuterScrew1RadiusSlope)==OuterScrew1RadiusY / OuterScrew1RadiusX; A22='OuterScrew1X; B22='OuterScrew1Y; A23(OuterScrew1X)==LineFromBottomRightToBottomLeftCornerYIntercept / (OuterScrew1RadiusSlope - LineFromBottomRightToBottomLeftCornerSlope); B23(OuterScrew1Y)==OuterScrew1X * OuterScrew1RadiusSlope; A24='OuterScrew2RadiusX; B24='OuterScrew2RadiusY; C24='OuterScrew2RadiusSlope; A25(OuterScrew2RadiusX)==LengthMiddleHoles * cos(ScrewSpokeAngle * 14); B25(OuterScrew2RadiusY)==LengthMiddleHoles * sin(ScrewSpokeAngle * 14); C25(OuterScrew2RadiusSlope)==OuterScrew2RadiusY / OuterScrew2RadiusX; A26='OuterScrew2X; B26='OuterScrew2Y; A27(OuterScrew2X)==LineFromBottomRightToBottomLeftCornerYIntercept / (OuterScrew2RadiusSlope - LineFromBottomRightToBottomLeftCornerSlope); B27(OuterScrew2Y)==OuterScrew2X * OuterScrew2RadiusSlope; A28='OuterScrew3RadiusX; B28='OuterScrew3RadiusY; C28='OuterScrew3RadiusSlope; A29(OuterScrew3RadiusX)==LengthMiddleHoles * cos(ScrewSpokeAngle * 16); B29(OuterScrew3RadiusY)==LengthMiddleHoles * sin(ScrewSpokeAngle * 16); C29(OuterScrew3RadiusSlope)==OuterScrew3RadiusY / OuterScrew3RadiusX; A30='OuterScrew3X; B30='OuterScrew3Y; A31(OuterScrew3X)==LineFromBottomRightToBottomLeftCornerYIntercept / (OuterScrew3RadiusSlope - LineFromBottomRightToBottomLeftCornerSlope); B31(OuterScrew3Y)==OuterScrew3X * OuterScrew3RadiusSlope; A32='OuterScrew4RadiusX; B32='OuterScrew4RadiusY; C32='OuterScrew4RadiusSlope; A33(OuterScrew4RadiusX)==LengthMiddleHoles * cos(ScrewSpokeAngle * 17); B33(OuterScrew4RadiusY)==LengthMiddleHoles * sin(ScrewSpokeAngle * 17); C33(OuterScrew4RadiusSlope)==OuterScrew4RadiusY / OuterScrew4RadiusX; A34='OuterScrew4X; B34='OuterScrew4Y; A35(OuterScrew4X)==LineFromBottomRightToBottomLeftCornerYIntercept / (OuterScrew4RadiusSlope - LineFromBottomRightToBottomLeftCornerSlope); B35(OuterScrew4Y)==OuterScrew4X * OuterScrew4RadiusSlope; A36='OuterScrew5RadiusX; B36='OuterScrew5RadiusY; C36='OuterScrew5RadiusSlope; A37(OuterScrew5RadiusX)==LengthMiddleHoles * cos(ScrewSpokeAngle * 19); B37(OuterScrew5RadiusY)==LengthMiddleHoles * sin(ScrewSpokeAngle * 19); C37(OuterScrew5RadiusSlope)==OuterScrew5RadiusY / OuterScrew5RadiusX; A38='OuterScrew5X; B38='OuterScrew5Y; A39(OuterScrew5X)==LineFromBottomRightToBottomLeftCornerYIntercept / (OuterScrew5RadiusSlope - LineFromBottomRightToBottomLeftCornerSlope); B39(OuterScrew5Y)==OuterScrew5X * OuterScrew5RadiusSlope; A40='OuterScrew6RadiusX; B40='OuterScrew6RadiusY; C40='OuterScrew6RadiusSlope; A41(OuterScrew6RadiusX)==LengthMiddleHoles * cos(ScrewSpokeAngle * 20); B41(OuterScrew6RadiusY)==LengthMiddleHoles * sin(ScrewSpokeAngle * 20); C41(OuterScrew6RadiusSlope)==OuterScrew6RadiusY / OuterScrew6RadiusX; A42='OuterScrew6X; B42='OuterScrew6Y; A43(OuterScrew6X)==LineFromBottomRightToBottomLeftCornerYIntercept / (OuterScrew6RadiusSlope - LineFromBottomRightToBottomLeftCornerSlope); B43(OuterScrew6Y)==OuterScrew6X * OuterScrew6RadiusSlope; A44='OuterScrew7RadiusX; B44='OuterScrew7RadiusY; C44='OuterScrew7RadiusSlope; A45(OuterScrew7RadiusX)==LengthMiddleHoles * cos(ScrewSpokeAngle * 22); B45(OuterScrew7RadiusY)==LengthMiddleHoles * sin(ScrewSpokeAngle * 22); C45(OuterScrew7RadiusSlope)==OuterScrew7RadiusY / OuterScrew7RadiusX; A46='OuterScrew7X; B46='OuterScrew7Y; A47(OuterScrew7X)==LineFromBottomRightToBottomLeftCornerYIntercept / (OuterScrew7RadiusSlope - LineFromBottomRightToBottomLeftCornerSlope); B47(OuterScrew7Y)==OuterScrew7X * OuterScrew7RadiusSlope; A48='OuterScrew8RadiusX; B48='OuterScrew8RadiusY; C48='OuterScrew8RadiusSlope; A49(OuterScrew8RadiusX)==LengthMiddleHoles * cos(ScrewSpokeAngle * 23); B49(OuterScrew8RadiusY)==LengthMiddleHoles * sin(ScrewSpokeAngle * 23); C49(OuterScrew8RadiusSlope)==OuterScrew8RadiusY / OuterScrew8RadiusX; A50='OuterScrew8X; B50='OuterScrew8Y; A51(OuterScrew8X)==LineFromBottomRightToBottomLeftCornerYIntercept / (OuterScrew8RadiusSlope - LineFromBottomRightToBottomLeftCornerSlope); B51(OuterScrew8Y)==OuterScrew8X * OuterScrew8RadiusSlope
FEATURE [PartDesign::Plane] DatumPlane001  label="DatumPlane"
  AttachmentOffset = pos=(0,0,15) rot=(0,0,1;0rad)
  AttachmentSupport = -> [XY_Plane]
  Length = 1661.71
  MapMode = 5
  Placement = pos=(0,0,15) rot=(0,0,1;0rad)
  ResizeMode = 0
  Width = 1661.71
  expr: .AttachmentOffset.Base.z = Spreadsheet.StatorThickness
FEATURE [Sketcher::SketchObject] Sketch  label="InnerScrewHolesSketch"
  ArcFitTolerance = 0
  AttachmentSupport = -> [DatumPlane001]
  FullyConstrained = true
  MakeInternals = false
  MapMode = 5
  Placement = pos=(0,0,15) rot=(0,0,1;0rad)
  expr: Constraints[3] = Spreadsheet.IslandInnerRadius
  expr: Constraints[4] = Spreadsheet.StatorMoldIslandScrewAngle
  expr: Constraints[6] = Spreadsheet.StatorMoldScrewHoleRadius
  sketch-geometry (3):
    g0: Circle [constr] CenterX=0 CenterY=0 CenterZ=0 NormalX=0 NormalY=0 NormalZ=1 AngleXU=0 Radius=264.865
    g1: LineSegment [constr] StartX=0 StartY=0 StartZ=0 EndX=-45.9933 EndY=260.841 EndZ=0
    g2: Circle CenterX=-45.9933 CenterY=260.841 CenterZ=0 NormalX=0 NormalY=0 NormalZ=1 AngleXU=0 Radius=2
  constraints (7):
    c: Coincident(g0,g-1)
    c: Coincident(g1,g0)
    c: PointOnObject(g1,g0)
    c: Radius(g0) = 264.865
    c: Angle(g-2,g1) = 0.174533
    c: Coincident(g2,g1)
    c: Radius(g2) = 2
FEATURE [PartDesign::SubShapeBinder] Binder
  BindCopyOnChange = 0
  BindMode = 0
  ClaimChildren = true
  Context = -> Part003 [Binder.]
  Fuse = false
  MakeFace = true
  OffsetFill = false
  OffsetIntersection = false
  OffsetJoinType = 0
  OffsetOpenResult = false
  PartialLoad = false
  Refine = true
  Relative = true
  Support = -> [<external Stator_Mold_BoltShaftPattern_Hexagonal.FCStd>#Body]
  _Version = 2
FEATURE [PartDesign::FeatureBase] BaseFeature
  BaseFeature = -> Binder
  Suppressed = false
FEATURE [PartDesign::Pocket] Pocket  label="InnerScrewHolesPocket"
  BaseFeature = -> BaseFeature
  Direction = (0,0,-1)
  Length = 5
  Length2 = 100
  Profile = -> Sketch
  Suppressed = false
  Type = 1
FEATURE [PartDesign::PolarPattern] PolarPattern  label="InnerScrewHolesPolarPattern"
  Angle = 360
  Axis = -> Z_Axis
  BaseFeature = -> Pocket
  Mode = 0
  Occurrences = 36
  Offset = 120
  Originals = -> [Pocket]
  Suppressed = false
  TransformMode = 0
  expr: Occurrences = Spreadsheet.StatorMoldIslandNumberOfScrewSectors
FEATURE [Sketcher::SketchObject] Sketch001  label="OuterScrewsSketch"
  ArcFitTolerance = 0
  AttachmentSupport = -> [DatumPlane001]
  FullyConstrained = true
  MakeInternals = false
  MapMode = 5
  Placement = pos=(0,0,15) rot=(0,0,1;0rad)
  expr: Constraints[19] = Spreadsheet.LengthMiddleHoles
  expr: Constraints[52] = Spreadsheet.StatorMoldScrewHoleRadius
  sketch-geometry (23):
    g0: LineSegment [constr] StartX=257.01 StartY=445.155 StartZ=0 EndX=-257.01 EndY=445.155 EndZ=0
    g1: LineSegment [constr] StartX=-257.01 StartY=445.155 StartZ=0 EndX=-514.02 EndY=5.68e-14 EndZ=0
    g2: LineSegment [constr] StartX=-514.02 StartY=5.68e-14 StartZ=0 EndX=-257.01 EndY=-445.155 EndZ=0
    g3: LineSegment [constr] StartX=-257.01 StartY=-445.155 StartZ=0 EndX=257.01 EndY=-445.155 EndZ=0
    g4: LineSegment [constr] StartX=257.01 StartY=-445.155 StartZ=0 EndX=514.02 EndY=5.68e-14 EndZ=0
    g5: LineSegment [constr] StartX=514.02 StartY=5.68e-14 StartZ=0 EndX=257.01 EndY=445.155 EndZ=0
    g6: Circle [constr] CenterX=0 CenterY=0 CenterZ=0 NormalX=0 NormalY=0 NormalZ=1 AngleXU=0 Radius=514.02
    g7: LineSegment [constr] StartX=0 StartY=0 StartZ=0 EndX=424.762 EndY=154.601 EndZ=0
    g8: LineSegment [constr] StartX=0 StartY=0 StartZ=0 EndX=404.988 EndY=188.849 EndZ=0
    g9: LineSegment [constr] StartX=0 StartY=0 StartZ=0 EndX=366.042 EndY=256.306 EndZ=0
    g10: LineSegment [constr] StartX=0 StartY=0 StartZ=0 EndX=346.269 EndY=290.554 EndZ=0
    g11: Circle CenterX=424.762 CenterY=154.601 CenterZ=0 NormalX=0 NormalY=0 NormalZ=1 AngleXU=0 Radius=2
    g12: Circle CenterX=404.988 CenterY=188.849 CenterZ=0 NormalX=0 NormalY=0 NormalZ=1 AngleXU=0 Radius=2
    g13: Circle CenterX=366.042 CenterY=256.306 CenterZ=0 NormalX=0 NormalY=0 NormalZ=1 AngleXU=0 Radius=2
    g14: Circle CenterX=346.269 CenterY=290.554 CenterZ=0 NormalX=0 NormalY=0 NormalZ=1 AngleXU=0 Radius=2
    g15: LineSegment [constr] StartX=0 StartY=0 StartZ=0 EndX=304.504 EndY=362.893 EndZ=0
    g16: LineSegment [constr] StartX=0 StartY=0 StartZ=0 EndX=281.726 EndY=402.346 EndZ=0
    g17: Circle CenterX=304.504 CenterY=362.893 CenterZ=0 NormalX=0 NormalY=0 NormalZ=1 AngleXU=0 Radius=2
    g18: Circle CenterX=281.726 CenterY=402.346 CenterZ=0 NormalX=0 NormalY=0 NormalZ=1 AngleXU=0 Radius=2
    g19: LineSegment [constr] StartX=0 StartY=0 StartZ=0 EndX=489.305 EndY=42.8086 EndZ=0
    g20: Circle CenterX=489.305 CenterY=42.8086 CenterZ=0 NormalX=0 NormalY=0 NormalZ=1 AngleXU=0 Radius=2
    g21: LineSegment [constr] StartX=0 StartY=0 StartZ=0 EndX=466.527 EndY=82.2612 EndZ=0
    g22: Circle CenterX=466.527 CenterY=82.2612 CenterZ=0 NormalX=0 NormalY=0 NormalZ=1 AngleXU=0 Radius=2
  constraints (56):
    c: Coincident(g0,g1)
    c: Coincident(g1,g2)
    c: Coincident(g2,g3)
    c: Coincident(g3,g4)
    c: Coincident(g4,g5)
    c: Coincident(g5,g0)
    c: Equal(g0, g1-g5) x5
    c: PointOnObject(g0,g6)
    c: PointOnObject(g1,g6)
    c: PointOnObject(g2,g6)
    c: PointOnObject(g3,g6)
    c: PointOnObject(g4,g6)
    c: PointOnObject(g5,g6)
    c: Coincident(g6,g-1)
    c: Horizontal(g1,g4)
    c: Radius(g6) = 514.02
    c: Coincident(g19,g-1)
    c: Coincident(g21,g-1)
    c: Coincident(g7,g-1)
    c: PointOnObject(g7,g5)
    c: PointOnObject(g8,g5)
    c: Coincident(g9,g8)
    c: PointOnObject(g9,g5)
    c: Coincident(g10,g8)
    c: PointOnObject(g10,g5)
    c: Angle(g7,g8) = 0.0872665
    c: Angle(g8,g9) = 0.174533
    c: Angle(g9,g10) = 0.0872665
    c: Coincident(g8,g-1)
    c: Coincident(g11,g7)
    c: Coincident(g12,g8)
    c: Coincident(g13,g9)
    c: Coincident(g14,g10)
    c: Equal(g11,g12)
    c: Equal(g12,g13)
    c: Equal(g13,g14)
    c: Coincident(g15,g-1)
    c: PointOnObject(g15,g5)
    c: Coincident(g16,g15)
    c: PointOnObject(g16,g5)
    c: Angle(g10,g15) = 0.174533
    c: Coincident(g17,g15)
    c: Equal(g17,g14)
    c: Coincident(g18,g16)
    c: Equal(g18,g17)
    c: Angle(g15,g16) = 0.0872665
    c: PointOnObject(g19,g5)
    c: Coincident(g20,g19)
    c: Radius(g20) = 2
    c: PointOnObject(g21,g5)
    c: Coincident(g22,g21)
    c: Equal(g22,g20)
    c: Angle(g21,g7) = 0.174533
    c: Equal(g12,g20)
    c: Angle(g-1,g19) = 0.0872665
    c: Angle(g19,g21) = 0.0872665
FEATURE [PartDesign::Pocket] Pocket001  label="OuterScrewsPocket"
  BaseFeature = -> PolarPattern
  Direction = (0,0,-1)
  Length = 5
  Length2 = 100
  Profile = -> Sketch001
  Suppressed = false
  Type = 1
FEATURE [PartDesign::PolarPattern] PolarPattern001  label="OuterScrewsPolarPattern"
  Angle = 360
  Axis = -> Sketch001 [N_Axis]
  BaseFeature = -> Pocket001
  Mode = 0
  Occurrences = 6
  Offset = 120
  Originals = -> [Pocket001]
  Suppressed = false
  TransformMode = 0
FEATURE [PartDesign::Body] Body  label="Stator_Mold_BoltShaftLayer"
  AllowCompound = false
  BaseFeature = -> Binder
  Group = -> [BaseFeature,DatumPlane001,Sketch,Pocket,PolarPattern,Sketch001,Pocket001,PolarPattern001]
  Openafpm_Flat = true
  Origin = -> Origin
  Tip = -> PolarPattern001
FEATURE [App::Link] Link  label="Fastener_WoodScrew_Inner1"
  LinkPlacement = pos=(260.841,45.9933,0) rot=(0,0,1;0rad)
  LinkedObject = -> <external ../../../Fasteners/Fastener_WoodScrew_StatorMold.FCStd>#Part
  Placement = pos=(260.841,45.9933,0) rot=(0,0,1;0rad)
  expr: .Placement.Base.x = Spreadsheet.InnerScrew1X
  expr: .Placement.Base.y = Spreadsheet.InnerScrew1Y
FEATURE [App::Link] Link001  label="Fastener_WoodScrew_Inner2"
  LinkPlacement = pos=(248.892,90.5892,0) rot=(0,0,1;0rad)
  LinkedObject = -> Link
  Placement = pos=(248.892,90.5892,0) rot=(0,0,1;0rad)
  expr: .Placement.Base.x = Spreadsheet.InnerScrew2X
  expr: .Placement.Base.y = Spreadsheet.InnerScrew2Y
FEATURE [App::Part] Part  label="Inner_Screws_Part"
  Group = -> [Link,Link001]
  Origin = -> Origin001
FEATURE [Part::FeaturePython] Array  label="IslandScrews"  # Draft array (typed FeaturePython)
  AlwaysSyncPlacement = false
  Angle = 360
  ArrayType = 1
  Axis = (0,0,1)
  Base = -> Part
  Center = (0,0,0)
  Count = 12
  ExpandArray = false
  Fuse = false
  IntervalAxis = (0,0,0)
  IntervalX = (50,0,0)
  IntervalY = (0,50,0)
  IntervalZ = (0,0,50)
  NumberCircles = 3
  NumberPolar = 12
  NumberX = 2
  NumberY = 2
  NumberZ = 1
  PlacementList = 12 placements: [(0,0,0),(0,0,0),(0,0,0),(0,0,0),(0,0,0),(0,0,0),(0,0,0),(0,0,0),(0,0,0),(0,0,0),(0,0,0),(0,0,0)]
  RadialDistance = 50
  ScaleList = (12) [(1,1,1),(1,1,1),(1,1,1),(1,1,1),(1,1,1),(1,1,1),(1,1,1),(1,1,1),(1,1,1),(1,1,1),(1,1,1),(1,1,1)]
  Symmetry = 1
  TangentialDistance = 25
  expr: .Placement.Base.z = Spreadsheet.ScrewZ
  expr: NumberPolar = Spreadsheet.StatorMoldIslandNumberOfPolarPatternScrewOccurrences
FEATURE [App::Link] Link002  label="Fastener_WoodScrew_Outer1"
  LinkPlacement = pos=(-207.579,-445.155,0) rot=(0,0,1;0rad)
  LinkedObject = -> Link
  Placement = pos=(-207.579,-445.155,0) rot=(0,0,1;0rad)
  expr: .Placement.Base.x = Spreadsheet.OuterScrew1X
  expr: .Placement.Base.y = Spreadsheet.OuterScrew1Y
FEATURE [App::Link] Link003  label="Fastener_WoodScrew_Outer2"
  LinkPlacement = pos=(-162.023,-445.155,0) rot=(0,0,1;0rad)
  LinkedObject = -> Link002
  Placement = pos=(-162.023,-445.155,0) rot=(0,0,1;0rad)
  expr: .Placement.Base.x = Spreadsheet.OuterScrew2X
  expr: .Placement.Base.y = Spreadsheet.OuterScrew2Y
FEATURE [App::Link] Link004  label="Fastener_WoodScrew_Outer3"
  LinkPlacement = pos=(-78.4928,-445.155,0) rot=(0,0,1;0rad)
  LinkedObject = -> Link003
  Placement = pos=(-78.4928,-445.155,0) rot=(0,0,1;0rad)
  expr: .Placement.Base.x = Spreadsheet.OuterScrew3X
  expr: .Placement.Base.y = Spreadsheet.OuterScrew3Y
FEATURE [App::Link] Link005  label="Fastener_WoodScrew_Outer4"
  LinkPlacement = pos=(-38.946,-445.155,0) rot=(0,0,1;0rad)
  LinkedObject = -> Link004
  Placement = pos=(-38.946,-445.155,0) rot=(0,0,1;0rad)
  expr: .Placement.Base.x = Spreadsheet.OuterScrew4X
  expr: .Placement.Base.y = Spreadsheet.OuterScrew4Y
FEATURE [App::Link] Link006  label="Fastener_WoodScrew_Outer5"
  LinkPlacement = pos=(38.946,-445.155,0) rot=(0,0,1;0rad)
  LinkedObject = -> Link005
  Placement = pos=(38.946,-445.155,0) rot=(0,0,1;0rad)
  expr: .Placement.Base.x = Spreadsheet.OuterScrew5X
  expr: .Placement.Base.y = Spreadsheet.OuterScrew5Y
FEATURE [App::Link] Link007  label="Fastener_WoodScrew_Outer6"
  LinkPlacement = pos=(78.4928,-445.155,0) rot=(0,0,1;0rad)
  LinkedObject = -> Link006
  Placement = pos=(78.4928,-445.155,0) rot=(0,0,1;0rad)
  expr: .Placement.Base.x = Spreadsheet.OuterScrew6X
  expr: .Placement.Base.y = Spreadsheet.OuterScrew6Y
FEATURE [App::Link] Link008  label="Fastener_WoodScrew_Outer7"
  LinkPlacement = pos=(162.023,-445.155,0) rot=(0,0,1;0rad)
  LinkedObject = -> Link007
  Placement = pos=(162.023,-445.155,0) rot=(0,0,1;0rad)
  expr: .Placement.Base.x = Spreadsheet.OuterScrew7X
  expr: .Placement.Base.y = Spreadsheet.OuterScrew7Y
FEATURE [App::Link] Link009  label="Fastener_WoodScrew_Outer8"
  LinkPlacement = pos=(207.579,-445.155,0) rot=(0,0,1;0rad)
  LinkedObject = -> Link008
  Placement = pos=(207.579,-445.155,0) rot=(0,0,1;0rad)
  expr: .Placement.Base.x = Spreadsheet.OuterScrew8X
  expr: .Placement.Base.y = Spreadsheet.OuterScrew8Y
FEATURE [App::Part] Part001  label="Outer_Screws_Part"
  Group = -> [Link002,Link003,Link004,Link005,Link006,Link007,Link008,Link009]
  Origin = -> Origin002
FEATURE [Part::FeaturePython] Array001  label="SurroundScrews"  # Draft array (typed FeaturePython)
  AlwaysSyncPlacement = false
  Angle = 360
  ArrayType = 1
  Axis = (0,0,1)
  Base = -> Part001
  Center = (0,0,0)
  Count = 6
  ExpandArray = false
  Fuse = false
  IntervalAxis = (0,0,0)
  IntervalX = (50,0,0)
  IntervalY = (0,50,0)
  IntervalZ = (0,0,50)
  NumberCircles = 3
  NumberPolar = 6
  NumberX = 2
  NumberY = 2
  NumberZ = 1
  PlacementList = 6 placements: [(0,0,0),(0,0,0),(0,0,0),(0,0,0),(0,0,0),(0,0,0)]
  RadialDistance = 50
  ScaleList = (6) [(1,1,1),(1,1,1),(1,1,1),(1,1,1),(1,1,1),(1,1,1)]
  Symmetry = 1
  TangentialDistance = 25
  expr: .Placement.Base.z = Spreadsheet.ScrewZ
FEATURE [App::Part] Part003  label="Stator_Mold_BoltShaftLayer_Assembly"
  Group = -> [Binder,Body,Part,Array,Part001,Array001]
  Origin = -> Origin004
---- part Stator_Mold_Island.FCStd = doc fcstd_4d2928485b2e ----
FCSTD DOCUMENT  (FreeCAD 0.21R33771 (Git))
Label: Stator_Mold_Island
License: All rights reserved
LicenseURL: http://en.wikipedia.org/wiki/All_rights_reserved
objects: Sketcher::SketchObject×3, PartDesign::Pocket×2, PartDesign::PolarPattern×2, PartDesign::Pad×1, Spreadsheet::Sheet×1, PartDesign::Body×1
note: 12 computed .brp shape members not serialized (recipe doc carries the construction recipe); baked Part::Feature solids carry a one-line shape summary decoded from their .brp
EXTERNAL_REF file=../../../Master_of_Puppets.FCStd obj=Alternator
EXTERNAL_REF file=../../../Master_of_Puppets.FCStd obj=Spreadsheet

FEATURE [Sketcher::SketchObject] Sketch
  FullyConstrained = true
  MapMode = 5
  Support = -> [XY_Plane001]
  expr: Constraints[1] = Spreadsheet.StatorInnerHoleRadius
  sketch-geometry (1):
    g0: Circle CenterX=0 CenterY=0 CenterZ=0 NormalX=0 NormalY=0 NormalZ=1 AngleXU=0 Radius=45.5337
  constraints (2):
    c: Coincident(g0,g-1)
    c: Radius(g0) = 45.5337
FEATURE [PartDesign::Pad] Pad
  AllowMultiFace = false
  Direction = (0,0,1)
  Length = 8
  Length2 = 100
  Profile = -> Sketch
  Type = 0
  expr: Length = Spreadsheet.StatorThickness
FEATURE [Sketcher::SketchObject] Sketch001  label="BoltSketch"
  FullyConstrained = true
  MapMode = 5
  Placement = pos=(0,0,8) rot=(0,0,1;0rad)
  Support = -> [Pad]
  expr: Constraints[1] = Spreadsheet.IslandInnerRadius
  expr: Constraints[4] = Spreadsheet.StatorMoldBoltRadius
  sketch-geometry (2):
    g0: Circle CenterX=0 CenterY=0 CenterZ=0 NormalX=0 NormalY=0 NormalZ=1 AngleXU=0 Radius=27.5337
    g1: Circle CenterX=0 CenterY=27.5337 CenterZ=0 NormalX=0 NormalY=0 NormalZ=1 AngleXU=0 Radius=5
  constraints (5):
    c: Coincident(g0,g-1)
    c: Radius(g0) = 27.5337
    c: PointOnObject(g1,g0)
    c: PointOnObject(g1,g-2)
    c: Radius(g1) = 5
FEATURE [PartDesign::Pocket] Pocket  label="BoltPocket"
  AllowMultiFace = false
  BaseFeature = -> Pad
  Direction = (0,0,-1)
  Length = 5
  Length2 = 100
  Profile = -> Sketch001
  Type = 1
FEATURE [PartDesign::PolarPattern] PolarPattern  label="BoltPolarPattern"
  Angle = 360
  Axis = -> Sketch001 [N_Axis]
  BaseFeature = -> Pocket
  Occurrences = 4
  Originals = -> [Pocket]
  expr: Occurrences = Spreadsheet.StatorMoldIslandNumberOfBolts
FEATURE [Spreadsheet::Sheet] Spreadsheet
  cells = A1='Inputs; A2='Spreadsheet; A3='StatorThickness; B3(StatorThickness)==Master_of_Puppets#Spreadsheet.StatorThickness; A4='StatorMoldBoltDiameter; B4(StatorMoldBoltDiameter)==Master_of_Puppets#Alternator.StatorMoldBoltDiameter; A5='RotorDiskRadius; B5(RotorDiskRadius)==Master_of_Puppets#Spreadsheet.RotorDiskRadius; A6='Alternator; A7='StatorInnerHoleRadius; B7(StatorInnerHoleRadius)==Master_of_Puppets#Alternator.StatorInnerHoleRadius; A8='IslandInnerRadius; B8(IslandInnerRadius)==Master_of_Puppets#Alternator.IslandInnerRadius; A9='StatorMoldScrewHoleRadius; B9(StatorMoldScrewHoleRadius)==Master_of_Puppets#Alternator.StatorMoldScrewHoleRadius; A10='StatorMoldIslandScrewAngle; B10(StatorMoldIslandScrewAngle)==Master_of_Puppets#Alternator.StatorMoldIslandScrewAngle; A11='StatorMoldIslandNumberOfBolts; B11(StatorMoldIslandNumberOfBolts)==Master_of_Puppets#Alternator.StatorMoldIslandNumberOfBolts; A12='StatorMoldIslandNumberOfScrewSectors; B12(StatorMoldIslandNumberOfScrewSectors)==Master_of_Puppets#Alternator.StatorMoldIslandNumberOfScrewSectors; A13='Calculated; A14='StatorMoldBoltRadius; B14(StatorMoldBoltRadius)==StatorMoldBoltDiameter / 2
FEATURE [Sketcher::SketchObject] Sketch002  label="ScrewSketch"
  FullyConstrained = true
  MapMode = 5
  Placement = pos=(0,0,8) rot=(0,0,1;0rad)
  Support = -> [Pad]
  expr: Constraints[1] = Spreadsheet.IslandInnerRadius
  expr: Constraints[4] = Spreadsheet.StatorMoldIslandScrewAngle
  expr: Constraints[5] = Spreadsheet.StatorMoldScrewHoleRadius
  sketch-geometry (3):
    g0: Circle CenterX=0 CenterY=0 CenterZ=0 NormalX=0 NormalY=0 NormalZ=1 AngleXU=0 Radius=27.5337
    g1: Circle CenterX=-13.7668 CenterY=23.8449 CenterZ=0 NormalX=0 NormalY=0 NormalZ=1 AngleXU=0 Radius=1.5
    g2: LineSegment StartX=0 StartY=0 StartZ=0 EndX=-13.7668 EndY=23.8449 EndZ=0
  constraints (7):
    c: Coincident(g0,g-1)
    c: Radius(g0) = 27.5337
    c: PointOnObject(g1,g0)
    c: Coincident(g2,g1)
    c: Angle(g-2,g2) = 0.523599
    c: Radius(g1) = 1.5
    c: Coincident(g2,g-1)
FEATURE [PartDesign::Pocket] Pocket001  label="ScrewPocket"
  BaseFeature = -> PolarPattern
  Direction = (0,0,-1)
  Length = 5
  Length2 = 100
  Profile = -> Sketch002
  Type = 1
FEATURE [PartDesign::PolarPattern] PolarPattern001  label="ScrewPolarPattern"
  Angle = 360
  Axis = -> Sketch002 [N_Axis]
  BaseFeature = -> Pocket001
  Occurrences = 12
  Originals = -> [Pocket001]
  expr: Occurrences = Spreadsheet.StatorMoldIslandNumberOfScrewSectors
FEATURE [PartDesign::Body] PolarPatternBody  label="Stator_Mold_Island"
  Group = -> [Sketch,Pad,Sketch001,Pocket,PolarPattern,Sketch002,Pocket001,PolarPattern001]
  Openafpm_Flat = true
  Origin = -> Origin001
  Tip = -> PolarPattern001
---- part Stator_Mold_Lid.FCStd = doc fcstd_bc924020b10b ----
FCSTD DOCUMENT  (FreeCAD 0.21R33771 (Git))
Label: Stator_Mold_Lid
License: All rights reserved
LicenseURL: http://en.wikipedia.org/wiki/All_rights_reserved
objects: Spreadsheet::Sheet×1, PartDesign::Plane×1, Sketcher::SketchObject×1, App::Link×1, PartDesign::SubShapeBinder×1, PartDesign::FeatureBase×1, PartDesign::Pocket×1, PartDesign::Body×1
note: 7 computed .brp shape members not serialized (recipe doc carries the construction recipe); baked Part::Feature solids carry a one-line shape summary decoded from their .brp
EXTERNAL_REF file=../../../Master_of_Puppets.FCStd obj=Alternator
EXTERNAL_REF file=../../../Master_of_Puppets.FCStd obj=Spreadsheet
EXTERNAL_REF file=Stator_Mold_BoltShaftPattern_Circular.FCStd obj=Body
EXTERNAL_REF file=Stator_Mold_BoltShaftPattern_Hexagonal.FCStd obj=Body

FEATURE [Spreadsheet::Sheet] Spreadsheet
  cells = A1='Inputs; A2='StatorThickness; B2(StatorThickness)==Master_of_Puppets#Spreadsheet.StatorThickness; A3='CalculatedWindTurbineShape; B3(CalculatedWindTurbineShape)==Master_of_Puppets#Spreadsheet.CalculatedWindTurbineShape; A4='StatorMoldSideLength; B4(StatorMoldSideLength)==Master_of_Puppets#Alternator.StatorMoldSideLength; A5='StatorMoldSurroundEdgeRadius; B5(StatorMoldSurroundEdgeRadius)==Master_of_Puppets#Alternator.StatorMoldSurroundEdgeRadius; A6='OutsideCoilEdgeRadius; B6(OutsideCoilEdgeRadius)==Master_of_Puppets#Alternator.OutsideCoilEdgeRadius; A7='WireTubeDiameter; B7(WireTubeDiameter)==Master_of_Puppets#Alternator.WireTubeDiameter; A8='RadiusOfResinAroundWireTube; B8(RadiusOfResinAroundWireTube)==Master_of_Puppets#Alternator.RadiusOfResinAroundWireTube; A9='LidNotchDegrees; B9(LidNotchDegrees)==Master_of_Puppets#Alternator.LidNotchDegrees; A10='Calculated; A11='WireTubeRadius; B11(WireTubeRadius)==WireTubeDiameter / 2; A12='HalfwayBetweenCoilAndSurroundEdge; B12(HalfwayBetweenCoilAndSurroundEdge)==(StatorMoldSurroundEdgeRadius + OutsideCoilEdgeRadius) / 2; A13='PocketAngle; B13(PocketAngle)=6; A14='PocketY; B14(PocketY)==abs(sin(LidNotchDegrees) * HalfwayBetweenCoilAndSurroundEdge); A15='NotchRadius; B15(NotchRadius)==WireTubeRadius + RadiusOfResinAroundWireTube; A16='TubePaddingFactor; B16(TubePaddingFactor)=1.05; A17='PocketX; B17(PocketX)==abs(cos(LidNotchDegrees) * HalfwayBetweenCoilAndSurroundEdge); A18='PocketLength; B18(PocketLength)==StatorMoldSideLength / 2 - PocketX; C18='HexagonalStatorOuterInradius; A19='BoltShaftPattern; A20='SmallBoltShaftPattern; B20(SmallBoltShaftPattern)==Stator_Mold_BoltShaftPattern_Circular#<<Stator_Mold_BoltShaftPattern>>._self; A21='LargeBoltShaftPattern; B21(LargeBoltShaftPattern)==Stator_Mold_BoltShaftPattern_Hexagonal#<<Stator_Mold_BoltShaftPattern>>._self; A22='BoltShaftPattern; B22(BoltShaftPattern)==CalculatedWindTurbineShape == <<Star>> ? LargeBoltShaftPattern : SmallBoltShaftPattern
FEATURE [PartDesign::Plane] DatumPlane
  Length = 712.38
  MapMode = 2
  Placement = pos=(0,0,13) rot=(0,0,1;0rad)
  ResizeMode = 0
  Width = 712.38
  expr: .Placement.Base.z = Spreadsheet.StatorThickness
FEATURE [Sketcher::SketchObject] Sketch004  label="Sketch"
  FullyConstrained = true
  MapMode = 5
  Placement = pos=(0,0,13) rot=(0,0,1;0rad)
  Support = -> [DatumPlane]
  expr: Constraints[13] = Spreadsheet.NotchRadius
  expr: Constraints[14] = Spreadsheet.PocketAngle / 2
  expr: Constraints[19] = Spreadsheet.PocketY
  expr: Constraints[20] = Spreadsheet.PocketX
  expr: Constraints[3] = Spreadsheet.PocketLength
  sketch-geometry (7):
    g0: LineSegment StartX=-178.743 StartY=-44.5171 StartZ=0 EndX=-296.825 EndY=-50.7056 EndZ=0
    g1: LineSegment StartX=-178.743 StartY=-18.5171 StartZ=0 EndX=-296.825 EndY=-12.3287 EndZ=0
    g2: ArcOfCircle CenterX=-178.743 CenterY=-31.5171 CenterZ=0 NormalX=0 NormalY=0 NormalZ=1 AngleXU=0 Radius=13 StartAngle=4.71239 EndAngle=7.85398
    g3: LineSegment StartX=-178.743 StartY=-31.5171 StartZ=0 EndX=-296.825 EndY=-31.5171 EndZ=0
    g4: LineSegment StartX=-296.825 StartY=-12.3287 StartZ=0 EndX=-296.825 EndY=-31.5171 EndZ=0
    g5: LineSegment StartX=-296.825 StartY=-31.5171 StartZ=0 EndX=-296.825 EndY=-50.7056 EndZ=0
    g6: LineSegment StartX=-178.743 StartY=-31.5171 StartZ=0 EndX=-165.743 EndY=-31.5171 EndZ=0
  constraints (21):
    c: Coincident(g1,g2)
    c: Coincident(g0,g2)
    c: Coincident(g3,g2)
    c: Distance(g3) = 118.082
    c: Coincident(g1,g4)
    c: Coincident(g4,g3)
    c: Coincident(g4,g5)
    c: Coincident(g5,g0)
    c: Horizontal(g3)
    c: Angle(g2) = 3.14159
    c: Coincident(g6,g2)
    c: PointOnObject(g6,g2)
    c: Horizontal(g6)
    c: Distance(g6) = 13
    c: Angle(g3,g0) = 0.0523599
    c: Vertical(g5)
    c: Vertical(g4)
    c: Equal(g4,g5)
    c: Vertical(g2,g0)
    c: DistanceY(g2,g-1) = 31.5171
    c: DistanceX(g2,g-1) = 178.743
FEATURE [App::Link] Link  label="Stator_Mold_BoltShaftPattern"
  LinkedObject = -> <external Stator_Mold_BoltShaftPattern_Circular.FCStd>#Body
  expr: LinkedObject = Spreadsheet.BoltShaftPattern
FEATURE [PartDesign::SubShapeBinder] Binder
  BindCopyOnChange = 0
  BindMode = 0
  ClaimChildren = false
  Context = -> Pocket003Body [Binder.]
  Fuse = false
  MakeFace = true
  OffsetFill = false
  OffsetIntersection = false
  OffsetJoinType = 0
  OffsetOpenResult = false
  PartialLoad = false
  Refine = true
  Relative = true
  Support = -> [Link]
  _Version = 2
FEATURE [PartDesign::FeatureBase] BaseFeature
  BaseFeature = -> Binder
FEATURE [PartDesign::Pocket] Pocket003  label="Pocket"
  AllowMultiFace = false
  BaseFeature = -> BaseFeature
  Direction = (0,0,-1)
  Length = 5
  Length2 = 100
  Profile = -> Sketch004
  Type = 1
FEATURE [PartDesign::Body] Pocket003Body  label="Stator_Mold_Lid"
  BaseFeature = -> Binder
  Group = -> [BaseFeature,Sketch004,Pocket003,DatumPlane,Binder]
  Openafpm_Flat = true
  Origin = -> Origin001
  Tip = -> Pocket003
---- part Stator_Mold_Surround_Circular.FCStd = doc fcstd_9d61dd9bcd55 ----
FCSTD DOCUMENT  (FreeCAD 0.21R33771 (Git))
Label: Stator_Mold_Surround_Circular
License: All rights reserved
LicenseURL: http://en.wikipedia.org/wiki/All_rights_reserved
objects: Spreadsheet::Sheet×1, PartDesign::Plane×1, Sketcher::SketchObject×1, App::Link×1, PartDesign::SubShapeBinder×1, PartDesign::FeatureBase×1, PartDesign::Pocket×1, PartDesign::PolarPattern×1, PartDesign::Body×1
note: 8 computed .brp shape members not serialized (recipe doc carries the construction recipe); baked Part::Feature solids carry a one-line shape summary decoded from their .brp
EXTERNAL_REF file=../../../Master_of_Puppets.FCStd obj=Alternator
EXTERNAL_REF file=../../../Master_of_Puppets.FCStd obj=Spreadsheet
EXTERNAL_REF file=Stator_Mold_BoltShaftLayer_Circular.FCStd obj=Body

FEATURE [Spreadsheet::Sheet] Spreadsheet
  cells = A1='Inputs; A2='StatorThickness; B2='RotorDiskRadius; C2='NumberOfHoles; A3(StatorThickness)==Master_of_Puppets#Spreadsheet.StatorThickness; B3(RotorDiskRadius)==Master_of_Puppets#Spreadsheet.RotorDiskRadius; C3(NumberOfHoles)==Master_of_Puppets#Alternator.NumberOfStatorHoles; A4='EarAngle; B4='EarSize; C4='StatorHolesCircumradius; A5(EarAngle)==Master_of_Puppets#Alternator.EarAngle; B5(EarSize)==Master_of_Puppets#Alternator.EarSize; C5(StatorHolesCircumradius)==Master_of_Puppets#Alternator.StatorHolesCircumradius; A6='StatorMoldHolesSketchAngle; A7(StatorMoldHolesSketchAngle)==Master_of_Puppets#Alternator.StatorMoldHolesSketchAngle
FEATURE [PartDesign::Plane] DatumPlane001  label="DatumPlane"
  AttachmentOffset = pos=(0,0,13) rot=(0,0,1;0rad)
  Length = 1056.48
  MapMode = 5
  Placement = pos=(0,0,13) rot=(0,0,1;0rad)
  ResizeMode = 0
  Support = -> [XY_Plane]
  Width = 1056.48
  expr: .AttachmentOffset.Base.z = Spreadsheet.StatorThickness
FEATURE [Sketcher::SketchObject] Sketch004  label="ResinCastSketch"
  AttachmentOffset = pos=(0,0,0) rot=(0,0,1;0.785398rad)
  FullyConstrained = true
  MapMode = 5
  Placement = pos=(0,0,13) rot=(0,0,1;0.785398rad)
  Support = -> [DatumPlane001]
  expr: .AttachmentOffset.Rotation.Angle = Spreadsheet.StatorMoldHolesSketchAngle
  expr: Constraints[3] = Spreadsheet.StatorHolesCircumradius
  expr: Constraints[9] = Spreadsheet.EarSize
  sketch-geometry (10):
    g0: Circle CenterX=0 CenterY=0 CenterZ=0 NormalX=0 NormalY=0 NormalZ=1 AngleXU=0 Radius=284
    g1: LineSegment StartX=0 StartY=0 StartZ=0 EndX=0 EndY=-284 EndZ=0
    g2: Circle CenterX=0 CenterY=-284 CenterZ=0 NormalX=0 NormalY=0 NormalZ=1 AngleXU=0 Radius=35
    g3: LineSegment StartX=16.8324 StartY=-314.687 StartZ=0 EndX=136.583 EndY=-249 EndZ=0
    g4: LineSegment StartX=-16.8324 StartY=-314.687 StartZ=0 EndX=-136.583 EndY=-249 EndZ=0
    g5: ArcOfCircle CenterX=0 CenterY=-284 CenterZ=0 NormalX=0 NormalY=0 NormalZ=1 AngleXU=0 Radius=35 StartAngle=4.21068 EndAngle=5.2141
    g6: LineSegment StartX=0 StartY=0 StartZ=0 EndX=-245.951 EndY=-142 EndZ=0
    g7: LineSegment StartX=0 StartY=0 StartZ=0 EndX=245.951 EndY=-142 EndZ=0
    g8: ArcOfCircle CenterX=0 CenterY=0 CenterZ=0 NormalX=0 NormalY=0 NormalZ=1 AngleXU=0 Radius=284 StartAngle=3.66519 EndAngle=4.21068
    g9: ArcOfCircle CenterX=0 CenterY=0 CenterZ=0 NormalX=0 NormalY=0 NormalZ=1 AngleXU=0 Radius=284 StartAngle=5.2141 EndAngle=5.75959
  constraints (24):
    c: Coincident(g0,g-1)
    c: Coincident(g1,g-1)
    c: Vertical(g1)
    c: Radius(g0) = 284
    c: Coincident(g2,g1)
    c: Coincident(g5,g1)
    c: Coincident(g5,g3)
    c: Coincident(g5,g4)
    c: PointOnObject(g5,g0)
    c: Radius(g2) = 35
    c: Coincident(g8,g6)
    c: Coincident(g8,g4)
    c: Coincident(g9,g7)
    c: Coincident(g9,g3)
    c: Coincident(g7,g6)
    c: Coincident(g6,g8)
    c: Coincident(g6,g-1)
    c: Coincident(g9,g6)
    c: Tangent(g3,g2) = -1.5708
    c: Tangent(g4,g0) = 1.5708
    c: Tangent(g4,g2) = 1.5708
    c: Tangent(g3,g0) = -1.5708
    c: Angle(g7,g-1) = 0.523599
    c: Angle(g6,g7) = 2.0944
FEATURE [App::Link] Link  label="Stator_Mold_BoltShaftLayer"
  LinkedObject = -> <external Stator_Mold_BoltShaftLayer_Circular.FCStd>#Body
FEATURE [PartDesign::SubShapeBinder] Binder
  BindCopyOnChange = 0
  BindMode = 0
  ClaimChildren = true
  Context = -> Body [Binder.]
  Fuse = false
  MakeFace = true
  OffsetFill = false
  OffsetIntersection = false
  OffsetJoinType = 0
  OffsetOpenResult = false
  PartialLoad = false
  Refine = true
  Relative = true
  Support = -> [Link]
  _Version = 2
FEATURE [PartDesign::FeatureBase] BaseFeature
  BaseFeature = -> Binder
FEATURE [PartDesign::Pocket] Pocket  label="ResinCastPocket"
  BaseFeature = -> BaseFeature
  Direction = (0,0,-1)
  Length = 5
  Length2 = 100
  Profile = -> Sketch004
  Type = 1
FEATURE [PartDesign::PolarPattern] PolarPattern001  label="ResinCastPocketPolarPattern"
  Angle = 360
  Axis = -> Sketch004 [N_Axis]
  BaseFeature = -> Pocket
  Occurrences = 4
  Originals = -> [Pocket]
  expr: Occurrences = Spreadsheet.NumberOfHoles
FEATURE [PartDesign::Body] Body  label="Stator_Mold_Surround"
  BaseFeature = -> Binder
  Group = -> [BaseFeature,DatumPlane001,Sketch004,Pocket,PolarPattern001,Binder]
  Openafpm_Flat = true
  Origin = -> Origin
  Tip = -> PolarPattern001
---- part Stator_Mold_Surround_Hexagonal.FCStd = doc fcstd_0fea89b8dc58 ----
FCSTD DOCUMENT  (FreeCAD 0.20R29177 (Git))
Label: Stator_Mold_Surround_Hexagonal
License: All rights reserved
LicenseURL: http://en.wikipedia.org/wiki/All_rights_reserved
objects: Spreadsheet::Sheet×1, PartDesign::Plane×1, PartDesign::SubShapeBinder×1, PartDesign::FeatureBase×1, Sketcher::SketchObject×1, PartDesign::Pocket×1, PartDesign::Body×1
note: 7 computed .brp shape members not serialized (recipe doc carries the construction recipe); baked Part::Feature solids carry a one-line shape summary decoded from their .brp
EXTERNAL_REF file=../../../Master_of_Puppets.FCStd obj=Alternator
EXTERNAL_REF file=../../../Master_of_Puppets.FCStd obj=Spreadsheet
EXTERNAL_REF file=Stator_Mold_BoltShaftLayer_Hexagonal.FCStd obj=Body

FEATURE [Spreadsheet::Sheet] Spreadsheet
  cells = A1=Inputs; A2=StatorThickness; B2=HexagonalStatorOuterCircumradius; A3(StatorThickness)==Master_of_Puppets#Spreadsheet.StatorThickness; B3(HexagonalStatorOuterCircumradius)==Master_of_Puppets#Alternator.HexagonalStatorOuterCircumradius
FEATURE [PartDesign::Plane] DatumPlane001  label="DatumPlane"
  AttachmentOffset = pos=(0,0,13) rot=(0,0,1;0rad)
  Length = 60
  MapMode = 5
  Placement = pos=(0,0,13) rot=(0,0,1;0rad)
  ResizeMode = 0
  Support = -> [XY_Plane]
  Width = 60
  expr: .AttachmentOffset.Base.z = Spreadsheet.StatorThickness
FEATURE [PartDesign::SubShapeBinder] Binder001  label="Binder"
  BindCopyOnChange = 0
  BindMode = 0
  ClaimChildren = true
  Context = -> Body [Binder001.]
  Fuse = false
  MakeFace = true
  OffsetFill = false
  OffsetIntersection = false
  OffsetJoinType = 0
  OffsetOpenResult = false
  PartialLoad = false
  Refine = true
  Relative = true
  Support = -> [<external Stator_Mold_BoltShaftLayer_Hexagonal.FCStd>#Body]
  _Version = 2
FEATURE [PartDesign::FeatureBase] BaseFeature
  BaseFeature = -> Binder001
FEATURE [Sketcher::SketchObject] Sketch
  FullyConstrained = true
  MapMode = 5
  Placement = pos=(0,0,13) rot=(0,0,1;0rad)
  Support = -> [DatumPlane001]
  expr: Constraints[17] = Spreadsheet.HexagonalStatorOuterCircumradius
  sketch-geometry (7):
    g0: LineSegment StartX=110.563 StartY=191.5 StartZ=0 EndX=-110.563 EndY=191.5 EndZ=0
    g1: LineSegment StartX=-110.563 StartY=191.5 StartZ=0 EndX=-221.125 EndY=0 EndZ=0
    g2: LineSegment StartX=-221.125 StartY=0 StartZ=0 EndX=-110.563 EndY=-191.5 EndZ=0
    g3: LineSegment StartX=-110.563 StartY=-191.5 StartZ=0 EndX=110.563 EndY=-191.5 EndZ=0
    g4: LineSegment StartX=110.563 StartY=-191.5 StartZ=0 EndX=221.125 EndY=0 EndZ=0
    g5: LineSegment StartX=221.125 StartY=0 StartZ=0 EndX=110.563 EndY=191.5 EndZ=0
    g6: Circle CenterX=0 CenterY=0 CenterZ=0 NormalX=0 NormalY=0 NormalZ=1 AngleXU=0 Radius=221.125
  constraints (16):
    c: Coincident(g0,g1)
    c: Coincident(g1,g2)
    c: Coincident(g2,g3)
    c: Coincident(g3,g4)
    c: Coincident(g4,g5)
    c: Coincident(g5,g0)
    c: Equal(g0, g1-g5) x5
    c: PointOnObject(g0,g6)
    c: PointOnObject(g1,g6)
    c: PointOnObject(g2,g6)
    c: PointOnObject(g3,g6)
    c: PointOnObject(g4,g6)
    c: PointOnObject(g5,g6)
    c: Radius(g6) = 221.125
    c: Horizontal(g1,g4)
    c: Coincident(g6,g-1)
FEATURE [PartDesign::Pocket] Pocket
  BaseFeature = -> BaseFeature
  Direction = (0,0,-1)
  Length = 5
  Length2 = 100
  Profile = -> Sketch
  Type = 1
FEATURE [PartDesign::Body] Body  label="Stator_Mold_Surround"
  BaseFeature = -> Binder001
  Group = -> [BaseFeature,DatumPlane001,Binder001,Sketch,Pocket]
  Openafpm_Flat = true
  Origin = -> Origin
  Tip = -> Pocket
